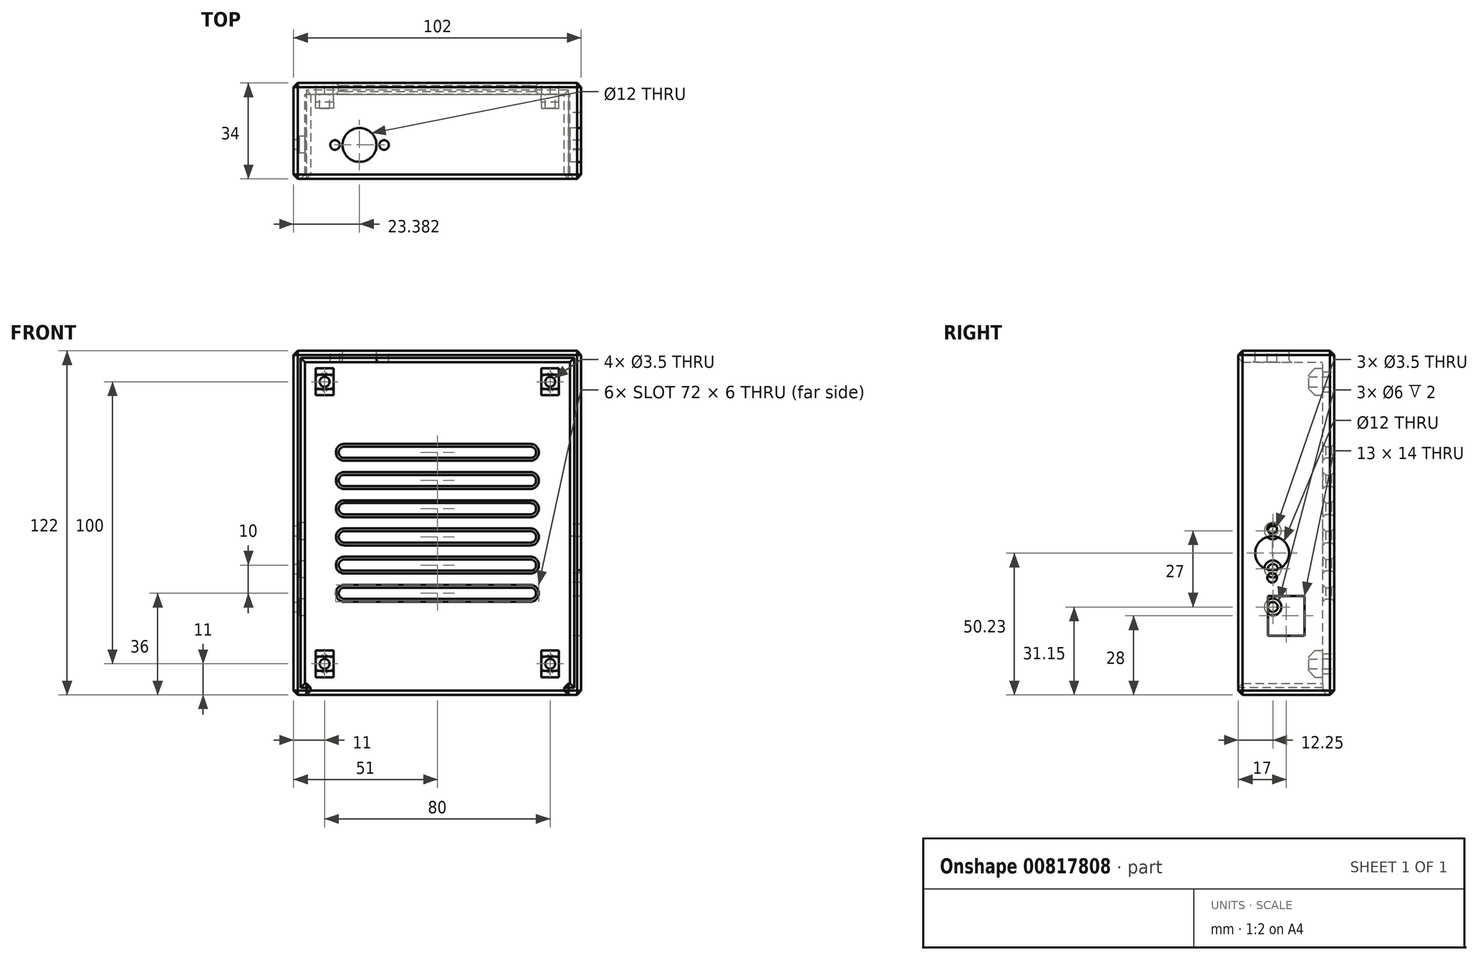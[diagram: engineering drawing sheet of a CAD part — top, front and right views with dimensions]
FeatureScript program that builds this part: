
annotation { "Feature Type Name" : "Feature", "Feature Type Description" : "" }
export const myFeature = defineFeature(function(context is Context, id is Id, definition is map)
    precondition{}
    {
        {
            var Q0;
            Q0=qCreatedBy(makeId("Front.planeOp"),FACE);
            var sketch = newSketch(context, id + "F0", { "sketchPlane" : qUnion([Q0])});
            skLineSegment(sketch, "E0.bottom", {"start": v(51, -61) * mm, "end": v(-51, -61) * mm});
            skLineSegment(sketch, "E0.top", {"start": v(51, 61) * mm, "end": v(-51, 61) * mm});
            skLineSegment(sketch, "E0.left", {"start": v(51, -61) * mm, "end": v(51, 61) * mm});
            skLineSegment(sketch, "E0.right", {"start": v(-51, -61) * mm, "end": v(-51, 61) * mm});
            skPoint(sketch, "E0.middle", {"position": v(0, 0) * mm});
            skCircle(sketch, "E1", {"center": v(-40, 50) * mm, "radius": 1.75 * mm});
            skCircle(sketch, "E2", {"center": v(40, 50) * mm, "radius": 1.75 * mm});
            skCircle(sketch, "E3", {"center": v(-40, -50) * mm, "radius": 1.75 * mm});
            skCircle(sketch, "E4", {"center": v(40, -50) * mm, "radius": 1.75 * mm});
            skLineSegment(sketch, "E5.bottom", {"start": v(47, -57) * mm, "end": v(-47, -57) * mm});
            skLineSegment(sketch, "E5.top", {"start": v(47, 57) * mm, "end": v(-47, 57) * mm});
            skLineSegment(sketch, "E5.left", {"start": v(47, -57) * mm, "end": v(47, 57) * mm});
            skLineSegment(sketch, "E5.right", {"start": v(-47, -57) * mm, "end": v(-47, 57) * mm});
            skLineSegment(sketch, "E6.bottom", {"start": v(-36.88, -54.75) * mm, "end": v(-43.13, -54.75) * mm});
            skLineSegment(sketch, "E6.top", {"start": v(-36.88, -45.25) * mm, "end": v(-43.13, -45.25) * mm});
            skLineSegment(sketch, "E6.left", {"start": v(-36.88, -54.75) * mm, "end": v(-36.88, -45.25) * mm});
            skLineSegment(sketch, "E6.right", {"start": v(-43.13, -54.75) * mm, "end": v(-43.13, -45.25) * mm});
            skLineSegment(sketch, "E7.bottom", {"start": v(36.88, -54.75) * mm, "end": v(43.12, -54.75) * mm});
            skLineSegment(sketch, "E7.top", {"start": v(36.88, -45.25) * mm, "end": v(43.12, -45.25) * mm});
            skLineSegment(sketch, "E7.left", {"start": v(36.88, -54.75) * mm, "end": v(36.88, -45.25) * mm});
            skLineSegment(sketch, "E7.right", {"start": v(43.12, -54.75) * mm, "end": v(43.12, -45.25) * mm});
            skLineSegment(sketch, "E8.bottom", {"start": v(-36.88, 45.25) * mm, "end": v(-43.13, 45.25) * mm});
            skLineSegment(sketch, "E8.top", {"start": v(-36.88, 54.75) * mm, "end": v(-43.13, 54.75) * mm});
            skLineSegment(sketch, "E8.left", {"start": v(-36.88, 45.25) * mm, "end": v(-36.88, 54.75) * mm});
            skLineSegment(sketch, "E8.right", {"start": v(-43.13, 45.25) * mm, "end": v(-43.13, 54.75) * mm});
            skLineSegment(sketch, "E9.bottom", {"start": v(36.88, 45.25) * mm, "end": v(43.12, 45.25) * mm});
            skLineSegment(sketch, "E9.top", {"start": v(36.87, 54.75) * mm, "end": v(43.12, 54.75) * mm});
            skLineSegment(sketch, "E9.left", {"start": v(36.88, 45.25) * mm, "end": v(36.88, 54.75) * mm});
            skLineSegment(sketch, "E9.right", {"start": v(43.12, 45.25) * mm, "end": v(43.12, 54.75) * mm});
            skLineSegment(sketch, "E10.bottom", {"start": v(35, 13) * mm, "end": v(-35, 13) * mm});
            skLineSegment(sketch, "E10.top", {"start": v(35, 17) * mm, "end": v(-35, 17) * mm});
            skLineSegment(sketch, "E10.left", {"start": v(35, 13) * mm, "end": v(35, 17) * mm});
            skLineSegment(sketch, "E10.right", {"start": v(-35, 13) * mm, "end": v(-35, 17) * mm});
            skPoint(sketch, "E10.middle", {"position": v(0, 15) * mm});
            skLineSegment(sketch, "E11.bottom", {"start": v(35, 3) * mm, "end": v(-35, 3) * mm});
            skLineSegment(sketch, "E11.top", {"start": v(35, 7) * mm, "end": v(-35, 7) * mm});
            skLineSegment(sketch, "E11.left", {"start": v(35, 3) * mm, "end": v(35, 7) * mm});
            skLineSegment(sketch, "E11.right", {"start": v(-35, 3) * mm, "end": v(-35, 7) * mm});
            skPoint(sketch, "E11.middle", {"position": v(0, 5) * mm});
            skLineSegment(sketch, "E12.bottom", {"start": v(35, 23) * mm, "end": v(-35, 23) * mm});
            skLineSegment(sketch, "E12.top", {"start": v(35, 27) * mm, "end": v(-35, 27) * mm});
            skLineSegment(sketch, "E12.left", {"start": v(35, 23) * mm, "end": v(35, 27) * mm});
            skLineSegment(sketch, "E12.right", {"start": v(-35, 23) * mm, "end": v(-35, 27) * mm});
            skPoint(sketch, "E12.middle", {"position": v(0, 25) * mm});
            skLineSegment(sketch, "E13.bottom", {"start": v(35, -7) * mm, "end": v(-35, -7) * mm});
            skLineSegment(sketch, "E13.top", {"start": v(35, -3) * mm, "end": v(-35, -3) * mm});
            skLineSegment(sketch, "E13.left", {"start": v(35, -7) * mm, "end": v(35, -3) * mm});
            skLineSegment(sketch, "E13.right", {"start": v(-35, -7) * mm, "end": v(-35, -3) * mm});
            skPoint(sketch, "E13.middle", {"position": v(0, -5) * mm});
            skLineSegment(sketch, "E14.bottom", {"start": v(35, -17) * mm, "end": v(-35, -17) * mm});
            skLineSegment(sketch, "E14.top", {"start": v(35, -13) * mm, "end": v(-35, -13) * mm});
            skLineSegment(sketch, "E14.left", {"start": v(35, -17) * mm, "end": v(35, -13) * mm});
            skLineSegment(sketch, "E14.right", {"start": v(-35, -17) * mm, "end": v(-35, -13) * mm});
            skPoint(sketch, "E14.middle", {"position": v(0, -15) * mm});
            skLineSegment(sketch, "E15.bottom", {"start": v(35, -27) * mm, "end": v(-35, -27) * mm});
            skLineSegment(sketch, "E15.top", {"start": v(35, -23) * mm, "end": v(-35, -23) * mm});
            skLineSegment(sketch, "E15.left", {"start": v(35, -27) * mm, "end": v(35, -23) * mm});
            skLineSegment(sketch, "E15.right", {"start": v(-35, -27) * mm, "end": v(-35, -23) * mm});
            skPoint(sketch, "E15.middle", {"position": v(0, -25) * mm});
            skLineSegment(sketch, "E16", {"start": v(-45, -57) * mm, "end": v(-45, -61) * mm});
            skLineSegment(sketch, "E17", {"start": v(45, -57) * mm, "end": v(45, -61) * mm});
            skCircle(sketch, "E18.cCircle", {"center": v(40, 50) * mm, "radius": 3.08 * mm, "construction": true});
            skLineSegment(sketch, "E18.0", {"start": v(36.92, 48.22) * mm, "end": v(36.92, 51.78) * mm});
            skLineSegment(sketch, "E18.1", {"start": v(36.93, 51.78) * mm, "end": v(40, 53.55) * mm});
            skLineSegment(sketch, "E18.2", {"start": v(40, 53.55) * mm, "end": v(43.07, 51.78) * mm});
            skLineSegment(sketch, "E18.3", {"start": v(43.07, 51.78) * mm, "end": v(43.08, 48.22) * mm});
            skLineSegment(sketch, "E18.4", {"start": v(43.08, 48.22) * mm, "end": v(40, 46.45) * mm});
            skLineSegment(sketch, "E18.5", {"start": v(40, 46.45) * mm, "end": v(36.93, 48.22) * mm});
            skPoint(sketch, "E18.0.midPoint", {"position": v(36.92, 50) * mm});
            skCircle(sketch, "E19.cCircle", {"center": v(-40, 50) * mm, "radius": 3.08 * mm, "construction": true});
            skLineSegment(sketch, "E19.0", {"start": v(-36.92, 51.78) * mm, "end": v(-36.92, 48.22) * mm});
            skLineSegment(sketch, "E19.1", {"start": v(-36.92, 48.22) * mm, "end": v(-40, 46.45) * mm});
            skLineSegment(sketch, "E19.2", {"start": v(-40, 46.45) * mm, "end": v(-43.07, 48.22) * mm});
            skLineSegment(sketch, "E19.3", {"start": v(-43.07, 48.22) * mm, "end": v(-43.07, 51.78) * mm});
            skLineSegment(sketch, "E19.4", {"start": v(-43.08, 51.78) * mm, "end": v(-40, 53.55) * mm});
            skLineSegment(sketch, "E19.5", {"start": v(-40, 53.55) * mm, "end": v(-36.92, 51.78) * mm});
            skPoint(sketch, "E19.0.midPoint", {"position": v(-36.92, 50) * mm});
            skCircle(sketch, "E20.cCircle", {"center": v(40, -50) * mm, "radius": 3.08 * mm, "construction": true});
            skPoint(sketch, "E20.cCircle.perimeterSnap0", {"position": v(43.12, -50) * mm});
            skLineSegment(sketch, "E20.0", {"start": v(43.08, -48.22) * mm, "end": v(43.08, -51.78) * mm});
            skLineSegment(sketch, "E20.1", {"start": v(43.07, -51.78) * mm, "end": v(40, -53.55) * mm});
            skLineSegment(sketch, "E20.2", {"start": v(40, -53.55) * mm, "end": v(36.93, -51.78) * mm});
            skLineSegment(sketch, "E20.3", {"start": v(36.93, -51.78) * mm, "end": v(36.93, -48.22) * mm});
            skLineSegment(sketch, "E20.4", {"start": v(36.93, -48.22) * mm, "end": v(40, -46.45) * mm});
            skLineSegment(sketch, "E20.5", {"start": v(40, -46.45) * mm, "end": v(43.07, -48.22) * mm});
            skPoint(sketch, "E20.0.midPoint", {"position": v(43.08, -50) * mm});
            skPoint(sketch, "E20.0.midPoint.positionSnap0", {"position": v(43.12, -50) * mm});
            skCircle(sketch, "E21.cCircle", {"center": v(-40, -50) * mm, "radius": 3.08 * mm, "construction": true});
            skLineSegment(sketch, "E21.0", {"start": v(-36.93, -48.22) * mm, "end": v(-36.93, -51.78) * mm});
            skLineSegment(sketch, "E21.1", {"start": v(-36.93, -51.78) * mm, "end": v(-40, -53.55) * mm});
            skLineSegment(sketch, "E21.2", {"start": v(-40, -53.55) * mm, "end": v(-43.08, -51.78) * mm});
            skLineSegment(sketch, "E21.3", {"start": v(-43.08, -51.78) * mm, "end": v(-43.08, -48.22) * mm});
            skLineSegment(sketch, "E21.4", {"start": v(-43.08, -48.22) * mm, "end": v(-40, -46.45) * mm});
            skLineSegment(sketch, "E21.5", {"start": v(-40, -46.45) * mm, "end": v(-36.93, -48.22) * mm});
            skPoint(sketch, "E21.0.midPoint", {"position": v(-36.93, -50) * mm});
            skSolve(sketch);
        }
        {
            var Q0;
            Q0=makeQuery(id+"F0.imprint","IMPRINT",FACE,{"disambiguationData":[TD([[makeQuery(id+"F0.imprint","IMPRINT",EDGE,{"derivedFrom":sQuery(id+"F0.wireOp",EDGE,"E5.top")}),1.0]])]});
            var Q1;
            {var subQ0=sQuery(id+"F0.wireOp",EDGE,"E16");Q1=makeQuery(id+"F0.imprint","IMPRINT",FACE,{"disambiguationData":[TD([[makeQuery(id+"F0.imprint","IMPRINT",EDGE,{"derivedFrom":subQ0}),1.0]])]});}
            extrude(context, id + "F1", {"entities" : qUnion([Q0, Q1]), "depth" : 4 * mm, "offsetDistance" : 25 * mm});
        }
        {
            var Q0;
            Q0=makeQuery(id+"F0.imprint","IMPRINT",FACE,{"disambiguationData":[TD([[makeQuery(id+"F0.imprint","IMPRINT",EDGE,{"derivedFrom":sQuery(id+"F0.wireOp",EDGE,"E3")}),-1.0]])]});
            var Q1;
            Q1=makeQuery(id+"F0.imprint","IMPRINT",FACE,{"disambiguationData":[TD([[makeQuery(id+"F0.imprint","IMPRINT",EDGE,{"derivedFrom":sQuery(id+"F0.wireOp",EDGE,"E4")}),-1.0]])]});
            var Q2;
            Q2=makeQuery(id+"F0.imprint","IMPRINT",FACE,{"disambiguationData":[TD([[makeQuery(id+"F0.imprint","IMPRINT",EDGE,{"derivedFrom":sQuery(id+"F0.wireOp",EDGE,"E2")}),-1.0]])]});
            var Q3;
            Q3=makeQuery(id+"F0.imprint","IMPRINT",FACE,{"disambiguationData":[TD([[makeQuery(id+"F0.imprint","IMPRINT",EDGE,{"derivedFrom":sQuery(id+"F0.wireOp",EDGE,"E1")}),-1.0]])]});
            var Q4;
            Q4=makeQuery(id+"F0.imprint","IMPRINT",FACE,{"disambiguationData":[TD([[makeQuery(id+"F0.imprint","IMPRINT",EDGE,{"derivedFrom":sQuery(id+"F0.wireOp",EDGE,"E7.bottom")}),1.0]])]});
            var Q5;
            Q5=makeQuery(id+"F0.imprint","IMPRINT",FACE,{"disambiguationData":[TD([[makeQuery(id+"F0.imprint","IMPRINT",EDGE,{"derivedFrom":sQuery(id+"F0.wireOp",EDGE,"E6.bottom")}),-1.0]])]});
            var Q6;
            Q6=makeQuery(id+"F0.imprint","IMPRINT",FACE,{"disambiguationData":[TD([[makeQuery(id+"F0.imprint","IMPRINT",EDGE,{"derivedFrom":sQuery(id+"F0.wireOp",EDGE,"E8.bottom")}),-1.0]])]});
            var Q7;
            Q7=makeQuery(id+"F0.imprint","IMPRINT",FACE,{"disambiguationData":[TD([[makeQuery(id+"F0.imprint","IMPRINT",EDGE,{"derivedFrom":sQuery(id+"F0.wireOp",EDGE,"E9.bottom")}),1.0]])]});
            extrude(context, id + "F2", {"entities" : qUnion([Q0, Q1, Q2, Q3, Q4, Q5, Q6, Q7]), "operationType" : NewBodyOperationType.ADD, "depth" : 9 * mm, "offsetDistance" : 25 * mm});
        }
        {
            var Q0;
            Q0=makeQuery(id+"F2.opExtrude","CAP_EDGE",EDGE,{"disambiguationData":[OSD([sQuery(id+"F0.wireOp",EDGE,"E6.top")])],"isStart":false});
            var Q1;
            Q1=makeQuery(id+"F2.opExtrude","CAP_EDGE",EDGE,{"disambiguationData":[OSD([sQuery(id+"F0.wireOp",EDGE,"E6.bottom")])],"isStart":false});
            var Q2;
            Q2=makeQuery(id+"F2.opExtrude","CAP_EDGE",EDGE,{"disambiguationData":[OSD([sQuery(id+"F0.wireOp",EDGE,"E7.top")])],"isStart":false});
            var Q3;
            Q3=makeQuery(id+"F2.opExtrude","CAP_EDGE",EDGE,{"disambiguationData":[OSD([sQuery(id+"F0.wireOp",EDGE,"E7.bottom")])],"isStart":false});
            var Q4;
            Q4=makeQuery(id+"F2.opExtrude","CAP_EDGE",EDGE,{"disambiguationData":[OSD([sQuery(id+"F0.wireOp",EDGE,"E8.top")])],"isStart":false});
            var Q5;
            Q5=makeQuery(id+"F2.opExtrude","CAP_EDGE",EDGE,{"disambiguationData":[OSD([sQuery(id+"F0.wireOp",EDGE,"E8.bottom")])],"isStart":false});
            var Q6;
            Q6=makeQuery(id+"F2.opExtrude","CAP_EDGE",EDGE,{"disambiguationData":[OSD([sQuery(id+"F0.wireOp",EDGE,"E9.top")])],"isStart":false});
            var Q7;
            Q7=makeQuery(id+"F2.opExtrude","CAP_EDGE",EDGE,{"disambiguationData":[OSD([sQuery(id+"F0.wireOp",EDGE,"E9.bottom")])],"isStart":false});
            chamfer(context, id + "F3", {"entities" : qUnion([Q0, Q1, Q2, Q3, Q4, Q5, Q6, Q7]), "width" : 2.2 * mm, "tangentPropagation" : true});
        }
        {
            var Q0;
            Q0=makeQuery(id+"F1.opExtrude","SWEPT_EDGE",EDGE,{"disambiguationData":[OSD([sQuery(id+"F0.wireOp",EDGE,"E15.bottom"),sQuery(id+"F0.wireOp",EDGE,"E15.left")])]});
            var Q1;
            Q1=makeQuery(id+"F1.opExtrude","SWEPT_EDGE",EDGE,{"disambiguationData":[OSD([sQuery(id+"F0.wireOp",EDGE,"E15.top"),sQuery(id+"F0.wireOp",EDGE,"E15.left")])]});
            var Q2;
            Q2=makeQuery(id+"F1.opExtrude","SWEPT_EDGE",EDGE,{"disambiguationData":[OSD([sQuery(id+"F0.wireOp",EDGE,"E14.top"),sQuery(id+"F0.wireOp",EDGE,"E14.left")])]});
            var Q3;
            Q3=makeQuery(id+"F1.opExtrude","SWEPT_EDGE",EDGE,{"disambiguationData":[OSD([sQuery(id+"F0.wireOp",EDGE,"E13.top"),sQuery(id+"F0.wireOp",EDGE,"E13.left")])]});
            var Q4;
            Q4=makeQuery(id+"F1.opExtrude","SWEPT_EDGE",EDGE,{"disambiguationData":[OSD([sQuery(id+"F0.wireOp",EDGE,"E11.top"),sQuery(id+"F0.wireOp",EDGE,"E11.left")])]});
            var Q5;
            Q5=makeQuery(id+"F1.opExtrude","SWEPT_EDGE",EDGE,{"disambiguationData":[OSD([sQuery(id+"F0.wireOp",EDGE,"E10.top"),sQuery(id+"F0.wireOp",EDGE,"E10.left")])]});
            var Q6;
            Q6=makeQuery(id+"F1.opExtrude","SWEPT_EDGE",EDGE,{"disambiguationData":[OSD([sQuery(id+"F0.wireOp",EDGE,"E12.top"),sQuery(id+"F0.wireOp",EDGE,"E12.left")])]});
            var Q7;
            Q7=makeQuery(id+"F1.opExtrude","SWEPT_EDGE",EDGE,{"disambiguationData":[OSD([sQuery(id+"F0.wireOp",EDGE,"E12.top"),sQuery(id+"F0.wireOp",EDGE,"E12.right")])]});
            var Q8;
            Q8=makeQuery(id+"F1.opExtrude","SWEPT_EDGE",EDGE,{"disambiguationData":[OSD([sQuery(id+"F0.wireOp",EDGE,"E10.top"),sQuery(id+"F0.wireOp",EDGE,"E10.right")])]});
            var Q9;
            Q9=makeQuery(id+"F1.opExtrude","SWEPT_EDGE",EDGE,{"disambiguationData":[OSD([sQuery(id+"F0.wireOp",EDGE,"E11.top"),sQuery(id+"F0.wireOp",EDGE,"E11.right")])]});
            var Q10;
            Q10=makeQuery(id+"F1.opExtrude","SWEPT_EDGE",EDGE,{"disambiguationData":[OSD([sQuery(id+"F0.wireOp",EDGE,"E13.top"),sQuery(id+"F0.wireOp",EDGE,"E13.right")])]});
            var Q11;
            Q11=makeQuery(id+"F1.opExtrude","SWEPT_EDGE",EDGE,{"disambiguationData":[OSD([sQuery(id+"F0.wireOp",EDGE,"E14.top"),sQuery(id+"F0.wireOp",EDGE,"E14.right")])]});
            var Q12;
            Q12=makeQuery(id+"F1.opExtrude","SWEPT_EDGE",EDGE,{"disambiguationData":[OSD([sQuery(id+"F0.wireOp",EDGE,"E15.top"),sQuery(id+"F0.wireOp",EDGE,"E15.right")])]});
            var Q13;
            Q13=makeQuery(id+"F1.opExtrude","SWEPT_EDGE",EDGE,{"disambiguationData":[OSD([sQuery(id+"F0.wireOp",EDGE,"E14.bottom"),sQuery(id+"F0.wireOp",EDGE,"E14.left")])]});
            var Q14;
            Q14=makeQuery(id+"F1.opExtrude","SWEPT_EDGE",EDGE,{"disambiguationData":[OSD([sQuery(id+"F0.wireOp",EDGE,"E13.bottom"),sQuery(id+"F0.wireOp",EDGE,"E13.left")])]});
            var Q15;
            Q15=makeQuery(id+"F1.opExtrude","SWEPT_EDGE",EDGE,{"disambiguationData":[OSD([sQuery(id+"F0.wireOp",EDGE,"E11.bottom"),sQuery(id+"F0.wireOp",EDGE,"E11.left")])]});
            var Q16;
            Q16=makeQuery(id+"F1.opExtrude","SWEPT_EDGE",EDGE,{"disambiguationData":[OSD([sQuery(id+"F0.wireOp",EDGE,"E10.bottom"),sQuery(id+"F0.wireOp",EDGE,"E10.left")])]});
            var Q17;
            Q17=makeQuery(id+"F1.opExtrude","SWEPT_EDGE",EDGE,{"disambiguationData":[OSD([sQuery(id+"F0.wireOp",EDGE,"E12.bottom"),sQuery(id+"F0.wireOp",EDGE,"E12.left")])]});
            var Q18;
            Q18=makeQuery(id+"F1.opExtrude","SWEPT_EDGE",EDGE,{"disambiguationData":[OSD([sQuery(id+"F0.wireOp",EDGE,"E12.bottom"),sQuery(id+"F0.wireOp",EDGE,"E12.right")])]});
            var Q19;
            Q19=makeQuery(id+"F1.opExtrude","SWEPT_EDGE",EDGE,{"disambiguationData":[OSD([sQuery(id+"F0.wireOp",EDGE,"E10.bottom"),sQuery(id+"F0.wireOp",EDGE,"E10.right")])]});
            var Q20;
            Q20=makeQuery(id+"F1.opExtrude","SWEPT_EDGE",EDGE,{"disambiguationData":[OSD([sQuery(id+"F0.wireOp",EDGE,"E11.bottom"),sQuery(id+"F0.wireOp",EDGE,"E11.right")])]});
            var Q21;
            Q21=makeQuery(id+"F1.opExtrude","SWEPT_EDGE",EDGE,{"disambiguationData":[OSD([sQuery(id+"F0.wireOp",EDGE,"E13.bottom"),sQuery(id+"F0.wireOp",EDGE,"E13.right")])]});
            var Q22;
            Q22=makeQuery(id+"F1.opExtrude","SWEPT_EDGE",EDGE,{"disambiguationData":[OSD([sQuery(id+"F0.wireOp",EDGE,"E14.bottom"),sQuery(id+"F0.wireOp",EDGE,"E14.right")])]});
            var Q23;
            Q23=makeQuery(id+"F1.opExtrude","SWEPT_EDGE",EDGE,{"disambiguationData":[OSD([sQuery(id+"F0.wireOp",EDGE,"E15.bottom"),sQuery(id+"F0.wireOp",EDGE,"E15.right")])]});
            fillet(context, id + "F4", {"entities" : qUnion([Q0, Q1, Q2, Q3, Q4, Q5, Q6, Q7, Q8, Q9, Q10, Q11, Q12, Q13, Q14, Q15, Q16, Q17, Q18, Q19, Q20, Q21, Q22, Q23]), "radius" : 2 * mm, "tangentPropagation" : true, "allowEdgeOverflow" : false});
        }
        {
            var Q0;
            Q0=makeQuery(id+"F0.imprint","IMPRINT",FACE,{"disambiguationData":[TD([[makeQuery(id+"F0.imprint","IMPRINT",EDGE,{"derivedFrom":sQuery(id+"F0.wireOp",EDGE,"E0.top")}),1.0]])]});
            extrude(context, id + "F5", {"entities" : qUnion([Q0]), "operationType" : NewBodyOperationType.ADD, "depth" : 34 * mm, "offsetDistance" : 25 * mm});
        }
        {
            var Q0;
            Q0=makeQuery(id+"F0.imprint","IMPRINT",FACE,{"disambiguationData":[TD([[makeQuery(id+"F0.imprint","IMPRINT",EDGE,{"derivedFrom":sQuery(id+"F0.wireOp",EDGE,"E2")}),-1.0]])]});
            var Q1;
            Q1=makeQuery(id+"F0.imprint","IMPRINT",FACE,{"disambiguationData":[TD([[makeQuery(id+"F0.imprint","IMPRINT",EDGE,{"derivedFrom":sQuery(id+"F0.wireOp",EDGE,"E1")}),-1.0]])]});
            var Q2;
            Q2=makeQuery(id+"F0.imprint","IMPRINT",FACE,{"disambiguationData":[TD([[makeQuery(id+"F0.imprint","IMPRINT",EDGE,{"derivedFrom":sQuery(id+"F0.wireOp",EDGE,"E4")}),-1.0]])]});
            var Q3;
            Q3=makeQuery(id+"F0.imprint","IMPRINT",FACE,{"disambiguationData":[TD([[makeQuery(id+"F0.imprint","IMPRINT",EDGE,{"derivedFrom":sQuery(id+"F0.wireOp",EDGE,"E3")}),-1.0]])]});
            extrude(context, id + "F6", {"entities" : qUnion([Q0, Q1, Q2, Q3]), "operationType" : NewBodyOperationType.REMOVE, "depth" : 4 * mm, "offsetDistance" : 25 * mm});
        }
        {
            var Q0;
            Q0=makeQuery(id+"F5.opExtrude","SWEPT_FACE",FACE,{"disambiguationData":[OSD([sQuery(id+"F0.wireOp",EDGE,"E5.left")])]});
            var sketch = newSketch(context, id + "F7", { "sketchPlane" : qUnion([Q0])});
            skLineSegment(sketch, "E22.bottom", {"start": v(23.5, -40) * mm, "end": v(10.5, -40) * mm});
            skLineSegment(sketch, "E22.top", {"start": v(23.5, -26) * mm, "end": v(10.5, -26) * mm});
            skLineSegment(sketch, "E22.left", {"start": v(23.5, -40) * mm, "end": v(23.5, -26) * mm});
            skLineSegment(sketch, "E22.right", {"start": v(10.5, -40) * mm, "end": v(10.5, -26) * mm});
            skPoint(sketch, "E22.middle", {"position": v(17, -33) * mm});
            skCircle(sketch, "E23", {"center": v(22, -10.77) * mm, "radius": 6 * mm});
            skCircle(sketch, "E24", {"center": v(22, -19.47) * mm, "radius": 1.7 * mm});
            skCircle(sketch, "E25", {"center": v(22, -2.07) * mm, "radius": 1.7 * mm});
            skSolve(sketch);
        }
        {
            var Q0;
            Q0=makeQuery(id+"F7.imprint","IMPRINT",FACE,{"disambiguationData":[TD([[makeQuery(id+"F7.imprint","IMPRINT",EDGE,{"derivedFrom":sQuery(id+"F7.wireOp",EDGE,"E22.bottom")}),-1.0]])]});
            var Q1;
            Q1=makeQuery(id+"F7.imprint","IMPRINT",FACE,{"disambiguationData":[TD([[makeQuery(id+"F7.imprint","IMPRINT",EDGE,{"derivedFrom":sQuery(id+"F7.wireOp",EDGE,"E23")}),1.0]])]});
            var Q2;
            Q2=makeQuery(id+"F7.imprint","IMPRINT",FACE,{"disambiguationData":[TD([[makeQuery(id+"F7.imprint","IMPRINT",EDGE,{"derivedFrom":sQuery(id+"F7.wireOp",EDGE,"E24")}),1.0]])]});
            var Q3;
            Q3=makeQuery(id+"F7.imprint","IMPRINT",FACE,{"disambiguationData":[TD([[makeQuery(id+"F7.imprint","IMPRINT",EDGE,{"derivedFrom":sQuery(id+"F7.wireOp",EDGE,"E25")}),1.0]])]});
            extrude(context, id + "F8", {"entities" : qUnion([Q0, Q1, Q2, Q3]), "operationType" : NewBodyOperationType.REMOVE, "oppositeDirection" : true, "depth" : 5 * mm, "offsetDistance" : 25 * mm});
        }
        {
            var Q0;
            Q0=makeQuery(id+"F5.opExtrude","SWEPT_FACE",FACE,{"disambiguationData":[OSD([sQuery(id+"F0.wireOp",EDGE,"E0.top")])]});
            var sketch = newSketch(context, id + "F9", { "sketchPlane" : qUnion([Q0])});
            skCircle(sketch, "E26", {"center": v(-27.62, -22) * mm, "radius": 6 * mm});
            skCircle(sketch, "E27", {"center": v(-18.92, -22) * mm, "radius": 1.7 * mm});
            skCircle(sketch, "E28", {"center": v(-36.32, -22) * mm, "radius": 1.7 * mm});
            skSolve(sketch);
        }
        {
            var Q0;
            Q0=makeQuery(id+"F9.imprint","IMPRINT",FACE,{"disambiguationData":[TD([[makeQuery(id+"F9.imprint","IMPRINT",EDGE,{"derivedFrom":sQuery(id+"F9.wireOp",EDGE,"E26")}),1.0]])]});
            var Q1;
            Q1=makeQuery(id+"F9.imprint","IMPRINT",FACE,{"disambiguationData":[TD([[makeQuery(id+"F9.imprint","IMPRINT",EDGE,{"derivedFrom":sQuery(id+"F9.wireOp",EDGE,"E28")}),1.0]])]});
            var Q2;
            Q2=makeQuery(id+"F9.imprint","IMPRINT",FACE,{"disambiguationData":[TD([[makeQuery(id+"F9.imprint","IMPRINT",EDGE,{"derivedFrom":sQuery(id+"F9.wireOp",EDGE,"E27")}),1.0]])]});
            extrude(context, id + "F10", {"entities" : qUnion([Q0, Q1, Q2]), "operationType" : NewBodyOperationType.REMOVE, "oppositeDirection" : true, "depth" : 5 * mm, "offsetDistance" : 25 * mm});
        }
        {
            var Q0;
            Q0=makeQuery(id+"F5.opExtrude","CAP_EDGE",EDGE,{"disambiguationData":[OSD([sQuery(id+"F0.wireOp",EDGE,"E0.left")])],"isStart":true});
            var Q1;
            Q1=makeQuery(id+"F5.opExtrude","SWEPT_EDGE",EDGE,{"disambiguationData":[OSD([sQuery(id+"F0.wireOp",EDGE,"E0.top"),sQuery(id+"F0.wireOp",EDGE,"E0.left")])]});
            var Q2;
            Q2=makeQuery(id+"F5.opExtrude","CAP_EDGE",EDGE,{"disambiguationData":[OSD([sQuery(id+"F0.wireOp",EDGE,"E0.left")])],"isStart":false});
            var Q3;
            Q3=makeQuery(id+"F5.opExtrude","CAP_EDGE",EDGE,{"disambiguationData":[OSD([sQuery(id+"F0.wireOp",EDGE,"E0.top")])],"isStart":false});
            var Q4;
            Q4=makeQuery(id+"F5.opExtrude","CAP_EDGE",EDGE,{"disambiguationData":[OSD([sQuery(id+"F0.wireOp",EDGE,"E0.top")])],"isStart":true});
            var Q5;
            Q5=makeQuery(id+"F5.opExtrude","CAP_EDGE",EDGE,{"disambiguationData":[OSD([sQuery(id+"F0.wireOp",EDGE,"E0.right")])],"isStart":true});
            var Q6;
            Q6=makeQuery(id+"F5.opExtrude","SWEPT_EDGE",EDGE,{"disambiguationData":[OSD([sQuery(id+"F0.wireOp",EDGE,"E0.top"),sQuery(id+"F0.wireOp",EDGE,"E0.right")])]});
            var Q7;
            Q7=makeQuery(id+"F5.opExtrude","CAP_EDGE",EDGE,{"disambiguationData":[OSD([sQuery(id+"F0.wireOp",EDGE,"E0.right")])],"isStart":false});
            var Q8;
            Q8=makeQuery(id+"F5.opExtrude","SWEPT_EDGE",EDGE,{"disambiguationData":[OSD([sQuery(id+"F0.wireOp",EDGE,"E0.bottom"),sQuery(id+"F0.wireOp",EDGE,"E0.right")])]});
            var Q9;
            {var subQ0=sQuery(id+"F0.wireOp",EDGE,"E0.bottom");Q9=makeQuery(id+"F5.boolean.opBoolean","MERGE",EDGE,{"derivedFrom":[makeQuery(id+"F1.opExtrude","CAP_EDGE",EDGE,{"disambiguationData":[OSD([subQ0])],"isStart":true}),makeQuery(id+"F5.opExtrude","CAP_EDGE",EDGE,{"disambiguationData":[OSD([subQ0]),TDD([makeQuery(id+"F0.imprint","IMPRINT",EDGE,{"disambiguationData":[TD([[makeQuery(id+"F0.imprint","INTERSECT",VERTEX,{"derivedFrom":[subQ0,sQuery(id+"F0.wireOp",EDGE,"E0.left")]}),-1.0]])],"derivedFrom":subQ0})])],"isStart":true}),makeQuery(id+"F5.opExtrude","CAP_EDGE",EDGE,{"disambiguationData":[OSD([subQ0]),TDD([makeQuery(id+"F0.imprint","IMPRINT",EDGE,{"disambiguationData":[TD([[makeQuery(id+"F0.imprint","INTERSECT",VERTEX,{"derivedFrom":[subQ0,sQuery(id+"F0.wireOp",EDGE,"E0.right")]}),1.0]])],"derivedFrom":subQ0})])],"isStart":true})]});}
            var Q10;
            Q10=makeQuery(id+"F5.opExtrude","SWEPT_EDGE",EDGE,{"disambiguationData":[OSD([sQuery(id+"F0.wireOp",EDGE,"E0.bottom"),sQuery(id+"F0.wireOp",EDGE,"E0.left")])]});
            var Q11;
            Q11=makeQuery(id+"F5.opExtrude","SWEPT_EDGE",EDGE,{"disambiguationData":[OSD([sQuery(id+"F0.wireOp",EDGE,"E0.bottom"),sQuery(id+"F0.wireOp",EDGE,"E17")])]});
            var Q12;
            {var subQ0=sQuery(id+"F0.wireOp",EDGE,"E0.bottom");Q12=makeQuery(id+"F5.opExtrude","CAP_EDGE",EDGE,{"disambiguationData":[OSD([subQ0]),TDD([makeQuery(id+"F0.imprint","IMPRINT",EDGE,{"disambiguationData":[TD([[makeQuery(id+"F0.imprint","INTERSECT",VERTEX,{"derivedFrom":[subQ0,sQuery(id+"F0.wireOp",EDGE,"E0.left")]}),-1.0]])],"derivedFrom":subQ0})])],"isStart":false});}
            var Q13;
            {var subQ0=sQuery(id+"F0.wireOp",EDGE,"E0.bottom");Q13=makeQuery(id+"F5.opExtrude","CAP_EDGE",EDGE,{"disambiguationData":[OSD([subQ0]),TDD([makeQuery(id+"F0.imprint","IMPRINT",EDGE,{"disambiguationData":[TD([[makeQuery(id+"F0.imprint","INTERSECT",VERTEX,{"derivedFrom":[subQ0,sQuery(id+"F0.wireOp",EDGE,"E0.right")]}),1.0]])],"derivedFrom":subQ0})])],"isStart":false});}
            var Q14;
            Q14=makeQuery(id+"F5.opExtrude","CAP_EDGE",EDGE,{"disambiguationData":[OSD([sQuery(id+"F0.wireOp",EDGE,"E5.left")])],"isStart":false});
            var Q15;
            Q15=makeQuery(id+"F5.opExtrude","CAP_EDGE",EDGE,{"disambiguationData":[OSD([sQuery(id+"F0.wireOp",EDGE,"E5.top")])],"isStart":false});
            var Q16;
            Q16=makeQuery(id+"F5.opExtrude","CAP_EDGE",EDGE,{"disambiguationData":[OSD([sQuery(id+"F0.wireOp",EDGE,"E5.right")])],"isStart":false});
            var Q17;
            {var subQ0=sQuery(id+"F0.wireOp",EDGE,"E5.bottom");Q17=makeQuery(id+"F5.opExtrude","CAP_EDGE",EDGE,{"disambiguationData":[OSD([subQ0]),TDD([makeQuery(id+"F0.imprint","IMPRINT",EDGE,{"disambiguationData":[TD([[makeQuery(id+"F0.imprint","INTERSECT",VERTEX,{"derivedFrom":[subQ0,sQuery(id+"F0.wireOp",EDGE,"E5.left")]}),-1.0]])],"derivedFrom":subQ0})])],"isStart":false});}
            var Q18;
            Q18=makeQuery(id+"F5.opExtrude","CAP_EDGE",EDGE,{"disambiguationData":[OSD([sQuery(id+"F0.wireOp",EDGE,"E17")])],"isStart":false});
            var Q19;
            {var subQ0=sQuery(id+"F0.wireOp",EDGE,"E5.bottom");Q19=makeQuery(id+"F5.opExtrude","CAP_EDGE",EDGE,{"disambiguationData":[OSD([subQ0]),TDD([makeQuery(id+"F0.imprint","IMPRINT",EDGE,{"disambiguationData":[TD([[makeQuery(id+"F0.imprint","INTERSECT",VERTEX,{"derivedFrom":[subQ0,sQuery(id+"F0.wireOp",EDGE,"E5.right")]}),1.0]])],"derivedFrom":subQ0})])],"isStart":false});}
            var Q20;
            Q20=makeQuery(id+"F5.opExtrude","SWEPT_EDGE",EDGE,{"disambiguationData":[OSD([sQuery(id+"F0.wireOp",EDGE,"E5.bottom"),sQuery(id+"F0.wireOp",EDGE,"E16")])]});
            var Q21;
            Q21=makeQuery(id+"F5.opExtrude","SWEPT_EDGE",EDGE,{"disambiguationData":[OSD([sQuery(id+"F0.wireOp",EDGE,"E0.bottom"),sQuery(id+"F0.wireOp",EDGE,"E16")])]});
            var Q22;
            Q22=makeQuery(id+"F5.opExtrude","CAP_EDGE",EDGE,{"disambiguationData":[OSD([sQuery(id+"F0.wireOp",EDGE,"E16")])],"isStart":false});
            var Q23;
            Q23=makeQuery(id+"F1.opExtrude","CAP_EDGE",EDGE,{"disambiguationData":[OSD([sQuery(id+"F0.wireOp",EDGE,"E0.bottom")])],"isStart":false});
            var Q24;
            Q24=makeQuery(id+"F5.opExtrude","SWEPT_EDGE",EDGE,{"disambiguationData":[OSD([sQuery(id+"F0.wireOp",EDGE,"E5.bottom"),sQuery(id+"F0.wireOp",EDGE,"E17")])]});
            chamfer(context, id + "F11", {"entities" : qUnion([Q0, Q1, Q2, Q3, Q4, Q5, Q6, Q7, Q8, Q9, Q10, Q11, Q12, Q13, Q14, Q15, Q16, Q17, Q18, Q19, Q20, Q21, Q22, Q23, Q24]), "width" : 1.5 * mm, "tangentPropagation" : true});
        }
        {
            var Q0;
            Q0=makeQuery(id+"F1.opExtrude","CAP_EDGE",EDGE,{"disambiguationData":[OSD([sQuery(id+"F0.wireOp",EDGE,"E15.bottom")])],"isStart":false});
            var Q1;
            {var subQ0=sQuery(id+"F0.wireOp",EDGE,"E15.right");var subQ1=sQuery(id+"F0.wireOp",EDGE,"E15.top");Q1=makeQuery(id+"F4.opFillet","BLEND_EDGE",EDGE,{"blendedFrom":[makeQuery(id+"F1.opExtrude","SWEPT_EDGE",EDGE,{"disambiguationData":[OSD([subQ1,subQ0])]}),makeQuery(id+"F1.opExtrude","CAP_FACE",FACE,{"disambiguationData":[OSD([sQuery(id+"F0.wireOp",EDGE,"E0.bottom"),sQuery(id+"F0.wireOp",EDGE,"E5.bottom"),sQuery(id+"F0.wireOp",EDGE,"E5.top"),sQuery(id+"F0.wireOp",EDGE,"E5.left"),sQuery(id+"F0.wireOp",EDGE,"E5.right"),sQuery(id+"F0.wireOp",EDGE,"E6.bottom"),sQuery(id+"F0.wireOp",EDGE,"E6.top"),sQuery(id+"F0.wireOp",EDGE,"E6.left"),sQuery(id+"F0.wireOp",EDGE,"E6.right"),sQuery(id+"F0.wireOp",EDGE,"E7.bottom"),sQuery(id+"F0.wireOp",EDGE,"E7.top"),sQuery(id+"F0.wireOp",EDGE,"E7.left"),sQuery(id+"F0.wireOp",EDGE,"E7.right"),sQuery(id+"F0.wireOp",EDGE,"E8.bottom"),sQuery(id+"F0.wireOp",EDGE,"E8.top"),sQuery(id+"F0.wireOp",EDGE,"E8.left"),sQuery(id+"F0.wireOp",EDGE,"E8.right"),sQuery(id+"F0.wireOp",EDGE,"E9.bottom"),sQuery(id+"F0.wireOp",EDGE,"E9.top"),sQuery(id+"F0.wireOp",EDGE,"E9.left"),sQuery(id+"F0.wireOp",EDGE,"E9.right"),sQuery(id+"F0.wireOp",EDGE,"E10.bottom"),sQuery(id+"F0.wireOp",EDGE,"E10.top"),sQuery(id+"F0.wireOp",EDGE,"E10.left"),sQuery(id+"F0.wireOp",EDGE,"E10.right"),sQuery(id+"F0.wireOp",EDGE,"E11.bottom"),sQuery(id+"F0.wireOp",EDGE,"E11.top"),sQuery(id+"F0.wireOp",EDGE,"E11.left"),sQuery(id+"F0.wireOp",EDGE,"E11.right"),sQuery(id+"F0.wireOp",EDGE,"E12.bottom"),sQuery(id+"F0.wireOp",EDGE,"E12.top"),sQuery(id+"F0.wireOp",EDGE,"E12.left"),sQuery(id+"F0.wireOp",EDGE,"E12.right"),sQuery(id+"F0.wireOp",EDGE,"E13.bottom"),sQuery(id+"F0.wireOp",EDGE,"E13.top"),sQuery(id+"F0.wireOp",EDGE,"E13.left"),sQuery(id+"F0.wireOp",EDGE,"E13.right"),sQuery(id+"F0.wireOp",EDGE,"E14.bottom"),sQuery(id+"F0.wireOp",EDGE,"E14.top"),sQuery(id+"F0.wireOp",EDGE,"E14.left"),sQuery(id+"F0.wireOp",EDGE,"E14.right"),sQuery(id+"F0.wireOp",EDGE,"E15.bottom"),subQ1,sQuery(id+"F0.wireOp",EDGE,"E15.left"),subQ0,sQuery(id+"F0.wireOp",EDGE,"E16"),sQuery(id+"F0.wireOp",EDGE,"E17")])],"isStart":false})],"blendedInto":[makeQuery(id+"F1.opExtrude","CAP_FACE",FACE,{"disambiguationData":[OSD([sQuery(id+"F0.wireOp",EDGE,"E0.bottom"),sQuery(id+"F0.wireOp",EDGE,"E5.bottom"),sQuery(id+"F0.wireOp",EDGE,"E5.top"),sQuery(id+"F0.wireOp",EDGE,"E5.left"),sQuery(id+"F0.wireOp",EDGE,"E5.right"),sQuery(id+"F0.wireOp",EDGE,"E6.bottom"),sQuery(id+"F0.wireOp",EDGE,"E6.top"),sQuery(id+"F0.wireOp",EDGE,"E6.left"),sQuery(id+"F0.wireOp",EDGE,"E6.right"),sQuery(id+"F0.wireOp",EDGE,"E7.bottom"),sQuery(id+"F0.wireOp",EDGE,"E7.top"),sQuery(id+"F0.wireOp",EDGE,"E7.left"),sQuery(id+"F0.wireOp",EDGE,"E7.right"),sQuery(id+"F0.wireOp",EDGE,"E8.bottom"),sQuery(id+"F0.wireOp",EDGE,"E8.top"),sQuery(id+"F0.wireOp",EDGE,"E8.left"),sQuery(id+"F0.wireOp",EDGE,"E8.right"),sQuery(id+"F0.wireOp",EDGE,"E9.bottom"),sQuery(id+"F0.wireOp",EDGE,"E9.top"),sQuery(id+"F0.wireOp",EDGE,"E9.left"),sQuery(id+"F0.wireOp",EDGE,"E9.right"),sQuery(id+"F0.wireOp",EDGE,"E10.bottom"),sQuery(id+"F0.wireOp",EDGE,"E10.top"),sQuery(id+"F0.wireOp",EDGE,"E10.left"),sQuery(id+"F0.wireOp",EDGE,"E10.right"),sQuery(id+"F0.wireOp",EDGE,"E11.bottom"),sQuery(id+"F0.wireOp",EDGE,"E11.top"),sQuery(id+"F0.wireOp",EDGE,"E11.left"),sQuery(id+"F0.wireOp",EDGE,"E11.right"),sQuery(id+"F0.wireOp",EDGE,"E12.bottom"),sQuery(id+"F0.wireOp",EDGE,"E12.top"),sQuery(id+"F0.wireOp",EDGE,"E12.left"),sQuery(id+"F0.wireOp",EDGE,"E12.right"),sQuery(id+"F0.wireOp",EDGE,"E13.bottom"),sQuery(id+"F0.wireOp",EDGE,"E13.top"),sQuery(id+"F0.wireOp",EDGE,"E13.left"),sQuery(id+"F0.wireOp",EDGE,"E13.right"),sQuery(id+"F0.wireOp",EDGE,"E14.bottom"),sQuery(id+"F0.wireOp",EDGE,"E14.top"),sQuery(id+"F0.wireOp",EDGE,"E14.left"),sQuery(id+"F0.wireOp",EDGE,"E14.right"),sQuery(id+"F0.wireOp",EDGE,"E15.bottom"),subQ1,sQuery(id+"F0.wireOp",EDGE,"E15.left"),subQ0,sQuery(id+"F0.wireOp",EDGE,"E16"),sQuery(id+"F0.wireOp",EDGE,"E17")])],"isStart":false})]});}
            var Q2;
            Q2=makeQuery(id+"F1.opExtrude","CAP_EDGE",EDGE,{"disambiguationData":[OSD([sQuery(id+"F0.wireOp",EDGE,"E15.top")])],"isStart":false});
            var Q3;
            {var subQ0=sQuery(id+"F0.wireOp",EDGE,"E15.left");var subQ1=sQuery(id+"F0.wireOp",EDGE,"E15.bottom");Q3=makeQuery(id+"F4.opFillet","BLEND_EDGE",EDGE,{"blendedFrom":[makeQuery(id+"F1.opExtrude","SWEPT_EDGE",EDGE,{"disambiguationData":[OSD([subQ1,subQ0])]}),makeQuery(id+"F1.opExtrude","CAP_FACE",FACE,{"disambiguationData":[OSD([sQuery(id+"F0.wireOp",EDGE,"E0.bottom"),sQuery(id+"F0.wireOp",EDGE,"E5.bottom"),sQuery(id+"F0.wireOp",EDGE,"E5.top"),sQuery(id+"F0.wireOp",EDGE,"E5.left"),sQuery(id+"F0.wireOp",EDGE,"E5.right"),sQuery(id+"F0.wireOp",EDGE,"E6.bottom"),sQuery(id+"F0.wireOp",EDGE,"E6.top"),sQuery(id+"F0.wireOp",EDGE,"E6.left"),sQuery(id+"F0.wireOp",EDGE,"E6.right"),sQuery(id+"F0.wireOp",EDGE,"E7.bottom"),sQuery(id+"F0.wireOp",EDGE,"E7.top"),sQuery(id+"F0.wireOp",EDGE,"E7.left"),sQuery(id+"F0.wireOp",EDGE,"E7.right"),sQuery(id+"F0.wireOp",EDGE,"E8.bottom"),sQuery(id+"F0.wireOp",EDGE,"E8.top"),sQuery(id+"F0.wireOp",EDGE,"E8.left"),sQuery(id+"F0.wireOp",EDGE,"E8.right"),sQuery(id+"F0.wireOp",EDGE,"E9.bottom"),sQuery(id+"F0.wireOp",EDGE,"E9.top"),sQuery(id+"F0.wireOp",EDGE,"E9.left"),sQuery(id+"F0.wireOp",EDGE,"E9.right"),sQuery(id+"F0.wireOp",EDGE,"E10.bottom"),sQuery(id+"F0.wireOp",EDGE,"E10.top"),sQuery(id+"F0.wireOp",EDGE,"E10.left"),sQuery(id+"F0.wireOp",EDGE,"E10.right"),sQuery(id+"F0.wireOp",EDGE,"E11.bottom"),sQuery(id+"F0.wireOp",EDGE,"E11.top"),sQuery(id+"F0.wireOp",EDGE,"E11.left"),sQuery(id+"F0.wireOp",EDGE,"E11.right"),sQuery(id+"F0.wireOp",EDGE,"E12.bottom"),sQuery(id+"F0.wireOp",EDGE,"E12.top"),sQuery(id+"F0.wireOp",EDGE,"E12.left"),sQuery(id+"F0.wireOp",EDGE,"E12.right"),sQuery(id+"F0.wireOp",EDGE,"E13.bottom"),sQuery(id+"F0.wireOp",EDGE,"E13.top"),sQuery(id+"F0.wireOp",EDGE,"E13.left"),sQuery(id+"F0.wireOp",EDGE,"E13.right"),sQuery(id+"F0.wireOp",EDGE,"E14.bottom"),sQuery(id+"F0.wireOp",EDGE,"E14.top"),sQuery(id+"F0.wireOp",EDGE,"E14.left"),sQuery(id+"F0.wireOp",EDGE,"E14.right"),subQ1,sQuery(id+"F0.wireOp",EDGE,"E15.top"),subQ0,sQuery(id+"F0.wireOp",EDGE,"E15.right"),sQuery(id+"F0.wireOp",EDGE,"E16"),sQuery(id+"F0.wireOp",EDGE,"E17")])],"isStart":false})],"blendedInto":[makeQuery(id+"F1.opExtrude","CAP_FACE",FACE,{"disambiguationData":[OSD([sQuery(id+"F0.wireOp",EDGE,"E0.bottom"),sQuery(id+"F0.wireOp",EDGE,"E5.bottom"),sQuery(id+"F0.wireOp",EDGE,"E5.top"),sQuery(id+"F0.wireOp",EDGE,"E5.left"),sQuery(id+"F0.wireOp",EDGE,"E5.right"),sQuery(id+"F0.wireOp",EDGE,"E6.bottom"),sQuery(id+"F0.wireOp",EDGE,"E6.top"),sQuery(id+"F0.wireOp",EDGE,"E6.left"),sQuery(id+"F0.wireOp",EDGE,"E6.right"),sQuery(id+"F0.wireOp",EDGE,"E7.bottom"),sQuery(id+"F0.wireOp",EDGE,"E7.top"),sQuery(id+"F0.wireOp",EDGE,"E7.left"),sQuery(id+"F0.wireOp",EDGE,"E7.right"),sQuery(id+"F0.wireOp",EDGE,"E8.bottom"),sQuery(id+"F0.wireOp",EDGE,"E8.top"),sQuery(id+"F0.wireOp",EDGE,"E8.left"),sQuery(id+"F0.wireOp",EDGE,"E8.right"),sQuery(id+"F0.wireOp",EDGE,"E9.bottom"),sQuery(id+"F0.wireOp",EDGE,"E9.top"),sQuery(id+"F0.wireOp",EDGE,"E9.left"),sQuery(id+"F0.wireOp",EDGE,"E9.right"),sQuery(id+"F0.wireOp",EDGE,"E10.bottom"),sQuery(id+"F0.wireOp",EDGE,"E10.top"),sQuery(id+"F0.wireOp",EDGE,"E10.left"),sQuery(id+"F0.wireOp",EDGE,"E10.right"),sQuery(id+"F0.wireOp",EDGE,"E11.bottom"),sQuery(id+"F0.wireOp",EDGE,"E11.top"),sQuery(id+"F0.wireOp",EDGE,"E11.left"),sQuery(id+"F0.wireOp",EDGE,"E11.right"),sQuery(id+"F0.wireOp",EDGE,"E12.bottom"),sQuery(id+"F0.wireOp",EDGE,"E12.top"),sQuery(id+"F0.wireOp",EDGE,"E12.left"),sQuery(id+"F0.wireOp",EDGE,"E12.right"),sQuery(id+"F0.wireOp",EDGE,"E13.bottom"),sQuery(id+"F0.wireOp",EDGE,"E13.top"),sQuery(id+"F0.wireOp",EDGE,"E13.left"),sQuery(id+"F0.wireOp",EDGE,"E13.right"),sQuery(id+"F0.wireOp",EDGE,"E14.bottom"),sQuery(id+"F0.wireOp",EDGE,"E14.top"),sQuery(id+"F0.wireOp",EDGE,"E14.left"),sQuery(id+"F0.wireOp",EDGE,"E14.right"),subQ1,sQuery(id+"F0.wireOp",EDGE,"E15.top"),subQ0,sQuery(id+"F0.wireOp",EDGE,"E15.right"),sQuery(id+"F0.wireOp",EDGE,"E16"),sQuery(id+"F0.wireOp",EDGE,"E17")])],"isStart":false})]});}
            var Q4;
            {var subQ0=sQuery(id+"F0.wireOp",EDGE,"E14.left");var subQ1=sQuery(id+"F0.wireOp",EDGE,"E14.bottom");Q4=makeQuery(id+"F4.opFillet","BLEND_EDGE",EDGE,{"blendedFrom":[makeQuery(id+"F1.opExtrude","SWEPT_EDGE",EDGE,{"disambiguationData":[OSD([subQ1,subQ0])]}),makeQuery(id+"F1.opExtrude","CAP_FACE",FACE,{"disambiguationData":[OSD([sQuery(id+"F0.wireOp",EDGE,"E0.bottom"),sQuery(id+"F0.wireOp",EDGE,"E5.bottom"),sQuery(id+"F0.wireOp",EDGE,"E5.top"),sQuery(id+"F0.wireOp",EDGE,"E5.left"),sQuery(id+"F0.wireOp",EDGE,"E5.right"),sQuery(id+"F0.wireOp",EDGE,"E6.bottom"),sQuery(id+"F0.wireOp",EDGE,"E6.top"),sQuery(id+"F0.wireOp",EDGE,"E6.left"),sQuery(id+"F0.wireOp",EDGE,"E6.right"),sQuery(id+"F0.wireOp",EDGE,"E7.bottom"),sQuery(id+"F0.wireOp",EDGE,"E7.top"),sQuery(id+"F0.wireOp",EDGE,"E7.left"),sQuery(id+"F0.wireOp",EDGE,"E7.right"),sQuery(id+"F0.wireOp",EDGE,"E8.bottom"),sQuery(id+"F0.wireOp",EDGE,"E8.top"),sQuery(id+"F0.wireOp",EDGE,"E8.left"),sQuery(id+"F0.wireOp",EDGE,"E8.right"),sQuery(id+"F0.wireOp",EDGE,"E9.bottom"),sQuery(id+"F0.wireOp",EDGE,"E9.top"),sQuery(id+"F0.wireOp",EDGE,"E9.left"),sQuery(id+"F0.wireOp",EDGE,"E9.right"),sQuery(id+"F0.wireOp",EDGE,"E10.bottom"),sQuery(id+"F0.wireOp",EDGE,"E10.top"),sQuery(id+"F0.wireOp",EDGE,"E10.left"),sQuery(id+"F0.wireOp",EDGE,"E10.right"),sQuery(id+"F0.wireOp",EDGE,"E11.bottom"),sQuery(id+"F0.wireOp",EDGE,"E11.top"),sQuery(id+"F0.wireOp",EDGE,"E11.left"),sQuery(id+"F0.wireOp",EDGE,"E11.right"),sQuery(id+"F0.wireOp",EDGE,"E12.bottom"),sQuery(id+"F0.wireOp",EDGE,"E12.top"),sQuery(id+"F0.wireOp",EDGE,"E12.left"),sQuery(id+"F0.wireOp",EDGE,"E12.right"),sQuery(id+"F0.wireOp",EDGE,"E13.bottom"),sQuery(id+"F0.wireOp",EDGE,"E13.top"),sQuery(id+"F0.wireOp",EDGE,"E13.left"),sQuery(id+"F0.wireOp",EDGE,"E13.right"),subQ1,sQuery(id+"F0.wireOp",EDGE,"E14.top"),subQ0,sQuery(id+"F0.wireOp",EDGE,"E14.right"),sQuery(id+"F0.wireOp",EDGE,"E15.bottom"),sQuery(id+"F0.wireOp",EDGE,"E15.top"),sQuery(id+"F0.wireOp",EDGE,"E15.left"),sQuery(id+"F0.wireOp",EDGE,"E15.right"),sQuery(id+"F0.wireOp",EDGE,"E16"),sQuery(id+"F0.wireOp",EDGE,"E17")])],"isStart":false})],"blendedInto":[makeQuery(id+"F1.opExtrude","CAP_FACE",FACE,{"disambiguationData":[OSD([sQuery(id+"F0.wireOp",EDGE,"E0.bottom"),sQuery(id+"F0.wireOp",EDGE,"E5.bottom"),sQuery(id+"F0.wireOp",EDGE,"E5.top"),sQuery(id+"F0.wireOp",EDGE,"E5.left"),sQuery(id+"F0.wireOp",EDGE,"E5.right"),sQuery(id+"F0.wireOp",EDGE,"E6.bottom"),sQuery(id+"F0.wireOp",EDGE,"E6.top"),sQuery(id+"F0.wireOp",EDGE,"E6.left"),sQuery(id+"F0.wireOp",EDGE,"E6.right"),sQuery(id+"F0.wireOp",EDGE,"E7.bottom"),sQuery(id+"F0.wireOp",EDGE,"E7.top"),sQuery(id+"F0.wireOp",EDGE,"E7.left"),sQuery(id+"F0.wireOp",EDGE,"E7.right"),sQuery(id+"F0.wireOp",EDGE,"E8.bottom"),sQuery(id+"F0.wireOp",EDGE,"E8.top"),sQuery(id+"F0.wireOp",EDGE,"E8.left"),sQuery(id+"F0.wireOp",EDGE,"E8.right"),sQuery(id+"F0.wireOp",EDGE,"E9.bottom"),sQuery(id+"F0.wireOp",EDGE,"E9.top"),sQuery(id+"F0.wireOp",EDGE,"E9.left"),sQuery(id+"F0.wireOp",EDGE,"E9.right"),sQuery(id+"F0.wireOp",EDGE,"E10.bottom"),sQuery(id+"F0.wireOp",EDGE,"E10.top"),sQuery(id+"F0.wireOp",EDGE,"E10.left"),sQuery(id+"F0.wireOp",EDGE,"E10.right"),sQuery(id+"F0.wireOp",EDGE,"E11.bottom"),sQuery(id+"F0.wireOp",EDGE,"E11.top"),sQuery(id+"F0.wireOp",EDGE,"E11.left"),sQuery(id+"F0.wireOp",EDGE,"E11.right"),sQuery(id+"F0.wireOp",EDGE,"E12.bottom"),sQuery(id+"F0.wireOp",EDGE,"E12.top"),sQuery(id+"F0.wireOp",EDGE,"E12.left"),sQuery(id+"F0.wireOp",EDGE,"E12.right"),sQuery(id+"F0.wireOp",EDGE,"E13.bottom"),sQuery(id+"F0.wireOp",EDGE,"E13.top"),sQuery(id+"F0.wireOp",EDGE,"E13.left"),sQuery(id+"F0.wireOp",EDGE,"E13.right"),subQ1,sQuery(id+"F0.wireOp",EDGE,"E14.top"),subQ0,sQuery(id+"F0.wireOp",EDGE,"E14.right"),sQuery(id+"F0.wireOp",EDGE,"E15.bottom"),sQuery(id+"F0.wireOp",EDGE,"E15.top"),sQuery(id+"F0.wireOp",EDGE,"E15.left"),sQuery(id+"F0.wireOp",EDGE,"E15.right"),sQuery(id+"F0.wireOp",EDGE,"E16"),sQuery(id+"F0.wireOp",EDGE,"E17")])],"isStart":false})]});}
            var Q5;
            Q5=makeQuery(id+"F1.opExtrude","CAP_EDGE",EDGE,{"disambiguationData":[OSD([sQuery(id+"F0.wireOp",EDGE,"E14.bottom")])],"isStart":false});
            var Q6;
            Q6=makeQuery(id+"F1.opExtrude","CAP_EDGE",EDGE,{"disambiguationData":[OSD([sQuery(id+"F0.wireOp",EDGE,"E14.top")])],"isStart":false});
            var Q7;
            {var subQ0=sQuery(id+"F0.wireOp",EDGE,"E14.right");var subQ1=sQuery(id+"F0.wireOp",EDGE,"E14.top");Q7=makeQuery(id+"F4.opFillet","BLEND_EDGE",EDGE,{"blendedFrom":[makeQuery(id+"F1.opExtrude","SWEPT_EDGE",EDGE,{"disambiguationData":[OSD([subQ1,subQ0])]}),makeQuery(id+"F1.opExtrude","CAP_FACE",FACE,{"disambiguationData":[OSD([sQuery(id+"F0.wireOp",EDGE,"E0.bottom"),sQuery(id+"F0.wireOp",EDGE,"E5.bottom"),sQuery(id+"F0.wireOp",EDGE,"E5.top"),sQuery(id+"F0.wireOp",EDGE,"E5.left"),sQuery(id+"F0.wireOp",EDGE,"E5.right"),sQuery(id+"F0.wireOp",EDGE,"E6.bottom"),sQuery(id+"F0.wireOp",EDGE,"E6.top"),sQuery(id+"F0.wireOp",EDGE,"E6.left"),sQuery(id+"F0.wireOp",EDGE,"E6.right"),sQuery(id+"F0.wireOp",EDGE,"E7.bottom"),sQuery(id+"F0.wireOp",EDGE,"E7.top"),sQuery(id+"F0.wireOp",EDGE,"E7.left"),sQuery(id+"F0.wireOp",EDGE,"E7.right"),sQuery(id+"F0.wireOp",EDGE,"E8.bottom"),sQuery(id+"F0.wireOp",EDGE,"E8.top"),sQuery(id+"F0.wireOp",EDGE,"E8.left"),sQuery(id+"F0.wireOp",EDGE,"E8.right"),sQuery(id+"F0.wireOp",EDGE,"E9.bottom"),sQuery(id+"F0.wireOp",EDGE,"E9.top"),sQuery(id+"F0.wireOp",EDGE,"E9.left"),sQuery(id+"F0.wireOp",EDGE,"E9.right"),sQuery(id+"F0.wireOp",EDGE,"E10.bottom"),sQuery(id+"F0.wireOp",EDGE,"E10.top"),sQuery(id+"F0.wireOp",EDGE,"E10.left"),sQuery(id+"F0.wireOp",EDGE,"E10.right"),sQuery(id+"F0.wireOp",EDGE,"E11.bottom"),sQuery(id+"F0.wireOp",EDGE,"E11.top"),sQuery(id+"F0.wireOp",EDGE,"E11.left"),sQuery(id+"F0.wireOp",EDGE,"E11.right"),sQuery(id+"F0.wireOp",EDGE,"E12.bottom"),sQuery(id+"F0.wireOp",EDGE,"E12.top"),sQuery(id+"F0.wireOp",EDGE,"E12.left"),sQuery(id+"F0.wireOp",EDGE,"E12.right"),sQuery(id+"F0.wireOp",EDGE,"E13.bottom"),sQuery(id+"F0.wireOp",EDGE,"E13.top"),sQuery(id+"F0.wireOp",EDGE,"E13.left"),sQuery(id+"F0.wireOp",EDGE,"E13.right"),sQuery(id+"F0.wireOp",EDGE,"E14.bottom"),subQ1,sQuery(id+"F0.wireOp",EDGE,"E14.left"),subQ0,sQuery(id+"F0.wireOp",EDGE,"E15.bottom"),sQuery(id+"F0.wireOp",EDGE,"E15.top"),sQuery(id+"F0.wireOp",EDGE,"E15.left"),sQuery(id+"F0.wireOp",EDGE,"E15.right"),sQuery(id+"F0.wireOp",EDGE,"E16"),sQuery(id+"F0.wireOp",EDGE,"E17")])],"isStart":false})],"blendedInto":[makeQuery(id+"F1.opExtrude","CAP_FACE",FACE,{"disambiguationData":[OSD([sQuery(id+"F0.wireOp",EDGE,"E0.bottom"),sQuery(id+"F0.wireOp",EDGE,"E5.bottom"),sQuery(id+"F0.wireOp",EDGE,"E5.top"),sQuery(id+"F0.wireOp",EDGE,"E5.left"),sQuery(id+"F0.wireOp",EDGE,"E5.right"),sQuery(id+"F0.wireOp",EDGE,"E6.bottom"),sQuery(id+"F0.wireOp",EDGE,"E6.top"),sQuery(id+"F0.wireOp",EDGE,"E6.left"),sQuery(id+"F0.wireOp",EDGE,"E6.right"),sQuery(id+"F0.wireOp",EDGE,"E7.bottom"),sQuery(id+"F0.wireOp",EDGE,"E7.top"),sQuery(id+"F0.wireOp",EDGE,"E7.left"),sQuery(id+"F0.wireOp",EDGE,"E7.right"),sQuery(id+"F0.wireOp",EDGE,"E8.bottom"),sQuery(id+"F0.wireOp",EDGE,"E8.top"),sQuery(id+"F0.wireOp",EDGE,"E8.left"),sQuery(id+"F0.wireOp",EDGE,"E8.right"),sQuery(id+"F0.wireOp",EDGE,"E9.bottom"),sQuery(id+"F0.wireOp",EDGE,"E9.top"),sQuery(id+"F0.wireOp",EDGE,"E9.left"),sQuery(id+"F0.wireOp",EDGE,"E9.right"),sQuery(id+"F0.wireOp",EDGE,"E10.bottom"),sQuery(id+"F0.wireOp",EDGE,"E10.top"),sQuery(id+"F0.wireOp",EDGE,"E10.left"),sQuery(id+"F0.wireOp",EDGE,"E10.right"),sQuery(id+"F0.wireOp",EDGE,"E11.bottom"),sQuery(id+"F0.wireOp",EDGE,"E11.top"),sQuery(id+"F0.wireOp",EDGE,"E11.left"),sQuery(id+"F0.wireOp",EDGE,"E11.right"),sQuery(id+"F0.wireOp",EDGE,"E12.bottom"),sQuery(id+"F0.wireOp",EDGE,"E12.top"),sQuery(id+"F0.wireOp",EDGE,"E12.left"),sQuery(id+"F0.wireOp",EDGE,"E12.right"),sQuery(id+"F0.wireOp",EDGE,"E13.bottom"),sQuery(id+"F0.wireOp",EDGE,"E13.top"),sQuery(id+"F0.wireOp",EDGE,"E13.left"),sQuery(id+"F0.wireOp",EDGE,"E13.right"),sQuery(id+"F0.wireOp",EDGE,"E14.bottom"),subQ1,sQuery(id+"F0.wireOp",EDGE,"E14.left"),subQ0,sQuery(id+"F0.wireOp",EDGE,"E15.bottom"),sQuery(id+"F0.wireOp",EDGE,"E15.top"),sQuery(id+"F0.wireOp",EDGE,"E15.left"),sQuery(id+"F0.wireOp",EDGE,"E15.right"),sQuery(id+"F0.wireOp",EDGE,"E16"),sQuery(id+"F0.wireOp",EDGE,"E17")])],"isStart":false})]});}
            var Q8;
            Q8=makeQuery(id+"F1.opExtrude","CAP_EDGE",EDGE,{"disambiguationData":[OSD([sQuery(id+"F0.wireOp",EDGE,"E13.bottom")])],"isStart":false});
            var Q9;
            {var subQ0=sQuery(id+"F0.wireOp",EDGE,"E13.right");var subQ1=sQuery(id+"F0.wireOp",EDGE,"E13.top");Q9=makeQuery(id+"F4.opFillet","BLEND_EDGE",EDGE,{"blendedFrom":[makeQuery(id+"F1.opExtrude","SWEPT_EDGE",EDGE,{"disambiguationData":[OSD([subQ1,subQ0])]}),makeQuery(id+"F1.opExtrude","CAP_FACE",FACE,{"disambiguationData":[OSD([sQuery(id+"F0.wireOp",EDGE,"E0.bottom"),sQuery(id+"F0.wireOp",EDGE,"E5.bottom"),sQuery(id+"F0.wireOp",EDGE,"E5.top"),sQuery(id+"F0.wireOp",EDGE,"E5.left"),sQuery(id+"F0.wireOp",EDGE,"E5.right"),sQuery(id+"F0.wireOp",EDGE,"E6.bottom"),sQuery(id+"F0.wireOp",EDGE,"E6.top"),sQuery(id+"F0.wireOp",EDGE,"E6.left"),sQuery(id+"F0.wireOp",EDGE,"E6.right"),sQuery(id+"F0.wireOp",EDGE,"E7.bottom"),sQuery(id+"F0.wireOp",EDGE,"E7.top"),sQuery(id+"F0.wireOp",EDGE,"E7.left"),sQuery(id+"F0.wireOp",EDGE,"E7.right"),sQuery(id+"F0.wireOp",EDGE,"E8.bottom"),sQuery(id+"F0.wireOp",EDGE,"E8.top"),sQuery(id+"F0.wireOp",EDGE,"E8.left"),sQuery(id+"F0.wireOp",EDGE,"E8.right"),sQuery(id+"F0.wireOp",EDGE,"E9.bottom"),sQuery(id+"F0.wireOp",EDGE,"E9.top"),sQuery(id+"F0.wireOp",EDGE,"E9.left"),sQuery(id+"F0.wireOp",EDGE,"E9.right"),sQuery(id+"F0.wireOp",EDGE,"E10.bottom"),sQuery(id+"F0.wireOp",EDGE,"E10.top"),sQuery(id+"F0.wireOp",EDGE,"E10.left"),sQuery(id+"F0.wireOp",EDGE,"E10.right"),sQuery(id+"F0.wireOp",EDGE,"E11.bottom"),sQuery(id+"F0.wireOp",EDGE,"E11.top"),sQuery(id+"F0.wireOp",EDGE,"E11.left"),sQuery(id+"F0.wireOp",EDGE,"E11.right"),sQuery(id+"F0.wireOp",EDGE,"E12.bottom"),sQuery(id+"F0.wireOp",EDGE,"E12.top"),sQuery(id+"F0.wireOp",EDGE,"E12.left"),sQuery(id+"F0.wireOp",EDGE,"E12.right"),sQuery(id+"F0.wireOp",EDGE,"E13.bottom"),subQ1,sQuery(id+"F0.wireOp",EDGE,"E13.left"),subQ0,sQuery(id+"F0.wireOp",EDGE,"E14.bottom"),sQuery(id+"F0.wireOp",EDGE,"E14.top"),sQuery(id+"F0.wireOp",EDGE,"E14.left"),sQuery(id+"F0.wireOp",EDGE,"E14.right"),sQuery(id+"F0.wireOp",EDGE,"E15.bottom"),sQuery(id+"F0.wireOp",EDGE,"E15.top"),sQuery(id+"F0.wireOp",EDGE,"E15.left"),sQuery(id+"F0.wireOp",EDGE,"E15.right"),sQuery(id+"F0.wireOp",EDGE,"E16"),sQuery(id+"F0.wireOp",EDGE,"E17")])],"isStart":false})],"blendedInto":[makeQuery(id+"F1.opExtrude","CAP_FACE",FACE,{"disambiguationData":[OSD([sQuery(id+"F0.wireOp",EDGE,"E0.bottom"),sQuery(id+"F0.wireOp",EDGE,"E5.bottom"),sQuery(id+"F0.wireOp",EDGE,"E5.top"),sQuery(id+"F0.wireOp",EDGE,"E5.left"),sQuery(id+"F0.wireOp",EDGE,"E5.right"),sQuery(id+"F0.wireOp",EDGE,"E6.bottom"),sQuery(id+"F0.wireOp",EDGE,"E6.top"),sQuery(id+"F0.wireOp",EDGE,"E6.left"),sQuery(id+"F0.wireOp",EDGE,"E6.right"),sQuery(id+"F0.wireOp",EDGE,"E7.bottom"),sQuery(id+"F0.wireOp",EDGE,"E7.top"),sQuery(id+"F0.wireOp",EDGE,"E7.left"),sQuery(id+"F0.wireOp",EDGE,"E7.right"),sQuery(id+"F0.wireOp",EDGE,"E8.bottom"),sQuery(id+"F0.wireOp",EDGE,"E8.top"),sQuery(id+"F0.wireOp",EDGE,"E8.left"),sQuery(id+"F0.wireOp",EDGE,"E8.right"),sQuery(id+"F0.wireOp",EDGE,"E9.bottom"),sQuery(id+"F0.wireOp",EDGE,"E9.top"),sQuery(id+"F0.wireOp",EDGE,"E9.left"),sQuery(id+"F0.wireOp",EDGE,"E9.right"),sQuery(id+"F0.wireOp",EDGE,"E10.bottom"),sQuery(id+"F0.wireOp",EDGE,"E10.top"),sQuery(id+"F0.wireOp",EDGE,"E10.left"),sQuery(id+"F0.wireOp",EDGE,"E10.right"),sQuery(id+"F0.wireOp",EDGE,"E11.bottom"),sQuery(id+"F0.wireOp",EDGE,"E11.top"),sQuery(id+"F0.wireOp",EDGE,"E11.left"),sQuery(id+"F0.wireOp",EDGE,"E11.right"),sQuery(id+"F0.wireOp",EDGE,"E12.bottom"),sQuery(id+"F0.wireOp",EDGE,"E12.top"),sQuery(id+"F0.wireOp",EDGE,"E12.left"),sQuery(id+"F0.wireOp",EDGE,"E12.right"),sQuery(id+"F0.wireOp",EDGE,"E13.bottom"),subQ1,sQuery(id+"F0.wireOp",EDGE,"E13.left"),subQ0,sQuery(id+"F0.wireOp",EDGE,"E14.bottom"),sQuery(id+"F0.wireOp",EDGE,"E14.top"),sQuery(id+"F0.wireOp",EDGE,"E14.left"),sQuery(id+"F0.wireOp",EDGE,"E14.right"),sQuery(id+"F0.wireOp",EDGE,"E15.bottom"),sQuery(id+"F0.wireOp",EDGE,"E15.top"),sQuery(id+"F0.wireOp",EDGE,"E15.left"),sQuery(id+"F0.wireOp",EDGE,"E15.right"),sQuery(id+"F0.wireOp",EDGE,"E16"),sQuery(id+"F0.wireOp",EDGE,"E17")])],"isStart":false})]});}
            var Q10;
            {var subQ0=sQuery(id+"F0.wireOp",EDGE,"E13.left");var subQ1=sQuery(id+"F0.wireOp",EDGE,"E13.bottom");Q10=makeQuery(id+"F4.opFillet","BLEND_EDGE",EDGE,{"blendedFrom":[makeQuery(id+"F1.opExtrude","SWEPT_EDGE",EDGE,{"disambiguationData":[OSD([subQ1,subQ0])]}),makeQuery(id+"F1.opExtrude","CAP_FACE",FACE,{"disambiguationData":[OSD([sQuery(id+"F0.wireOp",EDGE,"E0.bottom"),sQuery(id+"F0.wireOp",EDGE,"E5.bottom"),sQuery(id+"F0.wireOp",EDGE,"E5.top"),sQuery(id+"F0.wireOp",EDGE,"E5.left"),sQuery(id+"F0.wireOp",EDGE,"E5.right"),sQuery(id+"F0.wireOp",EDGE,"E6.bottom"),sQuery(id+"F0.wireOp",EDGE,"E6.top"),sQuery(id+"F0.wireOp",EDGE,"E6.left"),sQuery(id+"F0.wireOp",EDGE,"E6.right"),sQuery(id+"F0.wireOp",EDGE,"E7.bottom"),sQuery(id+"F0.wireOp",EDGE,"E7.top"),sQuery(id+"F0.wireOp",EDGE,"E7.left"),sQuery(id+"F0.wireOp",EDGE,"E7.right"),sQuery(id+"F0.wireOp",EDGE,"E8.bottom"),sQuery(id+"F0.wireOp",EDGE,"E8.top"),sQuery(id+"F0.wireOp",EDGE,"E8.left"),sQuery(id+"F0.wireOp",EDGE,"E8.right"),sQuery(id+"F0.wireOp",EDGE,"E9.bottom"),sQuery(id+"F0.wireOp",EDGE,"E9.top"),sQuery(id+"F0.wireOp",EDGE,"E9.left"),sQuery(id+"F0.wireOp",EDGE,"E9.right"),sQuery(id+"F0.wireOp",EDGE,"E10.bottom"),sQuery(id+"F0.wireOp",EDGE,"E10.top"),sQuery(id+"F0.wireOp",EDGE,"E10.left"),sQuery(id+"F0.wireOp",EDGE,"E10.right"),sQuery(id+"F0.wireOp",EDGE,"E11.bottom"),sQuery(id+"F0.wireOp",EDGE,"E11.top"),sQuery(id+"F0.wireOp",EDGE,"E11.left"),sQuery(id+"F0.wireOp",EDGE,"E11.right"),sQuery(id+"F0.wireOp",EDGE,"E12.bottom"),sQuery(id+"F0.wireOp",EDGE,"E12.top"),sQuery(id+"F0.wireOp",EDGE,"E12.left"),sQuery(id+"F0.wireOp",EDGE,"E12.right"),subQ1,sQuery(id+"F0.wireOp",EDGE,"E13.top"),subQ0,sQuery(id+"F0.wireOp",EDGE,"E13.right"),sQuery(id+"F0.wireOp",EDGE,"E14.bottom"),sQuery(id+"F0.wireOp",EDGE,"E14.top"),sQuery(id+"F0.wireOp",EDGE,"E14.left"),sQuery(id+"F0.wireOp",EDGE,"E14.right"),sQuery(id+"F0.wireOp",EDGE,"E15.bottom"),sQuery(id+"F0.wireOp",EDGE,"E15.top"),sQuery(id+"F0.wireOp",EDGE,"E15.left"),sQuery(id+"F0.wireOp",EDGE,"E15.right"),sQuery(id+"F0.wireOp",EDGE,"E16"),sQuery(id+"F0.wireOp",EDGE,"E17")])],"isStart":false})],"blendedInto":[makeQuery(id+"F1.opExtrude","CAP_FACE",FACE,{"disambiguationData":[OSD([sQuery(id+"F0.wireOp",EDGE,"E0.bottom"),sQuery(id+"F0.wireOp",EDGE,"E5.bottom"),sQuery(id+"F0.wireOp",EDGE,"E5.top"),sQuery(id+"F0.wireOp",EDGE,"E5.left"),sQuery(id+"F0.wireOp",EDGE,"E5.right"),sQuery(id+"F0.wireOp",EDGE,"E6.bottom"),sQuery(id+"F0.wireOp",EDGE,"E6.top"),sQuery(id+"F0.wireOp",EDGE,"E6.left"),sQuery(id+"F0.wireOp",EDGE,"E6.right"),sQuery(id+"F0.wireOp",EDGE,"E7.bottom"),sQuery(id+"F0.wireOp",EDGE,"E7.top"),sQuery(id+"F0.wireOp",EDGE,"E7.left"),sQuery(id+"F0.wireOp",EDGE,"E7.right"),sQuery(id+"F0.wireOp",EDGE,"E8.bottom"),sQuery(id+"F0.wireOp",EDGE,"E8.top"),sQuery(id+"F0.wireOp",EDGE,"E8.left"),sQuery(id+"F0.wireOp",EDGE,"E8.right"),sQuery(id+"F0.wireOp",EDGE,"E9.bottom"),sQuery(id+"F0.wireOp",EDGE,"E9.top"),sQuery(id+"F0.wireOp",EDGE,"E9.left"),sQuery(id+"F0.wireOp",EDGE,"E9.right"),sQuery(id+"F0.wireOp",EDGE,"E10.bottom"),sQuery(id+"F0.wireOp",EDGE,"E10.top"),sQuery(id+"F0.wireOp",EDGE,"E10.left"),sQuery(id+"F0.wireOp",EDGE,"E10.right"),sQuery(id+"F0.wireOp",EDGE,"E11.bottom"),sQuery(id+"F0.wireOp",EDGE,"E11.top"),sQuery(id+"F0.wireOp",EDGE,"E11.left"),sQuery(id+"F0.wireOp",EDGE,"E11.right"),sQuery(id+"F0.wireOp",EDGE,"E12.bottom"),sQuery(id+"F0.wireOp",EDGE,"E12.top"),sQuery(id+"F0.wireOp",EDGE,"E12.left"),sQuery(id+"F0.wireOp",EDGE,"E12.right"),subQ1,sQuery(id+"F0.wireOp",EDGE,"E13.top"),subQ0,sQuery(id+"F0.wireOp",EDGE,"E13.right"),sQuery(id+"F0.wireOp",EDGE,"E14.bottom"),sQuery(id+"F0.wireOp",EDGE,"E14.top"),sQuery(id+"F0.wireOp",EDGE,"E14.left"),sQuery(id+"F0.wireOp",EDGE,"E14.right"),sQuery(id+"F0.wireOp",EDGE,"E15.bottom"),sQuery(id+"F0.wireOp",EDGE,"E15.top"),sQuery(id+"F0.wireOp",EDGE,"E15.left"),sQuery(id+"F0.wireOp",EDGE,"E15.right"),sQuery(id+"F0.wireOp",EDGE,"E16"),sQuery(id+"F0.wireOp",EDGE,"E17")])],"isStart":false})]});}
            var Q11;
            Q11=makeQuery(id+"F1.opExtrude","CAP_EDGE",EDGE,{"disambiguationData":[OSD([sQuery(id+"F0.wireOp",EDGE,"E13.top")])],"isStart":false});
            var Q12;
            Q12=makeQuery(id+"F1.opExtrude","CAP_EDGE",EDGE,{"disambiguationData":[OSD([sQuery(id+"F0.wireOp",EDGE,"E11.bottom")])],"isStart":false});
            var Q13;
            {var subQ0=sQuery(id+"F0.wireOp",EDGE,"E11.left");var subQ1=sQuery(id+"F0.wireOp",EDGE,"E11.bottom");Q13=makeQuery(id+"F4.opFillet","BLEND_EDGE",EDGE,{"blendedFrom":[makeQuery(id+"F1.opExtrude","SWEPT_EDGE",EDGE,{"disambiguationData":[OSD([subQ1,subQ0])]}),makeQuery(id+"F1.opExtrude","CAP_FACE",FACE,{"disambiguationData":[OSD([sQuery(id+"F0.wireOp",EDGE,"E0.bottom"),sQuery(id+"F0.wireOp",EDGE,"E5.bottom"),sQuery(id+"F0.wireOp",EDGE,"E5.top"),sQuery(id+"F0.wireOp",EDGE,"E5.left"),sQuery(id+"F0.wireOp",EDGE,"E5.right"),sQuery(id+"F0.wireOp",EDGE,"E6.bottom"),sQuery(id+"F0.wireOp",EDGE,"E6.top"),sQuery(id+"F0.wireOp",EDGE,"E6.left"),sQuery(id+"F0.wireOp",EDGE,"E6.right"),sQuery(id+"F0.wireOp",EDGE,"E7.bottom"),sQuery(id+"F0.wireOp",EDGE,"E7.top"),sQuery(id+"F0.wireOp",EDGE,"E7.left"),sQuery(id+"F0.wireOp",EDGE,"E7.right"),sQuery(id+"F0.wireOp",EDGE,"E8.bottom"),sQuery(id+"F0.wireOp",EDGE,"E8.top"),sQuery(id+"F0.wireOp",EDGE,"E8.left"),sQuery(id+"F0.wireOp",EDGE,"E8.right"),sQuery(id+"F0.wireOp",EDGE,"E9.bottom"),sQuery(id+"F0.wireOp",EDGE,"E9.top"),sQuery(id+"F0.wireOp",EDGE,"E9.left"),sQuery(id+"F0.wireOp",EDGE,"E9.right"),sQuery(id+"F0.wireOp",EDGE,"E10.bottom"),sQuery(id+"F0.wireOp",EDGE,"E10.top"),sQuery(id+"F0.wireOp",EDGE,"E10.left"),sQuery(id+"F0.wireOp",EDGE,"E10.right"),subQ1,sQuery(id+"F0.wireOp",EDGE,"E11.top"),subQ0,sQuery(id+"F0.wireOp",EDGE,"E11.right"),sQuery(id+"F0.wireOp",EDGE,"E12.bottom"),sQuery(id+"F0.wireOp",EDGE,"E12.top"),sQuery(id+"F0.wireOp",EDGE,"E12.left"),sQuery(id+"F0.wireOp",EDGE,"E12.right"),sQuery(id+"F0.wireOp",EDGE,"E13.bottom"),sQuery(id+"F0.wireOp",EDGE,"E13.top"),sQuery(id+"F0.wireOp",EDGE,"E13.left"),sQuery(id+"F0.wireOp",EDGE,"E13.right"),sQuery(id+"F0.wireOp",EDGE,"E14.bottom"),sQuery(id+"F0.wireOp",EDGE,"E14.top"),sQuery(id+"F0.wireOp",EDGE,"E14.left"),sQuery(id+"F0.wireOp",EDGE,"E14.right"),sQuery(id+"F0.wireOp",EDGE,"E15.bottom"),sQuery(id+"F0.wireOp",EDGE,"E15.top"),sQuery(id+"F0.wireOp",EDGE,"E15.left"),sQuery(id+"F0.wireOp",EDGE,"E15.right"),sQuery(id+"F0.wireOp",EDGE,"E16"),sQuery(id+"F0.wireOp",EDGE,"E17")])],"isStart":false})],"blendedInto":[makeQuery(id+"F1.opExtrude","CAP_FACE",FACE,{"disambiguationData":[OSD([sQuery(id+"F0.wireOp",EDGE,"E0.bottom"),sQuery(id+"F0.wireOp",EDGE,"E5.bottom"),sQuery(id+"F0.wireOp",EDGE,"E5.top"),sQuery(id+"F0.wireOp",EDGE,"E5.left"),sQuery(id+"F0.wireOp",EDGE,"E5.right"),sQuery(id+"F0.wireOp",EDGE,"E6.bottom"),sQuery(id+"F0.wireOp",EDGE,"E6.top"),sQuery(id+"F0.wireOp",EDGE,"E6.left"),sQuery(id+"F0.wireOp",EDGE,"E6.right"),sQuery(id+"F0.wireOp",EDGE,"E7.bottom"),sQuery(id+"F0.wireOp",EDGE,"E7.top"),sQuery(id+"F0.wireOp",EDGE,"E7.left"),sQuery(id+"F0.wireOp",EDGE,"E7.right"),sQuery(id+"F0.wireOp",EDGE,"E8.bottom"),sQuery(id+"F0.wireOp",EDGE,"E8.top"),sQuery(id+"F0.wireOp",EDGE,"E8.left"),sQuery(id+"F0.wireOp",EDGE,"E8.right"),sQuery(id+"F0.wireOp",EDGE,"E9.bottom"),sQuery(id+"F0.wireOp",EDGE,"E9.top"),sQuery(id+"F0.wireOp",EDGE,"E9.left"),sQuery(id+"F0.wireOp",EDGE,"E9.right"),sQuery(id+"F0.wireOp",EDGE,"E10.bottom"),sQuery(id+"F0.wireOp",EDGE,"E10.top"),sQuery(id+"F0.wireOp",EDGE,"E10.left"),sQuery(id+"F0.wireOp",EDGE,"E10.right"),subQ1,sQuery(id+"F0.wireOp",EDGE,"E11.top"),subQ0,sQuery(id+"F0.wireOp",EDGE,"E11.right"),sQuery(id+"F0.wireOp",EDGE,"E12.bottom"),sQuery(id+"F0.wireOp",EDGE,"E12.top"),sQuery(id+"F0.wireOp",EDGE,"E12.left"),sQuery(id+"F0.wireOp",EDGE,"E12.right"),sQuery(id+"F0.wireOp",EDGE,"E13.bottom"),sQuery(id+"F0.wireOp",EDGE,"E13.top"),sQuery(id+"F0.wireOp",EDGE,"E13.left"),sQuery(id+"F0.wireOp",EDGE,"E13.right"),sQuery(id+"F0.wireOp",EDGE,"E14.bottom"),sQuery(id+"F0.wireOp",EDGE,"E14.top"),sQuery(id+"F0.wireOp",EDGE,"E14.left"),sQuery(id+"F0.wireOp",EDGE,"E14.right"),sQuery(id+"F0.wireOp",EDGE,"E15.bottom"),sQuery(id+"F0.wireOp",EDGE,"E15.top"),sQuery(id+"F0.wireOp",EDGE,"E15.left"),sQuery(id+"F0.wireOp",EDGE,"E15.right"),sQuery(id+"F0.wireOp",EDGE,"E16"),sQuery(id+"F0.wireOp",EDGE,"E17")])],"isStart":false})]});}
            var Q14;
            Q14=makeQuery(id+"F1.opExtrude","CAP_EDGE",EDGE,{"disambiguationData":[OSD([sQuery(id+"F0.wireOp",EDGE,"E11.top")])],"isStart":false});
            var Q15;
            {var subQ0=sQuery(id+"F0.wireOp",EDGE,"E11.right");var subQ1=sQuery(id+"F0.wireOp",EDGE,"E11.top");Q15=makeQuery(id+"F4.opFillet","BLEND_EDGE",EDGE,{"blendedFrom":[makeQuery(id+"F1.opExtrude","SWEPT_EDGE",EDGE,{"disambiguationData":[OSD([subQ1,subQ0])]}),makeQuery(id+"F1.opExtrude","CAP_FACE",FACE,{"disambiguationData":[OSD([sQuery(id+"F0.wireOp",EDGE,"E0.bottom"),sQuery(id+"F0.wireOp",EDGE,"E5.bottom"),sQuery(id+"F0.wireOp",EDGE,"E5.top"),sQuery(id+"F0.wireOp",EDGE,"E5.left"),sQuery(id+"F0.wireOp",EDGE,"E5.right"),sQuery(id+"F0.wireOp",EDGE,"E6.bottom"),sQuery(id+"F0.wireOp",EDGE,"E6.top"),sQuery(id+"F0.wireOp",EDGE,"E6.left"),sQuery(id+"F0.wireOp",EDGE,"E6.right"),sQuery(id+"F0.wireOp",EDGE,"E7.bottom"),sQuery(id+"F0.wireOp",EDGE,"E7.top"),sQuery(id+"F0.wireOp",EDGE,"E7.left"),sQuery(id+"F0.wireOp",EDGE,"E7.right"),sQuery(id+"F0.wireOp",EDGE,"E8.bottom"),sQuery(id+"F0.wireOp",EDGE,"E8.top"),sQuery(id+"F0.wireOp",EDGE,"E8.left"),sQuery(id+"F0.wireOp",EDGE,"E8.right"),sQuery(id+"F0.wireOp",EDGE,"E9.bottom"),sQuery(id+"F0.wireOp",EDGE,"E9.top"),sQuery(id+"F0.wireOp",EDGE,"E9.left"),sQuery(id+"F0.wireOp",EDGE,"E9.right"),sQuery(id+"F0.wireOp",EDGE,"E10.bottom"),sQuery(id+"F0.wireOp",EDGE,"E10.top"),sQuery(id+"F0.wireOp",EDGE,"E10.left"),sQuery(id+"F0.wireOp",EDGE,"E10.right"),sQuery(id+"F0.wireOp",EDGE,"E11.bottom"),subQ1,sQuery(id+"F0.wireOp",EDGE,"E11.left"),subQ0,sQuery(id+"F0.wireOp",EDGE,"E12.bottom"),sQuery(id+"F0.wireOp",EDGE,"E12.top"),sQuery(id+"F0.wireOp",EDGE,"E12.left"),sQuery(id+"F0.wireOp",EDGE,"E12.right"),sQuery(id+"F0.wireOp",EDGE,"E13.bottom"),sQuery(id+"F0.wireOp",EDGE,"E13.top"),sQuery(id+"F0.wireOp",EDGE,"E13.left"),sQuery(id+"F0.wireOp",EDGE,"E13.right"),sQuery(id+"F0.wireOp",EDGE,"E14.bottom"),sQuery(id+"F0.wireOp",EDGE,"E14.top"),sQuery(id+"F0.wireOp",EDGE,"E14.left"),sQuery(id+"F0.wireOp",EDGE,"E14.right"),sQuery(id+"F0.wireOp",EDGE,"E15.bottom"),sQuery(id+"F0.wireOp",EDGE,"E15.top"),sQuery(id+"F0.wireOp",EDGE,"E15.left"),sQuery(id+"F0.wireOp",EDGE,"E15.right"),sQuery(id+"F0.wireOp",EDGE,"E16"),sQuery(id+"F0.wireOp",EDGE,"E17")])],"isStart":false})],"blendedInto":[makeQuery(id+"F1.opExtrude","CAP_FACE",FACE,{"disambiguationData":[OSD([sQuery(id+"F0.wireOp",EDGE,"E0.bottom"),sQuery(id+"F0.wireOp",EDGE,"E5.bottom"),sQuery(id+"F0.wireOp",EDGE,"E5.top"),sQuery(id+"F0.wireOp",EDGE,"E5.left"),sQuery(id+"F0.wireOp",EDGE,"E5.right"),sQuery(id+"F0.wireOp",EDGE,"E6.bottom"),sQuery(id+"F0.wireOp",EDGE,"E6.top"),sQuery(id+"F0.wireOp",EDGE,"E6.left"),sQuery(id+"F0.wireOp",EDGE,"E6.right"),sQuery(id+"F0.wireOp",EDGE,"E7.bottom"),sQuery(id+"F0.wireOp",EDGE,"E7.top"),sQuery(id+"F0.wireOp",EDGE,"E7.left"),sQuery(id+"F0.wireOp",EDGE,"E7.right"),sQuery(id+"F0.wireOp",EDGE,"E8.bottom"),sQuery(id+"F0.wireOp",EDGE,"E8.top"),sQuery(id+"F0.wireOp",EDGE,"E8.left"),sQuery(id+"F0.wireOp",EDGE,"E8.right"),sQuery(id+"F0.wireOp",EDGE,"E9.bottom"),sQuery(id+"F0.wireOp",EDGE,"E9.top"),sQuery(id+"F0.wireOp",EDGE,"E9.left"),sQuery(id+"F0.wireOp",EDGE,"E9.right"),sQuery(id+"F0.wireOp",EDGE,"E10.bottom"),sQuery(id+"F0.wireOp",EDGE,"E10.top"),sQuery(id+"F0.wireOp",EDGE,"E10.left"),sQuery(id+"F0.wireOp",EDGE,"E10.right"),sQuery(id+"F0.wireOp",EDGE,"E11.bottom"),subQ1,sQuery(id+"F0.wireOp",EDGE,"E11.left"),subQ0,sQuery(id+"F0.wireOp",EDGE,"E12.bottom"),sQuery(id+"F0.wireOp",EDGE,"E12.top"),sQuery(id+"F0.wireOp",EDGE,"E12.left"),sQuery(id+"F0.wireOp",EDGE,"E12.right"),sQuery(id+"F0.wireOp",EDGE,"E13.bottom"),sQuery(id+"F0.wireOp",EDGE,"E13.top"),sQuery(id+"F0.wireOp",EDGE,"E13.left"),sQuery(id+"F0.wireOp",EDGE,"E13.right"),sQuery(id+"F0.wireOp",EDGE,"E14.bottom"),sQuery(id+"F0.wireOp",EDGE,"E14.top"),sQuery(id+"F0.wireOp",EDGE,"E14.left"),sQuery(id+"F0.wireOp",EDGE,"E14.right"),sQuery(id+"F0.wireOp",EDGE,"E15.bottom"),sQuery(id+"F0.wireOp",EDGE,"E15.top"),sQuery(id+"F0.wireOp",EDGE,"E15.left"),sQuery(id+"F0.wireOp",EDGE,"E15.right"),sQuery(id+"F0.wireOp",EDGE,"E16"),sQuery(id+"F0.wireOp",EDGE,"E17")])],"isStart":false})]});}
            var Q16;
            Q16=makeQuery(id+"F1.opExtrude","CAP_EDGE",EDGE,{"disambiguationData":[OSD([sQuery(id+"F0.wireOp",EDGE,"E10.bottom")])],"isStart":false});
            var Q17;
            {var subQ0=sQuery(id+"F0.wireOp",EDGE,"E10.right");var subQ1=sQuery(id+"F0.wireOp",EDGE,"E10.top");Q17=makeQuery(id+"F4.opFillet","BLEND_EDGE",EDGE,{"blendedFrom":[makeQuery(id+"F1.opExtrude","SWEPT_EDGE",EDGE,{"disambiguationData":[OSD([subQ1,subQ0])]}),makeQuery(id+"F1.opExtrude","CAP_FACE",FACE,{"disambiguationData":[OSD([sQuery(id+"F0.wireOp",EDGE,"E0.bottom"),sQuery(id+"F0.wireOp",EDGE,"E5.bottom"),sQuery(id+"F0.wireOp",EDGE,"E5.top"),sQuery(id+"F0.wireOp",EDGE,"E5.left"),sQuery(id+"F0.wireOp",EDGE,"E5.right"),sQuery(id+"F0.wireOp",EDGE,"E6.bottom"),sQuery(id+"F0.wireOp",EDGE,"E6.top"),sQuery(id+"F0.wireOp",EDGE,"E6.left"),sQuery(id+"F0.wireOp",EDGE,"E6.right"),sQuery(id+"F0.wireOp",EDGE,"E7.bottom"),sQuery(id+"F0.wireOp",EDGE,"E7.top"),sQuery(id+"F0.wireOp",EDGE,"E7.left"),sQuery(id+"F0.wireOp",EDGE,"E7.right"),sQuery(id+"F0.wireOp",EDGE,"E8.bottom"),sQuery(id+"F0.wireOp",EDGE,"E8.top"),sQuery(id+"F0.wireOp",EDGE,"E8.left"),sQuery(id+"F0.wireOp",EDGE,"E8.right"),sQuery(id+"F0.wireOp",EDGE,"E9.bottom"),sQuery(id+"F0.wireOp",EDGE,"E9.top"),sQuery(id+"F0.wireOp",EDGE,"E9.left"),sQuery(id+"F0.wireOp",EDGE,"E9.right"),sQuery(id+"F0.wireOp",EDGE,"E10.bottom"),subQ1,sQuery(id+"F0.wireOp",EDGE,"E10.left"),subQ0,sQuery(id+"F0.wireOp",EDGE,"E11.bottom"),sQuery(id+"F0.wireOp",EDGE,"E11.top"),sQuery(id+"F0.wireOp",EDGE,"E11.left"),sQuery(id+"F0.wireOp",EDGE,"E11.right"),sQuery(id+"F0.wireOp",EDGE,"E12.bottom"),sQuery(id+"F0.wireOp",EDGE,"E12.top"),sQuery(id+"F0.wireOp",EDGE,"E12.left"),sQuery(id+"F0.wireOp",EDGE,"E12.right"),sQuery(id+"F0.wireOp",EDGE,"E13.bottom"),sQuery(id+"F0.wireOp",EDGE,"E13.top"),sQuery(id+"F0.wireOp",EDGE,"E13.left"),sQuery(id+"F0.wireOp",EDGE,"E13.right"),sQuery(id+"F0.wireOp",EDGE,"E14.bottom"),sQuery(id+"F0.wireOp",EDGE,"E14.top"),sQuery(id+"F0.wireOp",EDGE,"E14.left"),sQuery(id+"F0.wireOp",EDGE,"E14.right"),sQuery(id+"F0.wireOp",EDGE,"E15.bottom"),sQuery(id+"F0.wireOp",EDGE,"E15.top"),sQuery(id+"F0.wireOp",EDGE,"E15.left"),sQuery(id+"F0.wireOp",EDGE,"E15.right"),sQuery(id+"F0.wireOp",EDGE,"E16"),sQuery(id+"F0.wireOp",EDGE,"E17")])],"isStart":false})],"blendedInto":[makeQuery(id+"F1.opExtrude","CAP_FACE",FACE,{"disambiguationData":[OSD([sQuery(id+"F0.wireOp",EDGE,"E0.bottom"),sQuery(id+"F0.wireOp",EDGE,"E5.bottom"),sQuery(id+"F0.wireOp",EDGE,"E5.top"),sQuery(id+"F0.wireOp",EDGE,"E5.left"),sQuery(id+"F0.wireOp",EDGE,"E5.right"),sQuery(id+"F0.wireOp",EDGE,"E6.bottom"),sQuery(id+"F0.wireOp",EDGE,"E6.top"),sQuery(id+"F0.wireOp",EDGE,"E6.left"),sQuery(id+"F0.wireOp",EDGE,"E6.right"),sQuery(id+"F0.wireOp",EDGE,"E7.bottom"),sQuery(id+"F0.wireOp",EDGE,"E7.top"),sQuery(id+"F0.wireOp",EDGE,"E7.left"),sQuery(id+"F0.wireOp",EDGE,"E7.right"),sQuery(id+"F0.wireOp",EDGE,"E8.bottom"),sQuery(id+"F0.wireOp",EDGE,"E8.top"),sQuery(id+"F0.wireOp",EDGE,"E8.left"),sQuery(id+"F0.wireOp",EDGE,"E8.right"),sQuery(id+"F0.wireOp",EDGE,"E9.bottom"),sQuery(id+"F0.wireOp",EDGE,"E9.top"),sQuery(id+"F0.wireOp",EDGE,"E9.left"),sQuery(id+"F0.wireOp",EDGE,"E9.right"),sQuery(id+"F0.wireOp",EDGE,"E10.bottom"),subQ1,sQuery(id+"F0.wireOp",EDGE,"E10.left"),subQ0,sQuery(id+"F0.wireOp",EDGE,"E11.bottom"),sQuery(id+"F0.wireOp",EDGE,"E11.top"),sQuery(id+"F0.wireOp",EDGE,"E11.left"),sQuery(id+"F0.wireOp",EDGE,"E11.right"),sQuery(id+"F0.wireOp",EDGE,"E12.bottom"),sQuery(id+"F0.wireOp",EDGE,"E12.top"),sQuery(id+"F0.wireOp",EDGE,"E12.left"),sQuery(id+"F0.wireOp",EDGE,"E12.right"),sQuery(id+"F0.wireOp",EDGE,"E13.bottom"),sQuery(id+"F0.wireOp",EDGE,"E13.top"),sQuery(id+"F0.wireOp",EDGE,"E13.left"),sQuery(id+"F0.wireOp",EDGE,"E13.right"),sQuery(id+"F0.wireOp",EDGE,"E14.bottom"),sQuery(id+"F0.wireOp",EDGE,"E14.top"),sQuery(id+"F0.wireOp",EDGE,"E14.left"),sQuery(id+"F0.wireOp",EDGE,"E14.right"),sQuery(id+"F0.wireOp",EDGE,"E15.bottom"),sQuery(id+"F0.wireOp",EDGE,"E15.top"),sQuery(id+"F0.wireOp",EDGE,"E15.left"),sQuery(id+"F0.wireOp",EDGE,"E15.right"),sQuery(id+"F0.wireOp",EDGE,"E16"),sQuery(id+"F0.wireOp",EDGE,"E17")])],"isStart":false})]});}
            var Q18;
            {var subQ0=sQuery(id+"F0.wireOp",EDGE,"E10.left");var subQ1=sQuery(id+"F0.wireOp",EDGE,"E10.bottom");Q18=makeQuery(id+"F4.opFillet","BLEND_EDGE",EDGE,{"blendedFrom":[makeQuery(id+"F1.opExtrude","SWEPT_EDGE",EDGE,{"disambiguationData":[OSD([subQ1,subQ0])]}),makeQuery(id+"F1.opExtrude","CAP_FACE",FACE,{"disambiguationData":[OSD([sQuery(id+"F0.wireOp",EDGE,"E0.bottom"),sQuery(id+"F0.wireOp",EDGE,"E5.bottom"),sQuery(id+"F0.wireOp",EDGE,"E5.top"),sQuery(id+"F0.wireOp",EDGE,"E5.left"),sQuery(id+"F0.wireOp",EDGE,"E5.right"),sQuery(id+"F0.wireOp",EDGE,"E6.bottom"),sQuery(id+"F0.wireOp",EDGE,"E6.top"),sQuery(id+"F0.wireOp",EDGE,"E6.left"),sQuery(id+"F0.wireOp",EDGE,"E6.right"),sQuery(id+"F0.wireOp",EDGE,"E7.bottom"),sQuery(id+"F0.wireOp",EDGE,"E7.top"),sQuery(id+"F0.wireOp",EDGE,"E7.left"),sQuery(id+"F0.wireOp",EDGE,"E7.right"),sQuery(id+"F0.wireOp",EDGE,"E8.bottom"),sQuery(id+"F0.wireOp",EDGE,"E8.top"),sQuery(id+"F0.wireOp",EDGE,"E8.left"),sQuery(id+"F0.wireOp",EDGE,"E8.right"),sQuery(id+"F0.wireOp",EDGE,"E9.bottom"),sQuery(id+"F0.wireOp",EDGE,"E9.top"),sQuery(id+"F0.wireOp",EDGE,"E9.left"),sQuery(id+"F0.wireOp",EDGE,"E9.right"),subQ1,sQuery(id+"F0.wireOp",EDGE,"E10.top"),subQ0,sQuery(id+"F0.wireOp",EDGE,"E10.right"),sQuery(id+"F0.wireOp",EDGE,"E11.bottom"),sQuery(id+"F0.wireOp",EDGE,"E11.top"),sQuery(id+"F0.wireOp",EDGE,"E11.left"),sQuery(id+"F0.wireOp",EDGE,"E11.right"),sQuery(id+"F0.wireOp",EDGE,"E12.bottom"),sQuery(id+"F0.wireOp",EDGE,"E12.top"),sQuery(id+"F0.wireOp",EDGE,"E12.left"),sQuery(id+"F0.wireOp",EDGE,"E12.right"),sQuery(id+"F0.wireOp",EDGE,"E13.bottom"),sQuery(id+"F0.wireOp",EDGE,"E13.top"),sQuery(id+"F0.wireOp",EDGE,"E13.left"),sQuery(id+"F0.wireOp",EDGE,"E13.right"),sQuery(id+"F0.wireOp",EDGE,"E14.bottom"),sQuery(id+"F0.wireOp",EDGE,"E14.top"),sQuery(id+"F0.wireOp",EDGE,"E14.left"),sQuery(id+"F0.wireOp",EDGE,"E14.right"),sQuery(id+"F0.wireOp",EDGE,"E15.bottom"),sQuery(id+"F0.wireOp",EDGE,"E15.top"),sQuery(id+"F0.wireOp",EDGE,"E15.left"),sQuery(id+"F0.wireOp",EDGE,"E15.right"),sQuery(id+"F0.wireOp",EDGE,"E16"),sQuery(id+"F0.wireOp",EDGE,"E17")])],"isStart":false})],"blendedInto":[makeQuery(id+"F1.opExtrude","CAP_FACE",FACE,{"disambiguationData":[OSD([sQuery(id+"F0.wireOp",EDGE,"E0.bottom"),sQuery(id+"F0.wireOp",EDGE,"E5.bottom"),sQuery(id+"F0.wireOp",EDGE,"E5.top"),sQuery(id+"F0.wireOp",EDGE,"E5.left"),sQuery(id+"F0.wireOp",EDGE,"E5.right"),sQuery(id+"F0.wireOp",EDGE,"E6.bottom"),sQuery(id+"F0.wireOp",EDGE,"E6.top"),sQuery(id+"F0.wireOp",EDGE,"E6.left"),sQuery(id+"F0.wireOp",EDGE,"E6.right"),sQuery(id+"F0.wireOp",EDGE,"E7.bottom"),sQuery(id+"F0.wireOp",EDGE,"E7.top"),sQuery(id+"F0.wireOp",EDGE,"E7.left"),sQuery(id+"F0.wireOp",EDGE,"E7.right"),sQuery(id+"F0.wireOp",EDGE,"E8.bottom"),sQuery(id+"F0.wireOp",EDGE,"E8.top"),sQuery(id+"F0.wireOp",EDGE,"E8.left"),sQuery(id+"F0.wireOp",EDGE,"E8.right"),sQuery(id+"F0.wireOp",EDGE,"E9.bottom"),sQuery(id+"F0.wireOp",EDGE,"E9.top"),sQuery(id+"F0.wireOp",EDGE,"E9.left"),sQuery(id+"F0.wireOp",EDGE,"E9.right"),subQ1,sQuery(id+"F0.wireOp",EDGE,"E10.top"),subQ0,sQuery(id+"F0.wireOp",EDGE,"E10.right"),sQuery(id+"F0.wireOp",EDGE,"E11.bottom"),sQuery(id+"F0.wireOp",EDGE,"E11.top"),sQuery(id+"F0.wireOp",EDGE,"E11.left"),sQuery(id+"F0.wireOp",EDGE,"E11.right"),sQuery(id+"F0.wireOp",EDGE,"E12.bottom"),sQuery(id+"F0.wireOp",EDGE,"E12.top"),sQuery(id+"F0.wireOp",EDGE,"E12.left"),sQuery(id+"F0.wireOp",EDGE,"E12.right"),sQuery(id+"F0.wireOp",EDGE,"E13.bottom"),sQuery(id+"F0.wireOp",EDGE,"E13.top"),sQuery(id+"F0.wireOp",EDGE,"E13.left"),sQuery(id+"F0.wireOp",EDGE,"E13.right"),sQuery(id+"F0.wireOp",EDGE,"E14.bottom"),sQuery(id+"F0.wireOp",EDGE,"E14.top"),sQuery(id+"F0.wireOp",EDGE,"E14.left"),sQuery(id+"F0.wireOp",EDGE,"E14.right"),sQuery(id+"F0.wireOp",EDGE,"E15.bottom"),sQuery(id+"F0.wireOp",EDGE,"E15.top"),sQuery(id+"F0.wireOp",EDGE,"E15.left"),sQuery(id+"F0.wireOp",EDGE,"E15.right"),sQuery(id+"F0.wireOp",EDGE,"E16"),sQuery(id+"F0.wireOp",EDGE,"E17")])],"isStart":false})]});}
            var Q19;
            Q19=makeQuery(id+"F1.opExtrude","CAP_EDGE",EDGE,{"disambiguationData":[OSD([sQuery(id+"F0.wireOp",EDGE,"E10.top")])],"isStart":false});
            var Q20;
            Q20=makeQuery(id+"F1.opExtrude","CAP_EDGE",EDGE,{"disambiguationData":[OSD([sQuery(id+"F0.wireOp",EDGE,"E12.bottom")])],"isStart":false});
            var Q21;
            {var subQ0=sQuery(id+"F0.wireOp",EDGE,"E12.left");var subQ1=sQuery(id+"F0.wireOp",EDGE,"E12.bottom");Q21=makeQuery(id+"F4.opFillet","BLEND_EDGE",EDGE,{"blendedFrom":[makeQuery(id+"F1.opExtrude","SWEPT_EDGE",EDGE,{"disambiguationData":[OSD([subQ1,subQ0])]}),makeQuery(id+"F1.opExtrude","CAP_FACE",FACE,{"disambiguationData":[OSD([sQuery(id+"F0.wireOp",EDGE,"E0.bottom"),sQuery(id+"F0.wireOp",EDGE,"E5.bottom"),sQuery(id+"F0.wireOp",EDGE,"E5.top"),sQuery(id+"F0.wireOp",EDGE,"E5.left"),sQuery(id+"F0.wireOp",EDGE,"E5.right"),sQuery(id+"F0.wireOp",EDGE,"E6.bottom"),sQuery(id+"F0.wireOp",EDGE,"E6.top"),sQuery(id+"F0.wireOp",EDGE,"E6.left"),sQuery(id+"F0.wireOp",EDGE,"E6.right"),sQuery(id+"F0.wireOp",EDGE,"E7.bottom"),sQuery(id+"F0.wireOp",EDGE,"E7.top"),sQuery(id+"F0.wireOp",EDGE,"E7.left"),sQuery(id+"F0.wireOp",EDGE,"E7.right"),sQuery(id+"F0.wireOp",EDGE,"E8.bottom"),sQuery(id+"F0.wireOp",EDGE,"E8.top"),sQuery(id+"F0.wireOp",EDGE,"E8.left"),sQuery(id+"F0.wireOp",EDGE,"E8.right"),sQuery(id+"F0.wireOp",EDGE,"E9.bottom"),sQuery(id+"F0.wireOp",EDGE,"E9.top"),sQuery(id+"F0.wireOp",EDGE,"E9.left"),sQuery(id+"F0.wireOp",EDGE,"E9.right"),sQuery(id+"F0.wireOp",EDGE,"E10.bottom"),sQuery(id+"F0.wireOp",EDGE,"E10.top"),sQuery(id+"F0.wireOp",EDGE,"E10.left"),sQuery(id+"F0.wireOp",EDGE,"E10.right"),sQuery(id+"F0.wireOp",EDGE,"E11.bottom"),sQuery(id+"F0.wireOp",EDGE,"E11.top"),sQuery(id+"F0.wireOp",EDGE,"E11.left"),sQuery(id+"F0.wireOp",EDGE,"E11.right"),subQ1,sQuery(id+"F0.wireOp",EDGE,"E12.top"),subQ0,sQuery(id+"F0.wireOp",EDGE,"E12.right"),sQuery(id+"F0.wireOp",EDGE,"E13.bottom"),sQuery(id+"F0.wireOp",EDGE,"E13.top"),sQuery(id+"F0.wireOp",EDGE,"E13.left"),sQuery(id+"F0.wireOp",EDGE,"E13.right"),sQuery(id+"F0.wireOp",EDGE,"E14.bottom"),sQuery(id+"F0.wireOp",EDGE,"E14.top"),sQuery(id+"F0.wireOp",EDGE,"E14.left"),sQuery(id+"F0.wireOp",EDGE,"E14.right"),sQuery(id+"F0.wireOp",EDGE,"E15.bottom"),sQuery(id+"F0.wireOp",EDGE,"E15.top"),sQuery(id+"F0.wireOp",EDGE,"E15.left"),sQuery(id+"F0.wireOp",EDGE,"E15.right"),sQuery(id+"F0.wireOp",EDGE,"E16"),sQuery(id+"F0.wireOp",EDGE,"E17")])],"isStart":false})],"blendedInto":[makeQuery(id+"F1.opExtrude","CAP_FACE",FACE,{"disambiguationData":[OSD([sQuery(id+"F0.wireOp",EDGE,"E0.bottom"),sQuery(id+"F0.wireOp",EDGE,"E5.bottom"),sQuery(id+"F0.wireOp",EDGE,"E5.top"),sQuery(id+"F0.wireOp",EDGE,"E5.left"),sQuery(id+"F0.wireOp",EDGE,"E5.right"),sQuery(id+"F0.wireOp",EDGE,"E6.bottom"),sQuery(id+"F0.wireOp",EDGE,"E6.top"),sQuery(id+"F0.wireOp",EDGE,"E6.left"),sQuery(id+"F0.wireOp",EDGE,"E6.right"),sQuery(id+"F0.wireOp",EDGE,"E7.bottom"),sQuery(id+"F0.wireOp",EDGE,"E7.top"),sQuery(id+"F0.wireOp",EDGE,"E7.left"),sQuery(id+"F0.wireOp",EDGE,"E7.right"),sQuery(id+"F0.wireOp",EDGE,"E8.bottom"),sQuery(id+"F0.wireOp",EDGE,"E8.top"),sQuery(id+"F0.wireOp",EDGE,"E8.left"),sQuery(id+"F0.wireOp",EDGE,"E8.right"),sQuery(id+"F0.wireOp",EDGE,"E9.bottom"),sQuery(id+"F0.wireOp",EDGE,"E9.top"),sQuery(id+"F0.wireOp",EDGE,"E9.left"),sQuery(id+"F0.wireOp",EDGE,"E9.right"),sQuery(id+"F0.wireOp",EDGE,"E10.bottom"),sQuery(id+"F0.wireOp",EDGE,"E10.top"),sQuery(id+"F0.wireOp",EDGE,"E10.left"),sQuery(id+"F0.wireOp",EDGE,"E10.right"),sQuery(id+"F0.wireOp",EDGE,"E11.bottom"),sQuery(id+"F0.wireOp",EDGE,"E11.top"),sQuery(id+"F0.wireOp",EDGE,"E11.left"),sQuery(id+"F0.wireOp",EDGE,"E11.right"),subQ1,sQuery(id+"F0.wireOp",EDGE,"E12.top"),subQ0,sQuery(id+"F0.wireOp",EDGE,"E12.right"),sQuery(id+"F0.wireOp",EDGE,"E13.bottom"),sQuery(id+"F0.wireOp",EDGE,"E13.top"),sQuery(id+"F0.wireOp",EDGE,"E13.left"),sQuery(id+"F0.wireOp",EDGE,"E13.right"),sQuery(id+"F0.wireOp",EDGE,"E14.bottom"),sQuery(id+"F0.wireOp",EDGE,"E14.top"),sQuery(id+"F0.wireOp",EDGE,"E14.left"),sQuery(id+"F0.wireOp",EDGE,"E14.right"),sQuery(id+"F0.wireOp",EDGE,"E15.bottom"),sQuery(id+"F0.wireOp",EDGE,"E15.top"),sQuery(id+"F0.wireOp",EDGE,"E15.left"),sQuery(id+"F0.wireOp",EDGE,"E15.right"),sQuery(id+"F0.wireOp",EDGE,"E16"),sQuery(id+"F0.wireOp",EDGE,"E17")])],"isStart":false})]});}
            var Q22;
            Q22=makeQuery(id+"F1.opExtrude","CAP_EDGE",EDGE,{"disambiguationData":[OSD([sQuery(id+"F0.wireOp",EDGE,"E12.top")])],"isStart":false});
            var Q23;
            {var subQ0=sQuery(id+"F0.wireOp",EDGE,"E12.right");var subQ1=sQuery(id+"F0.wireOp",EDGE,"E12.top");Q23=makeQuery(id+"F4.opFillet","BLEND_EDGE",EDGE,{"blendedFrom":[makeQuery(id+"F1.opExtrude","SWEPT_EDGE",EDGE,{"disambiguationData":[OSD([subQ1,subQ0])]}),makeQuery(id+"F1.opExtrude","CAP_FACE",FACE,{"disambiguationData":[OSD([sQuery(id+"F0.wireOp",EDGE,"E0.bottom"),sQuery(id+"F0.wireOp",EDGE,"E5.bottom"),sQuery(id+"F0.wireOp",EDGE,"E5.top"),sQuery(id+"F0.wireOp",EDGE,"E5.left"),sQuery(id+"F0.wireOp",EDGE,"E5.right"),sQuery(id+"F0.wireOp",EDGE,"E6.bottom"),sQuery(id+"F0.wireOp",EDGE,"E6.top"),sQuery(id+"F0.wireOp",EDGE,"E6.left"),sQuery(id+"F0.wireOp",EDGE,"E6.right"),sQuery(id+"F0.wireOp",EDGE,"E7.bottom"),sQuery(id+"F0.wireOp",EDGE,"E7.top"),sQuery(id+"F0.wireOp",EDGE,"E7.left"),sQuery(id+"F0.wireOp",EDGE,"E7.right"),sQuery(id+"F0.wireOp",EDGE,"E8.bottom"),sQuery(id+"F0.wireOp",EDGE,"E8.top"),sQuery(id+"F0.wireOp",EDGE,"E8.left"),sQuery(id+"F0.wireOp",EDGE,"E8.right"),sQuery(id+"F0.wireOp",EDGE,"E9.bottom"),sQuery(id+"F0.wireOp",EDGE,"E9.top"),sQuery(id+"F0.wireOp",EDGE,"E9.left"),sQuery(id+"F0.wireOp",EDGE,"E9.right"),sQuery(id+"F0.wireOp",EDGE,"E10.bottom"),sQuery(id+"F0.wireOp",EDGE,"E10.top"),sQuery(id+"F0.wireOp",EDGE,"E10.left"),sQuery(id+"F0.wireOp",EDGE,"E10.right"),sQuery(id+"F0.wireOp",EDGE,"E11.bottom"),sQuery(id+"F0.wireOp",EDGE,"E11.top"),sQuery(id+"F0.wireOp",EDGE,"E11.left"),sQuery(id+"F0.wireOp",EDGE,"E11.right"),sQuery(id+"F0.wireOp",EDGE,"E12.bottom"),subQ1,sQuery(id+"F0.wireOp",EDGE,"E12.left"),subQ0,sQuery(id+"F0.wireOp",EDGE,"E13.bottom"),sQuery(id+"F0.wireOp",EDGE,"E13.top"),sQuery(id+"F0.wireOp",EDGE,"E13.left"),sQuery(id+"F0.wireOp",EDGE,"E13.right"),sQuery(id+"F0.wireOp",EDGE,"E14.bottom"),sQuery(id+"F0.wireOp",EDGE,"E14.top"),sQuery(id+"F0.wireOp",EDGE,"E14.left"),sQuery(id+"F0.wireOp",EDGE,"E14.right"),sQuery(id+"F0.wireOp",EDGE,"E15.bottom"),sQuery(id+"F0.wireOp",EDGE,"E15.top"),sQuery(id+"F0.wireOp",EDGE,"E15.left"),sQuery(id+"F0.wireOp",EDGE,"E15.right"),sQuery(id+"F0.wireOp",EDGE,"E16"),sQuery(id+"F0.wireOp",EDGE,"E17")])],"isStart":false})],"blendedInto":[makeQuery(id+"F1.opExtrude","CAP_FACE",FACE,{"disambiguationData":[OSD([sQuery(id+"F0.wireOp",EDGE,"E0.bottom"),sQuery(id+"F0.wireOp",EDGE,"E5.bottom"),sQuery(id+"F0.wireOp",EDGE,"E5.top"),sQuery(id+"F0.wireOp",EDGE,"E5.left"),sQuery(id+"F0.wireOp",EDGE,"E5.right"),sQuery(id+"F0.wireOp",EDGE,"E6.bottom"),sQuery(id+"F0.wireOp",EDGE,"E6.top"),sQuery(id+"F0.wireOp",EDGE,"E6.left"),sQuery(id+"F0.wireOp",EDGE,"E6.right"),sQuery(id+"F0.wireOp",EDGE,"E7.bottom"),sQuery(id+"F0.wireOp",EDGE,"E7.top"),sQuery(id+"F0.wireOp",EDGE,"E7.left"),sQuery(id+"F0.wireOp",EDGE,"E7.right"),sQuery(id+"F0.wireOp",EDGE,"E8.bottom"),sQuery(id+"F0.wireOp",EDGE,"E8.top"),sQuery(id+"F0.wireOp",EDGE,"E8.left"),sQuery(id+"F0.wireOp",EDGE,"E8.right"),sQuery(id+"F0.wireOp",EDGE,"E9.bottom"),sQuery(id+"F0.wireOp",EDGE,"E9.top"),sQuery(id+"F0.wireOp",EDGE,"E9.left"),sQuery(id+"F0.wireOp",EDGE,"E9.right"),sQuery(id+"F0.wireOp",EDGE,"E10.bottom"),sQuery(id+"F0.wireOp",EDGE,"E10.top"),sQuery(id+"F0.wireOp",EDGE,"E10.left"),sQuery(id+"F0.wireOp",EDGE,"E10.right"),sQuery(id+"F0.wireOp",EDGE,"E11.bottom"),sQuery(id+"F0.wireOp",EDGE,"E11.top"),sQuery(id+"F0.wireOp",EDGE,"E11.left"),sQuery(id+"F0.wireOp",EDGE,"E11.right"),sQuery(id+"F0.wireOp",EDGE,"E12.bottom"),subQ1,sQuery(id+"F0.wireOp",EDGE,"E12.left"),subQ0,sQuery(id+"F0.wireOp",EDGE,"E13.bottom"),sQuery(id+"F0.wireOp",EDGE,"E13.top"),sQuery(id+"F0.wireOp",EDGE,"E13.left"),sQuery(id+"F0.wireOp",EDGE,"E13.right"),sQuery(id+"F0.wireOp",EDGE,"E14.bottom"),sQuery(id+"F0.wireOp",EDGE,"E14.top"),sQuery(id+"F0.wireOp",EDGE,"E14.left"),sQuery(id+"F0.wireOp",EDGE,"E14.right"),sQuery(id+"F0.wireOp",EDGE,"E15.bottom"),sQuery(id+"F0.wireOp",EDGE,"E15.top"),sQuery(id+"F0.wireOp",EDGE,"E15.left"),sQuery(id+"F0.wireOp",EDGE,"E15.right"),sQuery(id+"F0.wireOp",EDGE,"E16"),sQuery(id+"F0.wireOp",EDGE,"E17")])],"isStart":false})]});}
            var Q24;
            Q24=makeQuery(id+"F1.opExtrude","CAP_EDGE",EDGE,{"disambiguationData":[OSD([sQuery(id+"F0.wireOp",EDGE,"E15.bottom")])],"isStart":true});
            var Q25;
            {var subQ0=sQuery(id+"F0.wireOp",EDGE,"E7.right");var subQ1=sQuery(id+"F0.wireOp",EDGE,"E7.left");var subQ2=sQuery(id+"F0.wireOp",EDGE,"E7.top");var subQ3=sQuery(id+"F0.wireOp",EDGE,"E7.bottom");var subQ4=sQuery(id+"F0.wireOp",EDGE,"E6.right");var subQ5=sQuery(id+"F0.wireOp",EDGE,"E6.left");var subQ6=sQuery(id+"F0.wireOp",EDGE,"E6.top");var subQ7=sQuery(id+"F0.wireOp",EDGE,"E6.bottom");var subQ8=sQuery(id+"F0.wireOp",EDGE,"E9.right");var subQ9=sQuery(id+"F0.wireOp",EDGE,"E9.left");var subQ10=sQuery(id+"F0.wireOp",EDGE,"E9.top");var subQ11=sQuery(id+"F0.wireOp",EDGE,"E9.bottom");var subQ12=sQuery(id+"F0.wireOp",EDGE,"E8.right");var subQ13=sQuery(id+"F0.wireOp",EDGE,"E8.left");var subQ14=sQuery(id+"F0.wireOp",EDGE,"E8.top");var subQ15=sQuery(id+"F0.wireOp",EDGE,"E8.bottom");var subQ16=sQuery(id+"F0.wireOp",EDGE,"E15.left");var subQ17=sQuery(id+"F0.wireOp",EDGE,"E15.bottom");Q25=makeQuery(id+"F4.opFillet","BLEND_EDGE",EDGE,{"blendedFrom":[makeQuery(id+"F1.opExtrude","SWEPT_EDGE",EDGE,{"disambiguationData":[OSD([subQ17,subQ16])]}),makeQuery(id+"F2.boolean.opBoolean","MERGE",FACE,{"derivedFrom":[makeQuery(id+"F1.opExtrude","CAP_FACE",FACE,{"disambiguationData":[OSD([sQuery(id+"F0.wireOp",EDGE,"E0.bottom"),sQuery(id+"F0.wireOp",EDGE,"E5.bottom"),sQuery(id+"F0.wireOp",EDGE,"E5.top"),sQuery(id+"F0.wireOp",EDGE,"E5.left"),sQuery(id+"F0.wireOp",EDGE,"E5.right"),subQ7,subQ6,subQ5,subQ4,subQ3,subQ2,subQ1,subQ0,subQ15,subQ14,subQ13,subQ12,subQ11,subQ10,subQ9,subQ8,sQuery(id+"F0.wireOp",EDGE,"E10.bottom"),sQuery(id+"F0.wireOp",EDGE,"E10.top"),sQuery(id+"F0.wireOp",EDGE,"E10.left"),sQuery(id+"F0.wireOp",EDGE,"E10.right"),sQuery(id+"F0.wireOp",EDGE,"E11.bottom"),sQuery(id+"F0.wireOp",EDGE,"E11.top"),sQuery(id+"F0.wireOp",EDGE,"E11.left"),sQuery(id+"F0.wireOp",EDGE,"E11.right"),sQuery(id+"F0.wireOp",EDGE,"E12.bottom"),sQuery(id+"F0.wireOp",EDGE,"E12.top"),sQuery(id+"F0.wireOp",EDGE,"E12.left"),sQuery(id+"F0.wireOp",EDGE,"E12.right"),sQuery(id+"F0.wireOp",EDGE,"E13.bottom"),sQuery(id+"F0.wireOp",EDGE,"E13.top"),sQuery(id+"F0.wireOp",EDGE,"E13.left"),sQuery(id+"F0.wireOp",EDGE,"E13.right"),sQuery(id+"F0.wireOp",EDGE,"E14.bottom"),sQuery(id+"F0.wireOp",EDGE,"E14.top"),sQuery(id+"F0.wireOp",EDGE,"E14.left"),sQuery(id+"F0.wireOp",EDGE,"E14.right"),subQ17,sQuery(id+"F0.wireOp",EDGE,"E15.top"),subQ16,sQuery(id+"F0.wireOp",EDGE,"E15.right"),sQuery(id+"F0.wireOp",EDGE,"E16"),sQuery(id+"F0.wireOp",EDGE,"E17")])],"isStart":true}),makeQuery(id+"F2.opExtrude","CAP_FACE",FACE,{"disambiguationData":[OSD([sQuery(id+"F0.wireOp",EDGE,"E1"),subQ15,subQ14,subQ13,subQ12])],"isStart":true}),makeQuery(id+"F2.opExtrude","CAP_FACE",FACE,{"disambiguationData":[OSD([sQuery(id+"F0.wireOp",EDGE,"E2"),subQ11,subQ10,subQ9,subQ8])],"isStart":true}),makeQuery(id+"F2.opExtrude","CAP_FACE",FACE,{"disambiguationData":[OSD([sQuery(id+"F0.wireOp",EDGE,"E3"),subQ7,subQ6,subQ5,subQ4])],"isStart":true}),makeQuery(id+"F2.opExtrude","CAP_FACE",FACE,{"disambiguationData":[OSD([sQuery(id+"F0.wireOp",EDGE,"E4"),subQ3,subQ2,subQ1,subQ0])],"isStart":true})]})],"blendedInto":[makeQuery(id+"F2.boolean.opBoolean","MERGE",FACE,{"derivedFrom":[makeQuery(id+"F1.opExtrude","CAP_FACE",FACE,{"disambiguationData":[OSD([sQuery(id+"F0.wireOp",EDGE,"E0.bottom"),sQuery(id+"F0.wireOp",EDGE,"E5.bottom"),sQuery(id+"F0.wireOp",EDGE,"E5.top"),sQuery(id+"F0.wireOp",EDGE,"E5.left"),sQuery(id+"F0.wireOp",EDGE,"E5.right"),subQ7,subQ6,subQ5,subQ4,subQ3,subQ2,subQ1,subQ0,subQ15,subQ14,subQ13,subQ12,subQ11,subQ10,subQ9,subQ8,sQuery(id+"F0.wireOp",EDGE,"E10.bottom"),sQuery(id+"F0.wireOp",EDGE,"E10.top"),sQuery(id+"F0.wireOp",EDGE,"E10.left"),sQuery(id+"F0.wireOp",EDGE,"E10.right"),sQuery(id+"F0.wireOp",EDGE,"E11.bottom"),sQuery(id+"F0.wireOp",EDGE,"E11.top"),sQuery(id+"F0.wireOp",EDGE,"E11.left"),sQuery(id+"F0.wireOp",EDGE,"E11.right"),sQuery(id+"F0.wireOp",EDGE,"E12.bottom"),sQuery(id+"F0.wireOp",EDGE,"E12.top"),sQuery(id+"F0.wireOp",EDGE,"E12.left"),sQuery(id+"F0.wireOp",EDGE,"E12.right"),sQuery(id+"F0.wireOp",EDGE,"E13.bottom"),sQuery(id+"F0.wireOp",EDGE,"E13.top"),sQuery(id+"F0.wireOp",EDGE,"E13.left"),sQuery(id+"F0.wireOp",EDGE,"E13.right"),sQuery(id+"F0.wireOp",EDGE,"E14.bottom"),sQuery(id+"F0.wireOp",EDGE,"E14.top"),sQuery(id+"F0.wireOp",EDGE,"E14.left"),sQuery(id+"F0.wireOp",EDGE,"E14.right"),subQ17,sQuery(id+"F0.wireOp",EDGE,"E15.top"),subQ16,sQuery(id+"F0.wireOp",EDGE,"E15.right"),sQuery(id+"F0.wireOp",EDGE,"E16"),sQuery(id+"F0.wireOp",EDGE,"E17")])],"isStart":true}),makeQuery(id+"F2.opExtrude","CAP_FACE",FACE,{"disambiguationData":[OSD([sQuery(id+"F0.wireOp",EDGE,"E1"),subQ15,subQ14,subQ13,subQ12])],"isStart":true}),makeQuery(id+"F2.opExtrude","CAP_FACE",FACE,{"disambiguationData":[OSD([sQuery(id+"F0.wireOp",EDGE,"E2"),subQ11,subQ10,subQ9,subQ8])],"isStart":true}),makeQuery(id+"F2.opExtrude","CAP_FACE",FACE,{"disambiguationData":[OSD([sQuery(id+"F0.wireOp",EDGE,"E3"),subQ7,subQ6,subQ5,subQ4])],"isStart":true}),makeQuery(id+"F2.opExtrude","CAP_FACE",FACE,{"disambiguationData":[OSD([sQuery(id+"F0.wireOp",EDGE,"E4"),subQ3,subQ2,subQ1,subQ0])],"isStart":true})]})]});}
            var Q26;
            Q26=makeQuery(id+"F1.opExtrude","CAP_EDGE",EDGE,{"disambiguationData":[OSD([sQuery(id+"F0.wireOp",EDGE,"E15.top")])],"isStart":true});
            var Q27;
            {var subQ0=sQuery(id+"F0.wireOp",EDGE,"E7.right");var subQ1=sQuery(id+"F0.wireOp",EDGE,"E7.left");var subQ2=sQuery(id+"F0.wireOp",EDGE,"E7.top");var subQ3=sQuery(id+"F0.wireOp",EDGE,"E7.bottom");var subQ4=sQuery(id+"F0.wireOp",EDGE,"E6.right");var subQ5=sQuery(id+"F0.wireOp",EDGE,"E6.left");var subQ6=sQuery(id+"F0.wireOp",EDGE,"E6.top");var subQ7=sQuery(id+"F0.wireOp",EDGE,"E6.bottom");var subQ8=sQuery(id+"F0.wireOp",EDGE,"E9.right");var subQ9=sQuery(id+"F0.wireOp",EDGE,"E9.left");var subQ10=sQuery(id+"F0.wireOp",EDGE,"E9.top");var subQ11=sQuery(id+"F0.wireOp",EDGE,"E9.bottom");var subQ12=sQuery(id+"F0.wireOp",EDGE,"E8.right");var subQ13=sQuery(id+"F0.wireOp",EDGE,"E8.left");var subQ14=sQuery(id+"F0.wireOp",EDGE,"E8.top");var subQ15=sQuery(id+"F0.wireOp",EDGE,"E8.bottom");var subQ16=sQuery(id+"F0.wireOp",EDGE,"E15.right");var subQ17=sQuery(id+"F0.wireOp",EDGE,"E15.top");Q27=makeQuery(id+"F4.opFillet","BLEND_EDGE",EDGE,{"blendedFrom":[makeQuery(id+"F1.opExtrude","SWEPT_EDGE",EDGE,{"disambiguationData":[OSD([subQ17,subQ16])]}),makeQuery(id+"F2.boolean.opBoolean","MERGE",FACE,{"derivedFrom":[makeQuery(id+"F1.opExtrude","CAP_FACE",FACE,{"disambiguationData":[OSD([sQuery(id+"F0.wireOp",EDGE,"E0.bottom"),sQuery(id+"F0.wireOp",EDGE,"E5.bottom"),sQuery(id+"F0.wireOp",EDGE,"E5.top"),sQuery(id+"F0.wireOp",EDGE,"E5.left"),sQuery(id+"F0.wireOp",EDGE,"E5.right"),subQ7,subQ6,subQ5,subQ4,subQ3,subQ2,subQ1,subQ0,subQ15,subQ14,subQ13,subQ12,subQ11,subQ10,subQ9,subQ8,sQuery(id+"F0.wireOp",EDGE,"E10.bottom"),sQuery(id+"F0.wireOp",EDGE,"E10.top"),sQuery(id+"F0.wireOp",EDGE,"E10.left"),sQuery(id+"F0.wireOp",EDGE,"E10.right"),sQuery(id+"F0.wireOp",EDGE,"E11.bottom"),sQuery(id+"F0.wireOp",EDGE,"E11.top"),sQuery(id+"F0.wireOp",EDGE,"E11.left"),sQuery(id+"F0.wireOp",EDGE,"E11.right"),sQuery(id+"F0.wireOp",EDGE,"E12.bottom"),sQuery(id+"F0.wireOp",EDGE,"E12.top"),sQuery(id+"F0.wireOp",EDGE,"E12.left"),sQuery(id+"F0.wireOp",EDGE,"E12.right"),sQuery(id+"F0.wireOp",EDGE,"E13.bottom"),sQuery(id+"F0.wireOp",EDGE,"E13.top"),sQuery(id+"F0.wireOp",EDGE,"E13.left"),sQuery(id+"F0.wireOp",EDGE,"E13.right"),sQuery(id+"F0.wireOp",EDGE,"E14.bottom"),sQuery(id+"F0.wireOp",EDGE,"E14.top"),sQuery(id+"F0.wireOp",EDGE,"E14.left"),sQuery(id+"F0.wireOp",EDGE,"E14.right"),sQuery(id+"F0.wireOp",EDGE,"E15.bottom"),subQ17,sQuery(id+"F0.wireOp",EDGE,"E15.left"),subQ16,sQuery(id+"F0.wireOp",EDGE,"E16"),sQuery(id+"F0.wireOp",EDGE,"E17")])],"isStart":true}),makeQuery(id+"F2.opExtrude","CAP_FACE",FACE,{"disambiguationData":[OSD([sQuery(id+"F0.wireOp",EDGE,"E1"),subQ15,subQ14,subQ13,subQ12])],"isStart":true}),makeQuery(id+"F2.opExtrude","CAP_FACE",FACE,{"disambiguationData":[OSD([sQuery(id+"F0.wireOp",EDGE,"E2"),subQ11,subQ10,subQ9,subQ8])],"isStart":true}),makeQuery(id+"F2.opExtrude","CAP_FACE",FACE,{"disambiguationData":[OSD([sQuery(id+"F0.wireOp",EDGE,"E3"),subQ7,subQ6,subQ5,subQ4])],"isStart":true}),makeQuery(id+"F2.opExtrude","CAP_FACE",FACE,{"disambiguationData":[OSD([sQuery(id+"F0.wireOp",EDGE,"E4"),subQ3,subQ2,subQ1,subQ0])],"isStart":true})]})],"blendedInto":[makeQuery(id+"F2.boolean.opBoolean","MERGE",FACE,{"derivedFrom":[makeQuery(id+"F1.opExtrude","CAP_FACE",FACE,{"disambiguationData":[OSD([sQuery(id+"F0.wireOp",EDGE,"E0.bottom"),sQuery(id+"F0.wireOp",EDGE,"E5.bottom"),sQuery(id+"F0.wireOp",EDGE,"E5.top"),sQuery(id+"F0.wireOp",EDGE,"E5.left"),sQuery(id+"F0.wireOp",EDGE,"E5.right"),subQ7,subQ6,subQ5,subQ4,subQ3,subQ2,subQ1,subQ0,subQ15,subQ14,subQ13,subQ12,subQ11,subQ10,subQ9,subQ8,sQuery(id+"F0.wireOp",EDGE,"E10.bottom"),sQuery(id+"F0.wireOp",EDGE,"E10.top"),sQuery(id+"F0.wireOp",EDGE,"E10.left"),sQuery(id+"F0.wireOp",EDGE,"E10.right"),sQuery(id+"F0.wireOp",EDGE,"E11.bottom"),sQuery(id+"F0.wireOp",EDGE,"E11.top"),sQuery(id+"F0.wireOp",EDGE,"E11.left"),sQuery(id+"F0.wireOp",EDGE,"E11.right"),sQuery(id+"F0.wireOp",EDGE,"E12.bottom"),sQuery(id+"F0.wireOp",EDGE,"E12.top"),sQuery(id+"F0.wireOp",EDGE,"E12.left"),sQuery(id+"F0.wireOp",EDGE,"E12.right"),sQuery(id+"F0.wireOp",EDGE,"E13.bottom"),sQuery(id+"F0.wireOp",EDGE,"E13.top"),sQuery(id+"F0.wireOp",EDGE,"E13.left"),sQuery(id+"F0.wireOp",EDGE,"E13.right"),sQuery(id+"F0.wireOp",EDGE,"E14.bottom"),sQuery(id+"F0.wireOp",EDGE,"E14.top"),sQuery(id+"F0.wireOp",EDGE,"E14.left"),sQuery(id+"F0.wireOp",EDGE,"E14.right"),sQuery(id+"F0.wireOp",EDGE,"E15.bottom"),subQ17,sQuery(id+"F0.wireOp",EDGE,"E15.left"),subQ16,sQuery(id+"F0.wireOp",EDGE,"E16"),sQuery(id+"F0.wireOp",EDGE,"E17")])],"isStart":true}),makeQuery(id+"F2.opExtrude","CAP_FACE",FACE,{"disambiguationData":[OSD([sQuery(id+"F0.wireOp",EDGE,"E1"),subQ15,subQ14,subQ13,subQ12])],"isStart":true}),makeQuery(id+"F2.opExtrude","CAP_FACE",FACE,{"disambiguationData":[OSD([sQuery(id+"F0.wireOp",EDGE,"E2"),subQ11,subQ10,subQ9,subQ8])],"isStart":true}),makeQuery(id+"F2.opExtrude","CAP_FACE",FACE,{"disambiguationData":[OSD([sQuery(id+"F0.wireOp",EDGE,"E3"),subQ7,subQ6,subQ5,subQ4])],"isStart":true}),makeQuery(id+"F2.opExtrude","CAP_FACE",FACE,{"disambiguationData":[OSD([sQuery(id+"F0.wireOp",EDGE,"E4"),subQ3,subQ2,subQ1,subQ0])],"isStart":true})]})]});}
            var Q28;
            {var subQ0=sQuery(id+"F0.wireOp",EDGE,"E7.right");var subQ1=sQuery(id+"F0.wireOp",EDGE,"E7.left");var subQ2=sQuery(id+"F0.wireOp",EDGE,"E7.top");var subQ3=sQuery(id+"F0.wireOp",EDGE,"E7.bottom");var subQ4=sQuery(id+"F0.wireOp",EDGE,"E6.right");var subQ5=sQuery(id+"F0.wireOp",EDGE,"E6.left");var subQ6=sQuery(id+"F0.wireOp",EDGE,"E6.top");var subQ7=sQuery(id+"F0.wireOp",EDGE,"E6.bottom");var subQ8=sQuery(id+"F0.wireOp",EDGE,"E9.right");var subQ9=sQuery(id+"F0.wireOp",EDGE,"E9.left");var subQ10=sQuery(id+"F0.wireOp",EDGE,"E9.top");var subQ11=sQuery(id+"F0.wireOp",EDGE,"E9.bottom");var subQ12=sQuery(id+"F0.wireOp",EDGE,"E8.right");var subQ13=sQuery(id+"F0.wireOp",EDGE,"E8.left");var subQ14=sQuery(id+"F0.wireOp",EDGE,"E8.top");var subQ15=sQuery(id+"F0.wireOp",EDGE,"E8.bottom");var subQ16=sQuery(id+"F0.wireOp",EDGE,"E14.right");var subQ17=sQuery(id+"F0.wireOp",EDGE,"E14.top");Q28=makeQuery(id+"F4.opFillet","BLEND_EDGE",EDGE,{"blendedFrom":[makeQuery(id+"F1.opExtrude","SWEPT_EDGE",EDGE,{"disambiguationData":[OSD([subQ17,subQ16])]}),makeQuery(id+"F2.boolean.opBoolean","MERGE",FACE,{"derivedFrom":[makeQuery(id+"F1.opExtrude","CAP_FACE",FACE,{"disambiguationData":[OSD([sQuery(id+"F0.wireOp",EDGE,"E0.bottom"),sQuery(id+"F0.wireOp",EDGE,"E5.bottom"),sQuery(id+"F0.wireOp",EDGE,"E5.top"),sQuery(id+"F0.wireOp",EDGE,"E5.left"),sQuery(id+"F0.wireOp",EDGE,"E5.right"),subQ7,subQ6,subQ5,subQ4,subQ3,subQ2,subQ1,subQ0,subQ15,subQ14,subQ13,subQ12,subQ11,subQ10,subQ9,subQ8,sQuery(id+"F0.wireOp",EDGE,"E10.bottom"),sQuery(id+"F0.wireOp",EDGE,"E10.top"),sQuery(id+"F0.wireOp",EDGE,"E10.left"),sQuery(id+"F0.wireOp",EDGE,"E10.right"),sQuery(id+"F0.wireOp",EDGE,"E11.bottom"),sQuery(id+"F0.wireOp",EDGE,"E11.top"),sQuery(id+"F0.wireOp",EDGE,"E11.left"),sQuery(id+"F0.wireOp",EDGE,"E11.right"),sQuery(id+"F0.wireOp",EDGE,"E12.bottom"),sQuery(id+"F0.wireOp",EDGE,"E12.top"),sQuery(id+"F0.wireOp",EDGE,"E12.left"),sQuery(id+"F0.wireOp",EDGE,"E12.right"),sQuery(id+"F0.wireOp",EDGE,"E13.bottom"),sQuery(id+"F0.wireOp",EDGE,"E13.top"),sQuery(id+"F0.wireOp",EDGE,"E13.left"),sQuery(id+"F0.wireOp",EDGE,"E13.right"),sQuery(id+"F0.wireOp",EDGE,"E14.bottom"),subQ17,sQuery(id+"F0.wireOp",EDGE,"E14.left"),subQ16,sQuery(id+"F0.wireOp",EDGE,"E15.bottom"),sQuery(id+"F0.wireOp",EDGE,"E15.top"),sQuery(id+"F0.wireOp",EDGE,"E15.left"),sQuery(id+"F0.wireOp",EDGE,"E15.right"),sQuery(id+"F0.wireOp",EDGE,"E16"),sQuery(id+"F0.wireOp",EDGE,"E17")])],"isStart":true}),makeQuery(id+"F2.opExtrude","CAP_FACE",FACE,{"disambiguationData":[OSD([sQuery(id+"F0.wireOp",EDGE,"E1"),subQ15,subQ14,subQ13,subQ12])],"isStart":true}),makeQuery(id+"F2.opExtrude","CAP_FACE",FACE,{"disambiguationData":[OSD([sQuery(id+"F0.wireOp",EDGE,"E2"),subQ11,subQ10,subQ9,subQ8])],"isStart":true}),makeQuery(id+"F2.opExtrude","CAP_FACE",FACE,{"disambiguationData":[OSD([sQuery(id+"F0.wireOp",EDGE,"E3"),subQ7,subQ6,subQ5,subQ4])],"isStart":true}),makeQuery(id+"F2.opExtrude","CAP_FACE",FACE,{"disambiguationData":[OSD([sQuery(id+"F0.wireOp",EDGE,"E4"),subQ3,subQ2,subQ1,subQ0])],"isStart":true})]})],"blendedInto":[makeQuery(id+"F2.boolean.opBoolean","MERGE",FACE,{"derivedFrom":[makeQuery(id+"F1.opExtrude","CAP_FACE",FACE,{"disambiguationData":[OSD([sQuery(id+"F0.wireOp",EDGE,"E0.bottom"),sQuery(id+"F0.wireOp",EDGE,"E5.bottom"),sQuery(id+"F0.wireOp",EDGE,"E5.top"),sQuery(id+"F0.wireOp",EDGE,"E5.left"),sQuery(id+"F0.wireOp",EDGE,"E5.right"),subQ7,subQ6,subQ5,subQ4,subQ3,subQ2,subQ1,subQ0,subQ15,subQ14,subQ13,subQ12,subQ11,subQ10,subQ9,subQ8,sQuery(id+"F0.wireOp",EDGE,"E10.bottom"),sQuery(id+"F0.wireOp",EDGE,"E10.top"),sQuery(id+"F0.wireOp",EDGE,"E10.left"),sQuery(id+"F0.wireOp",EDGE,"E10.right"),sQuery(id+"F0.wireOp",EDGE,"E11.bottom"),sQuery(id+"F0.wireOp",EDGE,"E11.top"),sQuery(id+"F0.wireOp",EDGE,"E11.left"),sQuery(id+"F0.wireOp",EDGE,"E11.right"),sQuery(id+"F0.wireOp",EDGE,"E12.bottom"),sQuery(id+"F0.wireOp",EDGE,"E12.top"),sQuery(id+"F0.wireOp",EDGE,"E12.left"),sQuery(id+"F0.wireOp",EDGE,"E12.right"),sQuery(id+"F0.wireOp",EDGE,"E13.bottom"),sQuery(id+"F0.wireOp",EDGE,"E13.top"),sQuery(id+"F0.wireOp",EDGE,"E13.left"),sQuery(id+"F0.wireOp",EDGE,"E13.right"),sQuery(id+"F0.wireOp",EDGE,"E14.bottom"),subQ17,sQuery(id+"F0.wireOp",EDGE,"E14.left"),subQ16,sQuery(id+"F0.wireOp",EDGE,"E15.bottom"),sQuery(id+"F0.wireOp",EDGE,"E15.top"),sQuery(id+"F0.wireOp",EDGE,"E15.left"),sQuery(id+"F0.wireOp",EDGE,"E15.right"),sQuery(id+"F0.wireOp",EDGE,"E16"),sQuery(id+"F0.wireOp",EDGE,"E17")])],"isStart":true}),makeQuery(id+"F2.opExtrude","CAP_FACE",FACE,{"disambiguationData":[OSD([sQuery(id+"F0.wireOp",EDGE,"E1"),subQ15,subQ14,subQ13,subQ12])],"isStart":true}),makeQuery(id+"F2.opExtrude","CAP_FACE",FACE,{"disambiguationData":[OSD([sQuery(id+"F0.wireOp",EDGE,"E2"),subQ11,subQ10,subQ9,subQ8])],"isStart":true}),makeQuery(id+"F2.opExtrude","CAP_FACE",FACE,{"disambiguationData":[OSD([sQuery(id+"F0.wireOp",EDGE,"E3"),subQ7,subQ6,subQ5,subQ4])],"isStart":true}),makeQuery(id+"F2.opExtrude","CAP_FACE",FACE,{"disambiguationData":[OSD([sQuery(id+"F0.wireOp",EDGE,"E4"),subQ3,subQ2,subQ1,subQ0])],"isStart":true})]})]});}
            var Q29;
            Q29=makeQuery(id+"F1.opExtrude","CAP_EDGE",EDGE,{"disambiguationData":[OSD([sQuery(id+"F0.wireOp",EDGE,"E14.bottom")])],"isStart":true});
            var Q30;
            {var subQ0=sQuery(id+"F0.wireOp",EDGE,"E7.right");var subQ1=sQuery(id+"F0.wireOp",EDGE,"E7.left");var subQ2=sQuery(id+"F0.wireOp",EDGE,"E7.top");var subQ3=sQuery(id+"F0.wireOp",EDGE,"E7.bottom");var subQ4=sQuery(id+"F0.wireOp",EDGE,"E6.right");var subQ5=sQuery(id+"F0.wireOp",EDGE,"E6.left");var subQ6=sQuery(id+"F0.wireOp",EDGE,"E6.top");var subQ7=sQuery(id+"F0.wireOp",EDGE,"E6.bottom");var subQ8=sQuery(id+"F0.wireOp",EDGE,"E9.right");var subQ9=sQuery(id+"F0.wireOp",EDGE,"E9.left");var subQ10=sQuery(id+"F0.wireOp",EDGE,"E9.top");var subQ11=sQuery(id+"F0.wireOp",EDGE,"E9.bottom");var subQ12=sQuery(id+"F0.wireOp",EDGE,"E8.right");var subQ13=sQuery(id+"F0.wireOp",EDGE,"E8.left");var subQ14=sQuery(id+"F0.wireOp",EDGE,"E8.top");var subQ15=sQuery(id+"F0.wireOp",EDGE,"E8.bottom");var subQ16=sQuery(id+"F0.wireOp",EDGE,"E14.left");var subQ17=sQuery(id+"F0.wireOp",EDGE,"E14.bottom");Q30=makeQuery(id+"F4.opFillet","BLEND_EDGE",EDGE,{"blendedFrom":[makeQuery(id+"F1.opExtrude","SWEPT_EDGE",EDGE,{"disambiguationData":[OSD([subQ17,subQ16])]}),makeQuery(id+"F2.boolean.opBoolean","MERGE",FACE,{"derivedFrom":[makeQuery(id+"F1.opExtrude","CAP_FACE",FACE,{"disambiguationData":[OSD([sQuery(id+"F0.wireOp",EDGE,"E0.bottom"),sQuery(id+"F0.wireOp",EDGE,"E5.bottom"),sQuery(id+"F0.wireOp",EDGE,"E5.top"),sQuery(id+"F0.wireOp",EDGE,"E5.left"),sQuery(id+"F0.wireOp",EDGE,"E5.right"),subQ7,subQ6,subQ5,subQ4,subQ3,subQ2,subQ1,subQ0,subQ15,subQ14,subQ13,subQ12,subQ11,subQ10,subQ9,subQ8,sQuery(id+"F0.wireOp",EDGE,"E10.bottom"),sQuery(id+"F0.wireOp",EDGE,"E10.top"),sQuery(id+"F0.wireOp",EDGE,"E10.left"),sQuery(id+"F0.wireOp",EDGE,"E10.right"),sQuery(id+"F0.wireOp",EDGE,"E11.bottom"),sQuery(id+"F0.wireOp",EDGE,"E11.top"),sQuery(id+"F0.wireOp",EDGE,"E11.left"),sQuery(id+"F0.wireOp",EDGE,"E11.right"),sQuery(id+"F0.wireOp",EDGE,"E12.bottom"),sQuery(id+"F0.wireOp",EDGE,"E12.top"),sQuery(id+"F0.wireOp",EDGE,"E12.left"),sQuery(id+"F0.wireOp",EDGE,"E12.right"),sQuery(id+"F0.wireOp",EDGE,"E13.bottom"),sQuery(id+"F0.wireOp",EDGE,"E13.top"),sQuery(id+"F0.wireOp",EDGE,"E13.left"),sQuery(id+"F0.wireOp",EDGE,"E13.right"),subQ17,sQuery(id+"F0.wireOp",EDGE,"E14.top"),subQ16,sQuery(id+"F0.wireOp",EDGE,"E14.right"),sQuery(id+"F0.wireOp",EDGE,"E15.bottom"),sQuery(id+"F0.wireOp",EDGE,"E15.top"),sQuery(id+"F0.wireOp",EDGE,"E15.left"),sQuery(id+"F0.wireOp",EDGE,"E15.right"),sQuery(id+"F0.wireOp",EDGE,"E16"),sQuery(id+"F0.wireOp",EDGE,"E17")])],"isStart":true}),makeQuery(id+"F2.opExtrude","CAP_FACE",FACE,{"disambiguationData":[OSD([sQuery(id+"F0.wireOp",EDGE,"E1"),subQ15,subQ14,subQ13,subQ12])],"isStart":true}),makeQuery(id+"F2.opExtrude","CAP_FACE",FACE,{"disambiguationData":[OSD([sQuery(id+"F0.wireOp",EDGE,"E2"),subQ11,subQ10,subQ9,subQ8])],"isStart":true}),makeQuery(id+"F2.opExtrude","CAP_FACE",FACE,{"disambiguationData":[OSD([sQuery(id+"F0.wireOp",EDGE,"E3"),subQ7,subQ6,subQ5,subQ4])],"isStart":true}),makeQuery(id+"F2.opExtrude","CAP_FACE",FACE,{"disambiguationData":[OSD([sQuery(id+"F0.wireOp",EDGE,"E4"),subQ3,subQ2,subQ1,subQ0])],"isStart":true})]})],"blendedInto":[makeQuery(id+"F2.boolean.opBoolean","MERGE",FACE,{"derivedFrom":[makeQuery(id+"F1.opExtrude","CAP_FACE",FACE,{"disambiguationData":[OSD([sQuery(id+"F0.wireOp",EDGE,"E0.bottom"),sQuery(id+"F0.wireOp",EDGE,"E5.bottom"),sQuery(id+"F0.wireOp",EDGE,"E5.top"),sQuery(id+"F0.wireOp",EDGE,"E5.left"),sQuery(id+"F0.wireOp",EDGE,"E5.right"),subQ7,subQ6,subQ5,subQ4,subQ3,subQ2,subQ1,subQ0,subQ15,subQ14,subQ13,subQ12,subQ11,subQ10,subQ9,subQ8,sQuery(id+"F0.wireOp",EDGE,"E10.bottom"),sQuery(id+"F0.wireOp",EDGE,"E10.top"),sQuery(id+"F0.wireOp",EDGE,"E10.left"),sQuery(id+"F0.wireOp",EDGE,"E10.right"),sQuery(id+"F0.wireOp",EDGE,"E11.bottom"),sQuery(id+"F0.wireOp",EDGE,"E11.top"),sQuery(id+"F0.wireOp",EDGE,"E11.left"),sQuery(id+"F0.wireOp",EDGE,"E11.right"),sQuery(id+"F0.wireOp",EDGE,"E12.bottom"),sQuery(id+"F0.wireOp",EDGE,"E12.top"),sQuery(id+"F0.wireOp",EDGE,"E12.left"),sQuery(id+"F0.wireOp",EDGE,"E12.right"),sQuery(id+"F0.wireOp",EDGE,"E13.bottom"),sQuery(id+"F0.wireOp",EDGE,"E13.top"),sQuery(id+"F0.wireOp",EDGE,"E13.left"),sQuery(id+"F0.wireOp",EDGE,"E13.right"),subQ17,sQuery(id+"F0.wireOp",EDGE,"E14.top"),subQ16,sQuery(id+"F0.wireOp",EDGE,"E14.right"),sQuery(id+"F0.wireOp",EDGE,"E15.bottom"),sQuery(id+"F0.wireOp",EDGE,"E15.top"),sQuery(id+"F0.wireOp",EDGE,"E15.left"),sQuery(id+"F0.wireOp",EDGE,"E15.right"),sQuery(id+"F0.wireOp",EDGE,"E16"),sQuery(id+"F0.wireOp",EDGE,"E17")])],"isStart":true}),makeQuery(id+"F2.opExtrude","CAP_FACE",FACE,{"disambiguationData":[OSD([sQuery(id+"F0.wireOp",EDGE,"E1"),subQ15,subQ14,subQ13,subQ12])],"isStart":true}),makeQuery(id+"F2.opExtrude","CAP_FACE",FACE,{"disambiguationData":[OSD([sQuery(id+"F0.wireOp",EDGE,"E2"),subQ11,subQ10,subQ9,subQ8])],"isStart":true}),makeQuery(id+"F2.opExtrude","CAP_FACE",FACE,{"disambiguationData":[OSD([sQuery(id+"F0.wireOp",EDGE,"E3"),subQ7,subQ6,subQ5,subQ4])],"isStart":true}),makeQuery(id+"F2.opExtrude","CAP_FACE",FACE,{"disambiguationData":[OSD([sQuery(id+"F0.wireOp",EDGE,"E4"),subQ3,subQ2,subQ1,subQ0])],"isStart":true})]})]});}
            var Q31;
            Q31=makeQuery(id+"F1.opExtrude","CAP_EDGE",EDGE,{"disambiguationData":[OSD([sQuery(id+"F0.wireOp",EDGE,"E14.top")])],"isStart":true});
            var Q32;
            Q32=makeQuery(id+"F1.opExtrude","CAP_EDGE",EDGE,{"disambiguationData":[OSD([sQuery(id+"F0.wireOp",EDGE,"E13.bottom")])],"isStart":true});
            var Q33;
            {var subQ0=sQuery(id+"F0.wireOp",EDGE,"E7.right");var subQ1=sQuery(id+"F0.wireOp",EDGE,"E7.left");var subQ2=sQuery(id+"F0.wireOp",EDGE,"E7.top");var subQ3=sQuery(id+"F0.wireOp",EDGE,"E7.bottom");var subQ4=sQuery(id+"F0.wireOp",EDGE,"E6.right");var subQ5=sQuery(id+"F0.wireOp",EDGE,"E6.left");var subQ6=sQuery(id+"F0.wireOp",EDGE,"E6.top");var subQ7=sQuery(id+"F0.wireOp",EDGE,"E6.bottom");var subQ8=sQuery(id+"F0.wireOp",EDGE,"E9.right");var subQ9=sQuery(id+"F0.wireOp",EDGE,"E9.left");var subQ10=sQuery(id+"F0.wireOp",EDGE,"E9.top");var subQ11=sQuery(id+"F0.wireOp",EDGE,"E9.bottom");var subQ12=sQuery(id+"F0.wireOp",EDGE,"E8.right");var subQ13=sQuery(id+"F0.wireOp",EDGE,"E8.left");var subQ14=sQuery(id+"F0.wireOp",EDGE,"E8.top");var subQ15=sQuery(id+"F0.wireOp",EDGE,"E8.bottom");var subQ16=sQuery(id+"F0.wireOp",EDGE,"E13.left");var subQ17=sQuery(id+"F0.wireOp",EDGE,"E13.bottom");Q33=makeQuery(id+"F4.opFillet","BLEND_EDGE",EDGE,{"blendedFrom":[makeQuery(id+"F1.opExtrude","SWEPT_EDGE",EDGE,{"disambiguationData":[OSD([subQ17,subQ16])]}),makeQuery(id+"F2.boolean.opBoolean","MERGE",FACE,{"derivedFrom":[makeQuery(id+"F1.opExtrude","CAP_FACE",FACE,{"disambiguationData":[OSD([sQuery(id+"F0.wireOp",EDGE,"E0.bottom"),sQuery(id+"F0.wireOp",EDGE,"E5.bottom"),sQuery(id+"F0.wireOp",EDGE,"E5.top"),sQuery(id+"F0.wireOp",EDGE,"E5.left"),sQuery(id+"F0.wireOp",EDGE,"E5.right"),subQ7,subQ6,subQ5,subQ4,subQ3,subQ2,subQ1,subQ0,subQ15,subQ14,subQ13,subQ12,subQ11,subQ10,subQ9,subQ8,sQuery(id+"F0.wireOp",EDGE,"E10.bottom"),sQuery(id+"F0.wireOp",EDGE,"E10.top"),sQuery(id+"F0.wireOp",EDGE,"E10.left"),sQuery(id+"F0.wireOp",EDGE,"E10.right"),sQuery(id+"F0.wireOp",EDGE,"E11.bottom"),sQuery(id+"F0.wireOp",EDGE,"E11.top"),sQuery(id+"F0.wireOp",EDGE,"E11.left"),sQuery(id+"F0.wireOp",EDGE,"E11.right"),sQuery(id+"F0.wireOp",EDGE,"E12.bottom"),sQuery(id+"F0.wireOp",EDGE,"E12.top"),sQuery(id+"F0.wireOp",EDGE,"E12.left"),sQuery(id+"F0.wireOp",EDGE,"E12.right"),subQ17,sQuery(id+"F0.wireOp",EDGE,"E13.top"),subQ16,sQuery(id+"F0.wireOp",EDGE,"E13.right"),sQuery(id+"F0.wireOp",EDGE,"E14.bottom"),sQuery(id+"F0.wireOp",EDGE,"E14.top"),sQuery(id+"F0.wireOp",EDGE,"E14.left"),sQuery(id+"F0.wireOp",EDGE,"E14.right"),sQuery(id+"F0.wireOp",EDGE,"E15.bottom"),sQuery(id+"F0.wireOp",EDGE,"E15.top"),sQuery(id+"F0.wireOp",EDGE,"E15.left"),sQuery(id+"F0.wireOp",EDGE,"E15.right"),sQuery(id+"F0.wireOp",EDGE,"E16"),sQuery(id+"F0.wireOp",EDGE,"E17")])],"isStart":true}),makeQuery(id+"F2.opExtrude","CAP_FACE",FACE,{"disambiguationData":[OSD([sQuery(id+"F0.wireOp",EDGE,"E1"),subQ15,subQ14,subQ13,subQ12])],"isStart":true}),makeQuery(id+"F2.opExtrude","CAP_FACE",FACE,{"disambiguationData":[OSD([sQuery(id+"F0.wireOp",EDGE,"E2"),subQ11,subQ10,subQ9,subQ8])],"isStart":true}),makeQuery(id+"F2.opExtrude","CAP_FACE",FACE,{"disambiguationData":[OSD([sQuery(id+"F0.wireOp",EDGE,"E3"),subQ7,subQ6,subQ5,subQ4])],"isStart":true}),makeQuery(id+"F2.opExtrude","CAP_FACE",FACE,{"disambiguationData":[OSD([sQuery(id+"F0.wireOp",EDGE,"E4"),subQ3,subQ2,subQ1,subQ0])],"isStart":true})]})],"blendedInto":[makeQuery(id+"F2.boolean.opBoolean","MERGE",FACE,{"derivedFrom":[makeQuery(id+"F1.opExtrude","CAP_FACE",FACE,{"disambiguationData":[OSD([sQuery(id+"F0.wireOp",EDGE,"E0.bottom"),sQuery(id+"F0.wireOp",EDGE,"E5.bottom"),sQuery(id+"F0.wireOp",EDGE,"E5.top"),sQuery(id+"F0.wireOp",EDGE,"E5.left"),sQuery(id+"F0.wireOp",EDGE,"E5.right"),subQ7,subQ6,subQ5,subQ4,subQ3,subQ2,subQ1,subQ0,subQ15,subQ14,subQ13,subQ12,subQ11,subQ10,subQ9,subQ8,sQuery(id+"F0.wireOp",EDGE,"E10.bottom"),sQuery(id+"F0.wireOp",EDGE,"E10.top"),sQuery(id+"F0.wireOp",EDGE,"E10.left"),sQuery(id+"F0.wireOp",EDGE,"E10.right"),sQuery(id+"F0.wireOp",EDGE,"E11.bottom"),sQuery(id+"F0.wireOp",EDGE,"E11.top"),sQuery(id+"F0.wireOp",EDGE,"E11.left"),sQuery(id+"F0.wireOp",EDGE,"E11.right"),sQuery(id+"F0.wireOp",EDGE,"E12.bottom"),sQuery(id+"F0.wireOp",EDGE,"E12.top"),sQuery(id+"F0.wireOp",EDGE,"E12.left"),sQuery(id+"F0.wireOp",EDGE,"E12.right"),subQ17,sQuery(id+"F0.wireOp",EDGE,"E13.top"),subQ16,sQuery(id+"F0.wireOp",EDGE,"E13.right"),sQuery(id+"F0.wireOp",EDGE,"E14.bottom"),sQuery(id+"F0.wireOp",EDGE,"E14.top"),sQuery(id+"F0.wireOp",EDGE,"E14.left"),sQuery(id+"F0.wireOp",EDGE,"E14.right"),sQuery(id+"F0.wireOp",EDGE,"E15.bottom"),sQuery(id+"F0.wireOp",EDGE,"E15.top"),sQuery(id+"F0.wireOp",EDGE,"E15.left"),sQuery(id+"F0.wireOp",EDGE,"E15.right"),sQuery(id+"F0.wireOp",EDGE,"E16"),sQuery(id+"F0.wireOp",EDGE,"E17")])],"isStart":true}),makeQuery(id+"F2.opExtrude","CAP_FACE",FACE,{"disambiguationData":[OSD([sQuery(id+"F0.wireOp",EDGE,"E1"),subQ15,subQ14,subQ13,subQ12])],"isStart":true}),makeQuery(id+"F2.opExtrude","CAP_FACE",FACE,{"disambiguationData":[OSD([sQuery(id+"F0.wireOp",EDGE,"E2"),subQ11,subQ10,subQ9,subQ8])],"isStart":true}),makeQuery(id+"F2.opExtrude","CAP_FACE",FACE,{"disambiguationData":[OSD([sQuery(id+"F0.wireOp",EDGE,"E3"),subQ7,subQ6,subQ5,subQ4])],"isStart":true}),makeQuery(id+"F2.opExtrude","CAP_FACE",FACE,{"disambiguationData":[OSD([sQuery(id+"F0.wireOp",EDGE,"E4"),subQ3,subQ2,subQ1,subQ0])],"isStart":true})]})]});}
            var Q34;
            Q34=makeQuery(id+"F1.opExtrude","CAP_EDGE",EDGE,{"disambiguationData":[OSD([sQuery(id+"F0.wireOp",EDGE,"E13.top")])],"isStart":true});
            var Q35;
            {var subQ0=sQuery(id+"F0.wireOp",EDGE,"E7.right");var subQ1=sQuery(id+"F0.wireOp",EDGE,"E7.left");var subQ2=sQuery(id+"F0.wireOp",EDGE,"E7.top");var subQ3=sQuery(id+"F0.wireOp",EDGE,"E7.bottom");var subQ4=sQuery(id+"F0.wireOp",EDGE,"E6.right");var subQ5=sQuery(id+"F0.wireOp",EDGE,"E6.left");var subQ6=sQuery(id+"F0.wireOp",EDGE,"E6.top");var subQ7=sQuery(id+"F0.wireOp",EDGE,"E6.bottom");var subQ8=sQuery(id+"F0.wireOp",EDGE,"E9.right");var subQ9=sQuery(id+"F0.wireOp",EDGE,"E9.left");var subQ10=sQuery(id+"F0.wireOp",EDGE,"E9.top");var subQ11=sQuery(id+"F0.wireOp",EDGE,"E9.bottom");var subQ12=sQuery(id+"F0.wireOp",EDGE,"E8.right");var subQ13=sQuery(id+"F0.wireOp",EDGE,"E8.left");var subQ14=sQuery(id+"F0.wireOp",EDGE,"E8.top");var subQ15=sQuery(id+"F0.wireOp",EDGE,"E8.bottom");var subQ16=sQuery(id+"F0.wireOp",EDGE,"E13.right");var subQ17=sQuery(id+"F0.wireOp",EDGE,"E13.top");Q35=makeQuery(id+"F4.opFillet","BLEND_EDGE",EDGE,{"blendedFrom":[makeQuery(id+"F1.opExtrude","SWEPT_EDGE",EDGE,{"disambiguationData":[OSD([subQ17,subQ16])]}),makeQuery(id+"F2.boolean.opBoolean","MERGE",FACE,{"derivedFrom":[makeQuery(id+"F1.opExtrude","CAP_FACE",FACE,{"disambiguationData":[OSD([sQuery(id+"F0.wireOp",EDGE,"E0.bottom"),sQuery(id+"F0.wireOp",EDGE,"E5.bottom"),sQuery(id+"F0.wireOp",EDGE,"E5.top"),sQuery(id+"F0.wireOp",EDGE,"E5.left"),sQuery(id+"F0.wireOp",EDGE,"E5.right"),subQ7,subQ6,subQ5,subQ4,subQ3,subQ2,subQ1,subQ0,subQ15,subQ14,subQ13,subQ12,subQ11,subQ10,subQ9,subQ8,sQuery(id+"F0.wireOp",EDGE,"E10.bottom"),sQuery(id+"F0.wireOp",EDGE,"E10.top"),sQuery(id+"F0.wireOp",EDGE,"E10.left"),sQuery(id+"F0.wireOp",EDGE,"E10.right"),sQuery(id+"F0.wireOp",EDGE,"E11.bottom"),sQuery(id+"F0.wireOp",EDGE,"E11.top"),sQuery(id+"F0.wireOp",EDGE,"E11.left"),sQuery(id+"F0.wireOp",EDGE,"E11.right"),sQuery(id+"F0.wireOp",EDGE,"E12.bottom"),sQuery(id+"F0.wireOp",EDGE,"E12.top"),sQuery(id+"F0.wireOp",EDGE,"E12.left"),sQuery(id+"F0.wireOp",EDGE,"E12.right"),sQuery(id+"F0.wireOp",EDGE,"E13.bottom"),subQ17,sQuery(id+"F0.wireOp",EDGE,"E13.left"),subQ16,sQuery(id+"F0.wireOp",EDGE,"E14.bottom"),sQuery(id+"F0.wireOp",EDGE,"E14.top"),sQuery(id+"F0.wireOp",EDGE,"E14.left"),sQuery(id+"F0.wireOp",EDGE,"E14.right"),sQuery(id+"F0.wireOp",EDGE,"E15.bottom"),sQuery(id+"F0.wireOp",EDGE,"E15.top"),sQuery(id+"F0.wireOp",EDGE,"E15.left"),sQuery(id+"F0.wireOp",EDGE,"E15.right"),sQuery(id+"F0.wireOp",EDGE,"E16"),sQuery(id+"F0.wireOp",EDGE,"E17")])],"isStart":true}),makeQuery(id+"F2.opExtrude","CAP_FACE",FACE,{"disambiguationData":[OSD([sQuery(id+"F0.wireOp",EDGE,"E1"),subQ15,subQ14,subQ13,subQ12])],"isStart":true}),makeQuery(id+"F2.opExtrude","CAP_FACE",FACE,{"disambiguationData":[OSD([sQuery(id+"F0.wireOp",EDGE,"E2"),subQ11,subQ10,subQ9,subQ8])],"isStart":true}),makeQuery(id+"F2.opExtrude","CAP_FACE",FACE,{"disambiguationData":[OSD([sQuery(id+"F0.wireOp",EDGE,"E3"),subQ7,subQ6,subQ5,subQ4])],"isStart":true}),makeQuery(id+"F2.opExtrude","CAP_FACE",FACE,{"disambiguationData":[OSD([sQuery(id+"F0.wireOp",EDGE,"E4"),subQ3,subQ2,subQ1,subQ0])],"isStart":true})]})],"blendedInto":[makeQuery(id+"F2.boolean.opBoolean","MERGE",FACE,{"derivedFrom":[makeQuery(id+"F1.opExtrude","CAP_FACE",FACE,{"disambiguationData":[OSD([sQuery(id+"F0.wireOp",EDGE,"E0.bottom"),sQuery(id+"F0.wireOp",EDGE,"E5.bottom"),sQuery(id+"F0.wireOp",EDGE,"E5.top"),sQuery(id+"F0.wireOp",EDGE,"E5.left"),sQuery(id+"F0.wireOp",EDGE,"E5.right"),subQ7,subQ6,subQ5,subQ4,subQ3,subQ2,subQ1,subQ0,subQ15,subQ14,subQ13,subQ12,subQ11,subQ10,subQ9,subQ8,sQuery(id+"F0.wireOp",EDGE,"E10.bottom"),sQuery(id+"F0.wireOp",EDGE,"E10.top"),sQuery(id+"F0.wireOp",EDGE,"E10.left"),sQuery(id+"F0.wireOp",EDGE,"E10.right"),sQuery(id+"F0.wireOp",EDGE,"E11.bottom"),sQuery(id+"F0.wireOp",EDGE,"E11.top"),sQuery(id+"F0.wireOp",EDGE,"E11.left"),sQuery(id+"F0.wireOp",EDGE,"E11.right"),sQuery(id+"F0.wireOp",EDGE,"E12.bottom"),sQuery(id+"F0.wireOp",EDGE,"E12.top"),sQuery(id+"F0.wireOp",EDGE,"E12.left"),sQuery(id+"F0.wireOp",EDGE,"E12.right"),sQuery(id+"F0.wireOp",EDGE,"E13.bottom"),subQ17,sQuery(id+"F0.wireOp",EDGE,"E13.left"),subQ16,sQuery(id+"F0.wireOp",EDGE,"E14.bottom"),sQuery(id+"F0.wireOp",EDGE,"E14.top"),sQuery(id+"F0.wireOp",EDGE,"E14.left"),sQuery(id+"F0.wireOp",EDGE,"E14.right"),sQuery(id+"F0.wireOp",EDGE,"E15.bottom"),sQuery(id+"F0.wireOp",EDGE,"E15.top"),sQuery(id+"F0.wireOp",EDGE,"E15.left"),sQuery(id+"F0.wireOp",EDGE,"E15.right"),sQuery(id+"F0.wireOp",EDGE,"E16"),sQuery(id+"F0.wireOp",EDGE,"E17")])],"isStart":true}),makeQuery(id+"F2.opExtrude","CAP_FACE",FACE,{"disambiguationData":[OSD([sQuery(id+"F0.wireOp",EDGE,"E1"),subQ15,subQ14,subQ13,subQ12])],"isStart":true}),makeQuery(id+"F2.opExtrude","CAP_FACE",FACE,{"disambiguationData":[OSD([sQuery(id+"F0.wireOp",EDGE,"E2"),subQ11,subQ10,subQ9,subQ8])],"isStart":true}),makeQuery(id+"F2.opExtrude","CAP_FACE",FACE,{"disambiguationData":[OSD([sQuery(id+"F0.wireOp",EDGE,"E3"),subQ7,subQ6,subQ5,subQ4])],"isStart":true}),makeQuery(id+"F2.opExtrude","CAP_FACE",FACE,{"disambiguationData":[OSD([sQuery(id+"F0.wireOp",EDGE,"E4"),subQ3,subQ2,subQ1,subQ0])],"isStart":true})]})]});}
            var Q36;
            {var subQ0=sQuery(id+"F0.wireOp",EDGE,"E7.right");var subQ1=sQuery(id+"F0.wireOp",EDGE,"E7.left");var subQ2=sQuery(id+"F0.wireOp",EDGE,"E7.top");var subQ3=sQuery(id+"F0.wireOp",EDGE,"E7.bottom");var subQ4=sQuery(id+"F0.wireOp",EDGE,"E6.right");var subQ5=sQuery(id+"F0.wireOp",EDGE,"E6.left");var subQ6=sQuery(id+"F0.wireOp",EDGE,"E6.top");var subQ7=sQuery(id+"F0.wireOp",EDGE,"E6.bottom");var subQ8=sQuery(id+"F0.wireOp",EDGE,"E9.right");var subQ9=sQuery(id+"F0.wireOp",EDGE,"E9.left");var subQ10=sQuery(id+"F0.wireOp",EDGE,"E9.top");var subQ11=sQuery(id+"F0.wireOp",EDGE,"E9.bottom");var subQ12=sQuery(id+"F0.wireOp",EDGE,"E8.right");var subQ13=sQuery(id+"F0.wireOp",EDGE,"E8.left");var subQ14=sQuery(id+"F0.wireOp",EDGE,"E8.top");var subQ15=sQuery(id+"F0.wireOp",EDGE,"E8.bottom");var subQ16=sQuery(id+"F0.wireOp",EDGE,"E11.right");var subQ17=sQuery(id+"F0.wireOp",EDGE,"E11.top");Q36=makeQuery(id+"F4.opFillet","BLEND_EDGE",EDGE,{"blendedFrom":[makeQuery(id+"F1.opExtrude","SWEPT_EDGE",EDGE,{"disambiguationData":[OSD([subQ17,subQ16])]}),makeQuery(id+"F2.boolean.opBoolean","MERGE",FACE,{"derivedFrom":[makeQuery(id+"F1.opExtrude","CAP_FACE",FACE,{"disambiguationData":[OSD([sQuery(id+"F0.wireOp",EDGE,"E0.bottom"),sQuery(id+"F0.wireOp",EDGE,"E5.bottom"),sQuery(id+"F0.wireOp",EDGE,"E5.top"),sQuery(id+"F0.wireOp",EDGE,"E5.left"),sQuery(id+"F0.wireOp",EDGE,"E5.right"),subQ7,subQ6,subQ5,subQ4,subQ3,subQ2,subQ1,subQ0,subQ15,subQ14,subQ13,subQ12,subQ11,subQ10,subQ9,subQ8,sQuery(id+"F0.wireOp",EDGE,"E10.bottom"),sQuery(id+"F0.wireOp",EDGE,"E10.top"),sQuery(id+"F0.wireOp",EDGE,"E10.left"),sQuery(id+"F0.wireOp",EDGE,"E10.right"),sQuery(id+"F0.wireOp",EDGE,"E11.bottom"),subQ17,sQuery(id+"F0.wireOp",EDGE,"E11.left"),subQ16,sQuery(id+"F0.wireOp",EDGE,"E12.bottom"),sQuery(id+"F0.wireOp",EDGE,"E12.top"),sQuery(id+"F0.wireOp",EDGE,"E12.left"),sQuery(id+"F0.wireOp",EDGE,"E12.right"),sQuery(id+"F0.wireOp",EDGE,"E13.bottom"),sQuery(id+"F0.wireOp",EDGE,"E13.top"),sQuery(id+"F0.wireOp",EDGE,"E13.left"),sQuery(id+"F0.wireOp",EDGE,"E13.right"),sQuery(id+"F0.wireOp",EDGE,"E14.bottom"),sQuery(id+"F0.wireOp",EDGE,"E14.top"),sQuery(id+"F0.wireOp",EDGE,"E14.left"),sQuery(id+"F0.wireOp",EDGE,"E14.right"),sQuery(id+"F0.wireOp",EDGE,"E15.bottom"),sQuery(id+"F0.wireOp",EDGE,"E15.top"),sQuery(id+"F0.wireOp",EDGE,"E15.left"),sQuery(id+"F0.wireOp",EDGE,"E15.right"),sQuery(id+"F0.wireOp",EDGE,"E16"),sQuery(id+"F0.wireOp",EDGE,"E17")])],"isStart":true}),makeQuery(id+"F2.opExtrude","CAP_FACE",FACE,{"disambiguationData":[OSD([sQuery(id+"F0.wireOp",EDGE,"E1"),subQ15,subQ14,subQ13,subQ12])],"isStart":true}),makeQuery(id+"F2.opExtrude","CAP_FACE",FACE,{"disambiguationData":[OSD([sQuery(id+"F0.wireOp",EDGE,"E2"),subQ11,subQ10,subQ9,subQ8])],"isStart":true}),makeQuery(id+"F2.opExtrude","CAP_FACE",FACE,{"disambiguationData":[OSD([sQuery(id+"F0.wireOp",EDGE,"E3"),subQ7,subQ6,subQ5,subQ4])],"isStart":true}),makeQuery(id+"F2.opExtrude","CAP_FACE",FACE,{"disambiguationData":[OSD([sQuery(id+"F0.wireOp",EDGE,"E4"),subQ3,subQ2,subQ1,subQ0])],"isStart":true})]})],"blendedInto":[makeQuery(id+"F2.boolean.opBoolean","MERGE",FACE,{"derivedFrom":[makeQuery(id+"F1.opExtrude","CAP_FACE",FACE,{"disambiguationData":[OSD([sQuery(id+"F0.wireOp",EDGE,"E0.bottom"),sQuery(id+"F0.wireOp",EDGE,"E5.bottom"),sQuery(id+"F0.wireOp",EDGE,"E5.top"),sQuery(id+"F0.wireOp",EDGE,"E5.left"),sQuery(id+"F0.wireOp",EDGE,"E5.right"),subQ7,subQ6,subQ5,subQ4,subQ3,subQ2,subQ1,subQ0,subQ15,subQ14,subQ13,subQ12,subQ11,subQ10,subQ9,subQ8,sQuery(id+"F0.wireOp",EDGE,"E10.bottom"),sQuery(id+"F0.wireOp",EDGE,"E10.top"),sQuery(id+"F0.wireOp",EDGE,"E10.left"),sQuery(id+"F0.wireOp",EDGE,"E10.right"),sQuery(id+"F0.wireOp",EDGE,"E11.bottom"),subQ17,sQuery(id+"F0.wireOp",EDGE,"E11.left"),subQ16,sQuery(id+"F0.wireOp",EDGE,"E12.bottom"),sQuery(id+"F0.wireOp",EDGE,"E12.top"),sQuery(id+"F0.wireOp",EDGE,"E12.left"),sQuery(id+"F0.wireOp",EDGE,"E12.right"),sQuery(id+"F0.wireOp",EDGE,"E13.bottom"),sQuery(id+"F0.wireOp",EDGE,"E13.top"),sQuery(id+"F0.wireOp",EDGE,"E13.left"),sQuery(id+"F0.wireOp",EDGE,"E13.right"),sQuery(id+"F0.wireOp",EDGE,"E14.bottom"),sQuery(id+"F0.wireOp",EDGE,"E14.top"),sQuery(id+"F0.wireOp",EDGE,"E14.left"),sQuery(id+"F0.wireOp",EDGE,"E14.right"),sQuery(id+"F0.wireOp",EDGE,"E15.bottom"),sQuery(id+"F0.wireOp",EDGE,"E15.top"),sQuery(id+"F0.wireOp",EDGE,"E15.left"),sQuery(id+"F0.wireOp",EDGE,"E15.right"),sQuery(id+"F0.wireOp",EDGE,"E16"),sQuery(id+"F0.wireOp",EDGE,"E17")])],"isStart":true}),makeQuery(id+"F2.opExtrude","CAP_FACE",FACE,{"disambiguationData":[OSD([sQuery(id+"F0.wireOp",EDGE,"E1"),subQ15,subQ14,subQ13,subQ12])],"isStart":true}),makeQuery(id+"F2.opExtrude","CAP_FACE",FACE,{"disambiguationData":[OSD([sQuery(id+"F0.wireOp",EDGE,"E2"),subQ11,subQ10,subQ9,subQ8])],"isStart":true}),makeQuery(id+"F2.opExtrude","CAP_FACE",FACE,{"disambiguationData":[OSD([sQuery(id+"F0.wireOp",EDGE,"E3"),subQ7,subQ6,subQ5,subQ4])],"isStart":true}),makeQuery(id+"F2.opExtrude","CAP_FACE",FACE,{"disambiguationData":[OSD([sQuery(id+"F0.wireOp",EDGE,"E4"),subQ3,subQ2,subQ1,subQ0])],"isStart":true})]})]});}
            var Q37;
            Q37=makeQuery(id+"F1.opExtrude","CAP_EDGE",EDGE,{"disambiguationData":[OSD([sQuery(id+"F0.wireOp",EDGE,"E11.bottom")])],"isStart":true});
            var Q38;
            Q38=makeQuery(id+"F1.opExtrude","CAP_EDGE",EDGE,{"disambiguationData":[OSD([sQuery(id+"F0.wireOp",EDGE,"E11.top")])],"isStart":true});
            var Q39;
            {var subQ0=sQuery(id+"F0.wireOp",EDGE,"E7.right");var subQ1=sQuery(id+"F0.wireOp",EDGE,"E7.left");var subQ2=sQuery(id+"F0.wireOp",EDGE,"E7.top");var subQ3=sQuery(id+"F0.wireOp",EDGE,"E7.bottom");var subQ4=sQuery(id+"F0.wireOp",EDGE,"E6.right");var subQ5=sQuery(id+"F0.wireOp",EDGE,"E6.left");var subQ6=sQuery(id+"F0.wireOp",EDGE,"E6.top");var subQ7=sQuery(id+"F0.wireOp",EDGE,"E6.bottom");var subQ8=sQuery(id+"F0.wireOp",EDGE,"E9.right");var subQ9=sQuery(id+"F0.wireOp",EDGE,"E9.left");var subQ10=sQuery(id+"F0.wireOp",EDGE,"E9.top");var subQ11=sQuery(id+"F0.wireOp",EDGE,"E9.bottom");var subQ12=sQuery(id+"F0.wireOp",EDGE,"E8.right");var subQ13=sQuery(id+"F0.wireOp",EDGE,"E8.left");var subQ14=sQuery(id+"F0.wireOp",EDGE,"E8.top");var subQ15=sQuery(id+"F0.wireOp",EDGE,"E8.bottom");var subQ16=sQuery(id+"F0.wireOp",EDGE,"E11.left");var subQ17=sQuery(id+"F0.wireOp",EDGE,"E11.bottom");Q39=makeQuery(id+"F4.opFillet","BLEND_EDGE",EDGE,{"blendedFrom":[makeQuery(id+"F1.opExtrude","SWEPT_EDGE",EDGE,{"disambiguationData":[OSD([subQ17,subQ16])]}),makeQuery(id+"F2.boolean.opBoolean","MERGE",FACE,{"derivedFrom":[makeQuery(id+"F1.opExtrude","CAP_FACE",FACE,{"disambiguationData":[OSD([sQuery(id+"F0.wireOp",EDGE,"E0.bottom"),sQuery(id+"F0.wireOp",EDGE,"E5.bottom"),sQuery(id+"F0.wireOp",EDGE,"E5.top"),sQuery(id+"F0.wireOp",EDGE,"E5.left"),sQuery(id+"F0.wireOp",EDGE,"E5.right"),subQ7,subQ6,subQ5,subQ4,subQ3,subQ2,subQ1,subQ0,subQ15,subQ14,subQ13,subQ12,subQ11,subQ10,subQ9,subQ8,sQuery(id+"F0.wireOp",EDGE,"E10.bottom"),sQuery(id+"F0.wireOp",EDGE,"E10.top"),sQuery(id+"F0.wireOp",EDGE,"E10.left"),sQuery(id+"F0.wireOp",EDGE,"E10.right"),subQ17,sQuery(id+"F0.wireOp",EDGE,"E11.top"),subQ16,sQuery(id+"F0.wireOp",EDGE,"E11.right"),sQuery(id+"F0.wireOp",EDGE,"E12.bottom"),sQuery(id+"F0.wireOp",EDGE,"E12.top"),sQuery(id+"F0.wireOp",EDGE,"E12.left"),sQuery(id+"F0.wireOp",EDGE,"E12.right"),sQuery(id+"F0.wireOp",EDGE,"E13.bottom"),sQuery(id+"F0.wireOp",EDGE,"E13.top"),sQuery(id+"F0.wireOp",EDGE,"E13.left"),sQuery(id+"F0.wireOp",EDGE,"E13.right"),sQuery(id+"F0.wireOp",EDGE,"E14.bottom"),sQuery(id+"F0.wireOp",EDGE,"E14.top"),sQuery(id+"F0.wireOp",EDGE,"E14.left"),sQuery(id+"F0.wireOp",EDGE,"E14.right"),sQuery(id+"F0.wireOp",EDGE,"E15.bottom"),sQuery(id+"F0.wireOp",EDGE,"E15.top"),sQuery(id+"F0.wireOp",EDGE,"E15.left"),sQuery(id+"F0.wireOp",EDGE,"E15.right"),sQuery(id+"F0.wireOp",EDGE,"E16"),sQuery(id+"F0.wireOp",EDGE,"E17")])],"isStart":true}),makeQuery(id+"F2.opExtrude","CAP_FACE",FACE,{"disambiguationData":[OSD([sQuery(id+"F0.wireOp",EDGE,"E1"),subQ15,subQ14,subQ13,subQ12])],"isStart":true}),makeQuery(id+"F2.opExtrude","CAP_FACE",FACE,{"disambiguationData":[OSD([sQuery(id+"F0.wireOp",EDGE,"E2"),subQ11,subQ10,subQ9,subQ8])],"isStart":true}),makeQuery(id+"F2.opExtrude","CAP_FACE",FACE,{"disambiguationData":[OSD([sQuery(id+"F0.wireOp",EDGE,"E3"),subQ7,subQ6,subQ5,subQ4])],"isStart":true}),makeQuery(id+"F2.opExtrude","CAP_FACE",FACE,{"disambiguationData":[OSD([sQuery(id+"F0.wireOp",EDGE,"E4"),subQ3,subQ2,subQ1,subQ0])],"isStart":true})]})],"blendedInto":[makeQuery(id+"F2.boolean.opBoolean","MERGE",FACE,{"derivedFrom":[makeQuery(id+"F1.opExtrude","CAP_FACE",FACE,{"disambiguationData":[OSD([sQuery(id+"F0.wireOp",EDGE,"E0.bottom"),sQuery(id+"F0.wireOp",EDGE,"E5.bottom"),sQuery(id+"F0.wireOp",EDGE,"E5.top"),sQuery(id+"F0.wireOp",EDGE,"E5.left"),sQuery(id+"F0.wireOp",EDGE,"E5.right"),subQ7,subQ6,subQ5,subQ4,subQ3,subQ2,subQ1,subQ0,subQ15,subQ14,subQ13,subQ12,subQ11,subQ10,subQ9,subQ8,sQuery(id+"F0.wireOp",EDGE,"E10.bottom"),sQuery(id+"F0.wireOp",EDGE,"E10.top"),sQuery(id+"F0.wireOp",EDGE,"E10.left"),sQuery(id+"F0.wireOp",EDGE,"E10.right"),subQ17,sQuery(id+"F0.wireOp",EDGE,"E11.top"),subQ16,sQuery(id+"F0.wireOp",EDGE,"E11.right"),sQuery(id+"F0.wireOp",EDGE,"E12.bottom"),sQuery(id+"F0.wireOp",EDGE,"E12.top"),sQuery(id+"F0.wireOp",EDGE,"E12.left"),sQuery(id+"F0.wireOp",EDGE,"E12.right"),sQuery(id+"F0.wireOp",EDGE,"E13.bottom"),sQuery(id+"F0.wireOp",EDGE,"E13.top"),sQuery(id+"F0.wireOp",EDGE,"E13.left"),sQuery(id+"F0.wireOp",EDGE,"E13.right"),sQuery(id+"F0.wireOp",EDGE,"E14.bottom"),sQuery(id+"F0.wireOp",EDGE,"E14.top"),sQuery(id+"F0.wireOp",EDGE,"E14.left"),sQuery(id+"F0.wireOp",EDGE,"E14.right"),sQuery(id+"F0.wireOp",EDGE,"E15.bottom"),sQuery(id+"F0.wireOp",EDGE,"E15.top"),sQuery(id+"F0.wireOp",EDGE,"E15.left"),sQuery(id+"F0.wireOp",EDGE,"E15.right"),sQuery(id+"F0.wireOp",EDGE,"E16"),sQuery(id+"F0.wireOp",EDGE,"E17")])],"isStart":true}),makeQuery(id+"F2.opExtrude","CAP_FACE",FACE,{"disambiguationData":[OSD([sQuery(id+"F0.wireOp",EDGE,"E1"),subQ15,subQ14,subQ13,subQ12])],"isStart":true}),makeQuery(id+"F2.opExtrude","CAP_FACE",FACE,{"disambiguationData":[OSD([sQuery(id+"F0.wireOp",EDGE,"E2"),subQ11,subQ10,subQ9,subQ8])],"isStart":true}),makeQuery(id+"F2.opExtrude","CAP_FACE",FACE,{"disambiguationData":[OSD([sQuery(id+"F0.wireOp",EDGE,"E3"),subQ7,subQ6,subQ5,subQ4])],"isStart":true}),makeQuery(id+"F2.opExtrude","CAP_FACE",FACE,{"disambiguationData":[OSD([sQuery(id+"F0.wireOp",EDGE,"E4"),subQ3,subQ2,subQ1,subQ0])],"isStart":true})]})]});}
            var Q40;
            Q40=makeQuery(id+"F1.opExtrude","CAP_EDGE",EDGE,{"disambiguationData":[OSD([sQuery(id+"F0.wireOp",EDGE,"E10.bottom")])],"isStart":true});
            var Q41;
            {var subQ0=sQuery(id+"F0.wireOp",EDGE,"E7.right");var subQ1=sQuery(id+"F0.wireOp",EDGE,"E7.left");var subQ2=sQuery(id+"F0.wireOp",EDGE,"E7.top");var subQ3=sQuery(id+"F0.wireOp",EDGE,"E7.bottom");var subQ4=sQuery(id+"F0.wireOp",EDGE,"E6.right");var subQ5=sQuery(id+"F0.wireOp",EDGE,"E6.left");var subQ6=sQuery(id+"F0.wireOp",EDGE,"E6.top");var subQ7=sQuery(id+"F0.wireOp",EDGE,"E6.bottom");var subQ8=sQuery(id+"F0.wireOp",EDGE,"E9.right");var subQ9=sQuery(id+"F0.wireOp",EDGE,"E9.left");var subQ10=sQuery(id+"F0.wireOp",EDGE,"E9.top");var subQ11=sQuery(id+"F0.wireOp",EDGE,"E9.bottom");var subQ12=sQuery(id+"F0.wireOp",EDGE,"E8.right");var subQ13=sQuery(id+"F0.wireOp",EDGE,"E8.left");var subQ14=sQuery(id+"F0.wireOp",EDGE,"E8.top");var subQ15=sQuery(id+"F0.wireOp",EDGE,"E8.bottom");var subQ16=sQuery(id+"F0.wireOp",EDGE,"E10.left");var subQ17=sQuery(id+"F0.wireOp",EDGE,"E10.bottom");Q41=makeQuery(id+"F4.opFillet","BLEND_EDGE",EDGE,{"blendedFrom":[makeQuery(id+"F1.opExtrude","SWEPT_EDGE",EDGE,{"disambiguationData":[OSD([subQ17,subQ16])]}),makeQuery(id+"F2.boolean.opBoolean","MERGE",FACE,{"derivedFrom":[makeQuery(id+"F1.opExtrude","CAP_FACE",FACE,{"disambiguationData":[OSD([sQuery(id+"F0.wireOp",EDGE,"E0.bottom"),sQuery(id+"F0.wireOp",EDGE,"E5.bottom"),sQuery(id+"F0.wireOp",EDGE,"E5.top"),sQuery(id+"F0.wireOp",EDGE,"E5.left"),sQuery(id+"F0.wireOp",EDGE,"E5.right"),subQ7,subQ6,subQ5,subQ4,subQ3,subQ2,subQ1,subQ0,subQ15,subQ14,subQ13,subQ12,subQ11,subQ10,subQ9,subQ8,subQ17,sQuery(id+"F0.wireOp",EDGE,"E10.top"),subQ16,sQuery(id+"F0.wireOp",EDGE,"E10.right"),sQuery(id+"F0.wireOp",EDGE,"E11.bottom"),sQuery(id+"F0.wireOp",EDGE,"E11.top"),sQuery(id+"F0.wireOp",EDGE,"E11.left"),sQuery(id+"F0.wireOp",EDGE,"E11.right"),sQuery(id+"F0.wireOp",EDGE,"E12.bottom"),sQuery(id+"F0.wireOp",EDGE,"E12.top"),sQuery(id+"F0.wireOp",EDGE,"E12.left"),sQuery(id+"F0.wireOp",EDGE,"E12.right"),sQuery(id+"F0.wireOp",EDGE,"E13.bottom"),sQuery(id+"F0.wireOp",EDGE,"E13.top"),sQuery(id+"F0.wireOp",EDGE,"E13.left"),sQuery(id+"F0.wireOp",EDGE,"E13.right"),sQuery(id+"F0.wireOp",EDGE,"E14.bottom"),sQuery(id+"F0.wireOp",EDGE,"E14.top"),sQuery(id+"F0.wireOp",EDGE,"E14.left"),sQuery(id+"F0.wireOp",EDGE,"E14.right"),sQuery(id+"F0.wireOp",EDGE,"E15.bottom"),sQuery(id+"F0.wireOp",EDGE,"E15.top"),sQuery(id+"F0.wireOp",EDGE,"E15.left"),sQuery(id+"F0.wireOp",EDGE,"E15.right"),sQuery(id+"F0.wireOp",EDGE,"E16"),sQuery(id+"F0.wireOp",EDGE,"E17")])],"isStart":true}),makeQuery(id+"F2.opExtrude","CAP_FACE",FACE,{"disambiguationData":[OSD([sQuery(id+"F0.wireOp",EDGE,"E1"),subQ15,subQ14,subQ13,subQ12])],"isStart":true}),makeQuery(id+"F2.opExtrude","CAP_FACE",FACE,{"disambiguationData":[OSD([sQuery(id+"F0.wireOp",EDGE,"E2"),subQ11,subQ10,subQ9,subQ8])],"isStart":true}),makeQuery(id+"F2.opExtrude","CAP_FACE",FACE,{"disambiguationData":[OSD([sQuery(id+"F0.wireOp",EDGE,"E3"),subQ7,subQ6,subQ5,subQ4])],"isStart":true}),makeQuery(id+"F2.opExtrude","CAP_FACE",FACE,{"disambiguationData":[OSD([sQuery(id+"F0.wireOp",EDGE,"E4"),subQ3,subQ2,subQ1,subQ0])],"isStart":true})]})],"blendedInto":[makeQuery(id+"F2.boolean.opBoolean","MERGE",FACE,{"derivedFrom":[makeQuery(id+"F1.opExtrude","CAP_FACE",FACE,{"disambiguationData":[OSD([sQuery(id+"F0.wireOp",EDGE,"E0.bottom"),sQuery(id+"F0.wireOp",EDGE,"E5.bottom"),sQuery(id+"F0.wireOp",EDGE,"E5.top"),sQuery(id+"F0.wireOp",EDGE,"E5.left"),sQuery(id+"F0.wireOp",EDGE,"E5.right"),subQ7,subQ6,subQ5,subQ4,subQ3,subQ2,subQ1,subQ0,subQ15,subQ14,subQ13,subQ12,subQ11,subQ10,subQ9,subQ8,subQ17,sQuery(id+"F0.wireOp",EDGE,"E10.top"),subQ16,sQuery(id+"F0.wireOp",EDGE,"E10.right"),sQuery(id+"F0.wireOp",EDGE,"E11.bottom"),sQuery(id+"F0.wireOp",EDGE,"E11.top"),sQuery(id+"F0.wireOp",EDGE,"E11.left"),sQuery(id+"F0.wireOp",EDGE,"E11.right"),sQuery(id+"F0.wireOp",EDGE,"E12.bottom"),sQuery(id+"F0.wireOp",EDGE,"E12.top"),sQuery(id+"F0.wireOp",EDGE,"E12.left"),sQuery(id+"F0.wireOp",EDGE,"E12.right"),sQuery(id+"F0.wireOp",EDGE,"E13.bottom"),sQuery(id+"F0.wireOp",EDGE,"E13.top"),sQuery(id+"F0.wireOp",EDGE,"E13.left"),sQuery(id+"F0.wireOp",EDGE,"E13.right"),sQuery(id+"F0.wireOp",EDGE,"E14.bottom"),sQuery(id+"F0.wireOp",EDGE,"E14.top"),sQuery(id+"F0.wireOp",EDGE,"E14.left"),sQuery(id+"F0.wireOp",EDGE,"E14.right"),sQuery(id+"F0.wireOp",EDGE,"E15.bottom"),sQuery(id+"F0.wireOp",EDGE,"E15.top"),sQuery(id+"F0.wireOp",EDGE,"E15.left"),sQuery(id+"F0.wireOp",EDGE,"E15.right"),sQuery(id+"F0.wireOp",EDGE,"E16"),sQuery(id+"F0.wireOp",EDGE,"E17")])],"isStart":true}),makeQuery(id+"F2.opExtrude","CAP_FACE",FACE,{"disambiguationData":[OSD([sQuery(id+"F0.wireOp",EDGE,"E1"),subQ15,subQ14,subQ13,subQ12])],"isStart":true}),makeQuery(id+"F2.opExtrude","CAP_FACE",FACE,{"disambiguationData":[OSD([sQuery(id+"F0.wireOp",EDGE,"E2"),subQ11,subQ10,subQ9,subQ8])],"isStart":true}),makeQuery(id+"F2.opExtrude","CAP_FACE",FACE,{"disambiguationData":[OSD([sQuery(id+"F0.wireOp",EDGE,"E3"),subQ7,subQ6,subQ5,subQ4])],"isStart":true}),makeQuery(id+"F2.opExtrude","CAP_FACE",FACE,{"disambiguationData":[OSD([sQuery(id+"F0.wireOp",EDGE,"E4"),subQ3,subQ2,subQ1,subQ0])],"isStart":true})]})]});}
            var Q42;
            Q42=makeQuery(id+"F1.opExtrude","CAP_EDGE",EDGE,{"disambiguationData":[OSD([sQuery(id+"F0.wireOp",EDGE,"E10.top")])],"isStart":true});
            var Q43;
            {var subQ0=sQuery(id+"F0.wireOp",EDGE,"E7.right");var subQ1=sQuery(id+"F0.wireOp",EDGE,"E7.left");var subQ2=sQuery(id+"F0.wireOp",EDGE,"E7.top");var subQ3=sQuery(id+"F0.wireOp",EDGE,"E7.bottom");var subQ4=sQuery(id+"F0.wireOp",EDGE,"E6.right");var subQ5=sQuery(id+"F0.wireOp",EDGE,"E6.left");var subQ6=sQuery(id+"F0.wireOp",EDGE,"E6.top");var subQ7=sQuery(id+"F0.wireOp",EDGE,"E6.bottom");var subQ8=sQuery(id+"F0.wireOp",EDGE,"E9.right");var subQ9=sQuery(id+"F0.wireOp",EDGE,"E9.left");var subQ10=sQuery(id+"F0.wireOp",EDGE,"E9.top");var subQ11=sQuery(id+"F0.wireOp",EDGE,"E9.bottom");var subQ12=sQuery(id+"F0.wireOp",EDGE,"E8.right");var subQ13=sQuery(id+"F0.wireOp",EDGE,"E8.left");var subQ14=sQuery(id+"F0.wireOp",EDGE,"E8.top");var subQ15=sQuery(id+"F0.wireOp",EDGE,"E8.bottom");var subQ16=sQuery(id+"F0.wireOp",EDGE,"E10.right");var subQ17=sQuery(id+"F0.wireOp",EDGE,"E10.top");Q43=makeQuery(id+"F4.opFillet","BLEND_EDGE",EDGE,{"blendedFrom":[makeQuery(id+"F1.opExtrude","SWEPT_EDGE",EDGE,{"disambiguationData":[OSD([subQ17,subQ16])]}),makeQuery(id+"F2.boolean.opBoolean","MERGE",FACE,{"derivedFrom":[makeQuery(id+"F1.opExtrude","CAP_FACE",FACE,{"disambiguationData":[OSD([sQuery(id+"F0.wireOp",EDGE,"E0.bottom"),sQuery(id+"F0.wireOp",EDGE,"E5.bottom"),sQuery(id+"F0.wireOp",EDGE,"E5.top"),sQuery(id+"F0.wireOp",EDGE,"E5.left"),sQuery(id+"F0.wireOp",EDGE,"E5.right"),subQ7,subQ6,subQ5,subQ4,subQ3,subQ2,subQ1,subQ0,subQ15,subQ14,subQ13,subQ12,subQ11,subQ10,subQ9,subQ8,sQuery(id+"F0.wireOp",EDGE,"E10.bottom"),subQ17,sQuery(id+"F0.wireOp",EDGE,"E10.left"),subQ16,sQuery(id+"F0.wireOp",EDGE,"E11.bottom"),sQuery(id+"F0.wireOp",EDGE,"E11.top"),sQuery(id+"F0.wireOp",EDGE,"E11.left"),sQuery(id+"F0.wireOp",EDGE,"E11.right"),sQuery(id+"F0.wireOp",EDGE,"E12.bottom"),sQuery(id+"F0.wireOp",EDGE,"E12.top"),sQuery(id+"F0.wireOp",EDGE,"E12.left"),sQuery(id+"F0.wireOp",EDGE,"E12.right"),sQuery(id+"F0.wireOp",EDGE,"E13.bottom"),sQuery(id+"F0.wireOp",EDGE,"E13.top"),sQuery(id+"F0.wireOp",EDGE,"E13.left"),sQuery(id+"F0.wireOp",EDGE,"E13.right"),sQuery(id+"F0.wireOp",EDGE,"E14.bottom"),sQuery(id+"F0.wireOp",EDGE,"E14.top"),sQuery(id+"F0.wireOp",EDGE,"E14.left"),sQuery(id+"F0.wireOp",EDGE,"E14.right"),sQuery(id+"F0.wireOp",EDGE,"E15.bottom"),sQuery(id+"F0.wireOp",EDGE,"E15.top"),sQuery(id+"F0.wireOp",EDGE,"E15.left"),sQuery(id+"F0.wireOp",EDGE,"E15.right"),sQuery(id+"F0.wireOp",EDGE,"E16"),sQuery(id+"F0.wireOp",EDGE,"E17")])],"isStart":true}),makeQuery(id+"F2.opExtrude","CAP_FACE",FACE,{"disambiguationData":[OSD([sQuery(id+"F0.wireOp",EDGE,"E1"),subQ15,subQ14,subQ13,subQ12])],"isStart":true}),makeQuery(id+"F2.opExtrude","CAP_FACE",FACE,{"disambiguationData":[OSD([sQuery(id+"F0.wireOp",EDGE,"E2"),subQ11,subQ10,subQ9,subQ8])],"isStart":true}),makeQuery(id+"F2.opExtrude","CAP_FACE",FACE,{"disambiguationData":[OSD([sQuery(id+"F0.wireOp",EDGE,"E3"),subQ7,subQ6,subQ5,subQ4])],"isStart":true}),makeQuery(id+"F2.opExtrude","CAP_FACE",FACE,{"disambiguationData":[OSD([sQuery(id+"F0.wireOp",EDGE,"E4"),subQ3,subQ2,subQ1,subQ0])],"isStart":true})]})],"blendedInto":[makeQuery(id+"F2.boolean.opBoolean","MERGE",FACE,{"derivedFrom":[makeQuery(id+"F1.opExtrude","CAP_FACE",FACE,{"disambiguationData":[OSD([sQuery(id+"F0.wireOp",EDGE,"E0.bottom"),sQuery(id+"F0.wireOp",EDGE,"E5.bottom"),sQuery(id+"F0.wireOp",EDGE,"E5.top"),sQuery(id+"F0.wireOp",EDGE,"E5.left"),sQuery(id+"F0.wireOp",EDGE,"E5.right"),subQ7,subQ6,subQ5,subQ4,subQ3,subQ2,subQ1,subQ0,subQ15,subQ14,subQ13,subQ12,subQ11,subQ10,subQ9,subQ8,sQuery(id+"F0.wireOp",EDGE,"E10.bottom"),subQ17,sQuery(id+"F0.wireOp",EDGE,"E10.left"),subQ16,sQuery(id+"F0.wireOp",EDGE,"E11.bottom"),sQuery(id+"F0.wireOp",EDGE,"E11.top"),sQuery(id+"F0.wireOp",EDGE,"E11.left"),sQuery(id+"F0.wireOp",EDGE,"E11.right"),sQuery(id+"F0.wireOp",EDGE,"E12.bottom"),sQuery(id+"F0.wireOp",EDGE,"E12.top"),sQuery(id+"F0.wireOp",EDGE,"E12.left"),sQuery(id+"F0.wireOp",EDGE,"E12.right"),sQuery(id+"F0.wireOp",EDGE,"E13.bottom"),sQuery(id+"F0.wireOp",EDGE,"E13.top"),sQuery(id+"F0.wireOp",EDGE,"E13.left"),sQuery(id+"F0.wireOp",EDGE,"E13.right"),sQuery(id+"F0.wireOp",EDGE,"E14.bottom"),sQuery(id+"F0.wireOp",EDGE,"E14.top"),sQuery(id+"F0.wireOp",EDGE,"E14.left"),sQuery(id+"F0.wireOp",EDGE,"E14.right"),sQuery(id+"F0.wireOp",EDGE,"E15.bottom"),sQuery(id+"F0.wireOp",EDGE,"E15.top"),sQuery(id+"F0.wireOp",EDGE,"E15.left"),sQuery(id+"F0.wireOp",EDGE,"E15.right"),sQuery(id+"F0.wireOp",EDGE,"E16"),sQuery(id+"F0.wireOp",EDGE,"E17")])],"isStart":true}),makeQuery(id+"F2.opExtrude","CAP_FACE",FACE,{"disambiguationData":[OSD([sQuery(id+"F0.wireOp",EDGE,"E1"),subQ15,subQ14,subQ13,subQ12])],"isStart":true}),makeQuery(id+"F2.opExtrude","CAP_FACE",FACE,{"disambiguationData":[OSD([sQuery(id+"F0.wireOp",EDGE,"E2"),subQ11,subQ10,subQ9,subQ8])],"isStart":true}),makeQuery(id+"F2.opExtrude","CAP_FACE",FACE,{"disambiguationData":[OSD([sQuery(id+"F0.wireOp",EDGE,"E3"),subQ7,subQ6,subQ5,subQ4])],"isStart":true}),makeQuery(id+"F2.opExtrude","CAP_FACE",FACE,{"disambiguationData":[OSD([sQuery(id+"F0.wireOp",EDGE,"E4"),subQ3,subQ2,subQ1,subQ0])],"isStart":true})]})]});}
            var Q44;
            Q44=makeQuery(id+"F1.opExtrude","CAP_EDGE",EDGE,{"disambiguationData":[OSD([sQuery(id+"F0.wireOp",EDGE,"E12.bottom")])],"isStart":true});
            var Q45;
            {var subQ0=sQuery(id+"F0.wireOp",EDGE,"E7.right");var subQ1=sQuery(id+"F0.wireOp",EDGE,"E7.left");var subQ2=sQuery(id+"F0.wireOp",EDGE,"E7.top");var subQ3=sQuery(id+"F0.wireOp",EDGE,"E7.bottom");var subQ4=sQuery(id+"F0.wireOp",EDGE,"E6.right");var subQ5=sQuery(id+"F0.wireOp",EDGE,"E6.left");var subQ6=sQuery(id+"F0.wireOp",EDGE,"E6.top");var subQ7=sQuery(id+"F0.wireOp",EDGE,"E6.bottom");var subQ8=sQuery(id+"F0.wireOp",EDGE,"E9.right");var subQ9=sQuery(id+"F0.wireOp",EDGE,"E9.left");var subQ10=sQuery(id+"F0.wireOp",EDGE,"E9.top");var subQ11=sQuery(id+"F0.wireOp",EDGE,"E9.bottom");var subQ12=sQuery(id+"F0.wireOp",EDGE,"E8.right");var subQ13=sQuery(id+"F0.wireOp",EDGE,"E8.left");var subQ14=sQuery(id+"F0.wireOp",EDGE,"E8.top");var subQ15=sQuery(id+"F0.wireOp",EDGE,"E8.bottom");var subQ16=sQuery(id+"F0.wireOp",EDGE,"E12.right");var subQ17=sQuery(id+"F0.wireOp",EDGE,"E12.top");Q45=makeQuery(id+"F4.opFillet","BLEND_EDGE",EDGE,{"blendedFrom":[makeQuery(id+"F1.opExtrude","SWEPT_EDGE",EDGE,{"disambiguationData":[OSD([subQ17,subQ16])]}),makeQuery(id+"F2.boolean.opBoolean","MERGE",FACE,{"derivedFrom":[makeQuery(id+"F1.opExtrude","CAP_FACE",FACE,{"disambiguationData":[OSD([sQuery(id+"F0.wireOp",EDGE,"E0.bottom"),sQuery(id+"F0.wireOp",EDGE,"E5.bottom"),sQuery(id+"F0.wireOp",EDGE,"E5.top"),sQuery(id+"F0.wireOp",EDGE,"E5.left"),sQuery(id+"F0.wireOp",EDGE,"E5.right"),subQ7,subQ6,subQ5,subQ4,subQ3,subQ2,subQ1,subQ0,subQ15,subQ14,subQ13,subQ12,subQ11,subQ10,subQ9,subQ8,sQuery(id+"F0.wireOp",EDGE,"E10.bottom"),sQuery(id+"F0.wireOp",EDGE,"E10.top"),sQuery(id+"F0.wireOp",EDGE,"E10.left"),sQuery(id+"F0.wireOp",EDGE,"E10.right"),sQuery(id+"F0.wireOp",EDGE,"E11.bottom"),sQuery(id+"F0.wireOp",EDGE,"E11.top"),sQuery(id+"F0.wireOp",EDGE,"E11.left"),sQuery(id+"F0.wireOp",EDGE,"E11.right"),sQuery(id+"F0.wireOp",EDGE,"E12.bottom"),subQ17,sQuery(id+"F0.wireOp",EDGE,"E12.left"),subQ16,sQuery(id+"F0.wireOp",EDGE,"E13.bottom"),sQuery(id+"F0.wireOp",EDGE,"E13.top"),sQuery(id+"F0.wireOp",EDGE,"E13.left"),sQuery(id+"F0.wireOp",EDGE,"E13.right"),sQuery(id+"F0.wireOp",EDGE,"E14.bottom"),sQuery(id+"F0.wireOp",EDGE,"E14.top"),sQuery(id+"F0.wireOp",EDGE,"E14.left"),sQuery(id+"F0.wireOp",EDGE,"E14.right"),sQuery(id+"F0.wireOp",EDGE,"E15.bottom"),sQuery(id+"F0.wireOp",EDGE,"E15.top"),sQuery(id+"F0.wireOp",EDGE,"E15.left"),sQuery(id+"F0.wireOp",EDGE,"E15.right"),sQuery(id+"F0.wireOp",EDGE,"E16"),sQuery(id+"F0.wireOp",EDGE,"E17")])],"isStart":true}),makeQuery(id+"F2.opExtrude","CAP_FACE",FACE,{"disambiguationData":[OSD([sQuery(id+"F0.wireOp",EDGE,"E1"),subQ15,subQ14,subQ13,subQ12])],"isStart":true}),makeQuery(id+"F2.opExtrude","CAP_FACE",FACE,{"disambiguationData":[OSD([sQuery(id+"F0.wireOp",EDGE,"E2"),subQ11,subQ10,subQ9,subQ8])],"isStart":true}),makeQuery(id+"F2.opExtrude","CAP_FACE",FACE,{"disambiguationData":[OSD([sQuery(id+"F0.wireOp",EDGE,"E3"),subQ7,subQ6,subQ5,subQ4])],"isStart":true}),makeQuery(id+"F2.opExtrude","CAP_FACE",FACE,{"disambiguationData":[OSD([sQuery(id+"F0.wireOp",EDGE,"E4"),subQ3,subQ2,subQ1,subQ0])],"isStart":true})]})],"blendedInto":[makeQuery(id+"F2.boolean.opBoolean","MERGE",FACE,{"derivedFrom":[makeQuery(id+"F1.opExtrude","CAP_FACE",FACE,{"disambiguationData":[OSD([sQuery(id+"F0.wireOp",EDGE,"E0.bottom"),sQuery(id+"F0.wireOp",EDGE,"E5.bottom"),sQuery(id+"F0.wireOp",EDGE,"E5.top"),sQuery(id+"F0.wireOp",EDGE,"E5.left"),sQuery(id+"F0.wireOp",EDGE,"E5.right"),subQ7,subQ6,subQ5,subQ4,subQ3,subQ2,subQ1,subQ0,subQ15,subQ14,subQ13,subQ12,subQ11,subQ10,subQ9,subQ8,sQuery(id+"F0.wireOp",EDGE,"E10.bottom"),sQuery(id+"F0.wireOp",EDGE,"E10.top"),sQuery(id+"F0.wireOp",EDGE,"E10.left"),sQuery(id+"F0.wireOp",EDGE,"E10.right"),sQuery(id+"F0.wireOp",EDGE,"E11.bottom"),sQuery(id+"F0.wireOp",EDGE,"E11.top"),sQuery(id+"F0.wireOp",EDGE,"E11.left"),sQuery(id+"F0.wireOp",EDGE,"E11.right"),sQuery(id+"F0.wireOp",EDGE,"E12.bottom"),subQ17,sQuery(id+"F0.wireOp",EDGE,"E12.left"),subQ16,sQuery(id+"F0.wireOp",EDGE,"E13.bottom"),sQuery(id+"F0.wireOp",EDGE,"E13.top"),sQuery(id+"F0.wireOp",EDGE,"E13.left"),sQuery(id+"F0.wireOp",EDGE,"E13.right"),sQuery(id+"F0.wireOp",EDGE,"E14.bottom"),sQuery(id+"F0.wireOp",EDGE,"E14.top"),sQuery(id+"F0.wireOp",EDGE,"E14.left"),sQuery(id+"F0.wireOp",EDGE,"E14.right"),sQuery(id+"F0.wireOp",EDGE,"E15.bottom"),sQuery(id+"F0.wireOp",EDGE,"E15.top"),sQuery(id+"F0.wireOp",EDGE,"E15.left"),sQuery(id+"F0.wireOp",EDGE,"E15.right"),sQuery(id+"F0.wireOp",EDGE,"E16"),sQuery(id+"F0.wireOp",EDGE,"E17")])],"isStart":true}),makeQuery(id+"F2.opExtrude","CAP_FACE",FACE,{"disambiguationData":[OSD([sQuery(id+"F0.wireOp",EDGE,"E1"),subQ15,subQ14,subQ13,subQ12])],"isStart":true}),makeQuery(id+"F2.opExtrude","CAP_FACE",FACE,{"disambiguationData":[OSD([sQuery(id+"F0.wireOp",EDGE,"E2"),subQ11,subQ10,subQ9,subQ8])],"isStart":true}),makeQuery(id+"F2.opExtrude","CAP_FACE",FACE,{"disambiguationData":[OSD([sQuery(id+"F0.wireOp",EDGE,"E3"),subQ7,subQ6,subQ5,subQ4])],"isStart":true}),makeQuery(id+"F2.opExtrude","CAP_FACE",FACE,{"disambiguationData":[OSD([sQuery(id+"F0.wireOp",EDGE,"E4"),subQ3,subQ2,subQ1,subQ0])],"isStart":true})]})]});}
            var Q46;
            Q46=makeQuery(id+"F1.opExtrude","CAP_EDGE",EDGE,{"disambiguationData":[OSD([sQuery(id+"F0.wireOp",EDGE,"E12.top")])],"isStart":true});
            var Q47;
            {var subQ0=sQuery(id+"F0.wireOp",EDGE,"E7.right");var subQ1=sQuery(id+"F0.wireOp",EDGE,"E7.left");var subQ2=sQuery(id+"F0.wireOp",EDGE,"E7.top");var subQ3=sQuery(id+"F0.wireOp",EDGE,"E7.bottom");var subQ4=sQuery(id+"F0.wireOp",EDGE,"E6.right");var subQ5=sQuery(id+"F0.wireOp",EDGE,"E6.left");var subQ6=sQuery(id+"F0.wireOp",EDGE,"E6.top");var subQ7=sQuery(id+"F0.wireOp",EDGE,"E6.bottom");var subQ8=sQuery(id+"F0.wireOp",EDGE,"E9.right");var subQ9=sQuery(id+"F0.wireOp",EDGE,"E9.left");var subQ10=sQuery(id+"F0.wireOp",EDGE,"E9.top");var subQ11=sQuery(id+"F0.wireOp",EDGE,"E9.bottom");var subQ12=sQuery(id+"F0.wireOp",EDGE,"E8.right");var subQ13=sQuery(id+"F0.wireOp",EDGE,"E8.left");var subQ14=sQuery(id+"F0.wireOp",EDGE,"E8.top");var subQ15=sQuery(id+"F0.wireOp",EDGE,"E8.bottom");var subQ16=sQuery(id+"F0.wireOp",EDGE,"E12.left");var subQ17=sQuery(id+"F0.wireOp",EDGE,"E12.bottom");Q47=makeQuery(id+"F4.opFillet","BLEND_EDGE",EDGE,{"blendedFrom":[makeQuery(id+"F1.opExtrude","SWEPT_EDGE",EDGE,{"disambiguationData":[OSD([subQ17,subQ16])]}),makeQuery(id+"F2.boolean.opBoolean","MERGE",FACE,{"derivedFrom":[makeQuery(id+"F1.opExtrude","CAP_FACE",FACE,{"disambiguationData":[OSD([sQuery(id+"F0.wireOp",EDGE,"E0.bottom"),sQuery(id+"F0.wireOp",EDGE,"E5.bottom"),sQuery(id+"F0.wireOp",EDGE,"E5.top"),sQuery(id+"F0.wireOp",EDGE,"E5.left"),sQuery(id+"F0.wireOp",EDGE,"E5.right"),subQ7,subQ6,subQ5,subQ4,subQ3,subQ2,subQ1,subQ0,subQ15,subQ14,subQ13,subQ12,subQ11,subQ10,subQ9,subQ8,sQuery(id+"F0.wireOp",EDGE,"E10.bottom"),sQuery(id+"F0.wireOp",EDGE,"E10.top"),sQuery(id+"F0.wireOp",EDGE,"E10.left"),sQuery(id+"F0.wireOp",EDGE,"E10.right"),sQuery(id+"F0.wireOp",EDGE,"E11.bottom"),sQuery(id+"F0.wireOp",EDGE,"E11.top"),sQuery(id+"F0.wireOp",EDGE,"E11.left"),sQuery(id+"F0.wireOp",EDGE,"E11.right"),subQ17,sQuery(id+"F0.wireOp",EDGE,"E12.top"),subQ16,sQuery(id+"F0.wireOp",EDGE,"E12.right"),sQuery(id+"F0.wireOp",EDGE,"E13.bottom"),sQuery(id+"F0.wireOp",EDGE,"E13.top"),sQuery(id+"F0.wireOp",EDGE,"E13.left"),sQuery(id+"F0.wireOp",EDGE,"E13.right"),sQuery(id+"F0.wireOp",EDGE,"E14.bottom"),sQuery(id+"F0.wireOp",EDGE,"E14.top"),sQuery(id+"F0.wireOp",EDGE,"E14.left"),sQuery(id+"F0.wireOp",EDGE,"E14.right"),sQuery(id+"F0.wireOp",EDGE,"E15.bottom"),sQuery(id+"F0.wireOp",EDGE,"E15.top"),sQuery(id+"F0.wireOp",EDGE,"E15.left"),sQuery(id+"F0.wireOp",EDGE,"E15.right"),sQuery(id+"F0.wireOp",EDGE,"E16"),sQuery(id+"F0.wireOp",EDGE,"E17")])],"isStart":true}),makeQuery(id+"F2.opExtrude","CAP_FACE",FACE,{"disambiguationData":[OSD([sQuery(id+"F0.wireOp",EDGE,"E1"),subQ15,subQ14,subQ13,subQ12])],"isStart":true}),makeQuery(id+"F2.opExtrude","CAP_FACE",FACE,{"disambiguationData":[OSD([sQuery(id+"F0.wireOp",EDGE,"E2"),subQ11,subQ10,subQ9,subQ8])],"isStart":true}),makeQuery(id+"F2.opExtrude","CAP_FACE",FACE,{"disambiguationData":[OSD([sQuery(id+"F0.wireOp",EDGE,"E3"),subQ7,subQ6,subQ5,subQ4])],"isStart":true}),makeQuery(id+"F2.opExtrude","CAP_FACE",FACE,{"disambiguationData":[OSD([sQuery(id+"F0.wireOp",EDGE,"E4"),subQ3,subQ2,subQ1,subQ0])],"isStart":true})]})],"blendedInto":[makeQuery(id+"F2.boolean.opBoolean","MERGE",FACE,{"derivedFrom":[makeQuery(id+"F1.opExtrude","CAP_FACE",FACE,{"disambiguationData":[OSD([sQuery(id+"F0.wireOp",EDGE,"E0.bottom"),sQuery(id+"F0.wireOp",EDGE,"E5.bottom"),sQuery(id+"F0.wireOp",EDGE,"E5.top"),sQuery(id+"F0.wireOp",EDGE,"E5.left"),sQuery(id+"F0.wireOp",EDGE,"E5.right"),subQ7,subQ6,subQ5,subQ4,subQ3,subQ2,subQ1,subQ0,subQ15,subQ14,subQ13,subQ12,subQ11,subQ10,subQ9,subQ8,sQuery(id+"F0.wireOp",EDGE,"E10.bottom"),sQuery(id+"F0.wireOp",EDGE,"E10.top"),sQuery(id+"F0.wireOp",EDGE,"E10.left"),sQuery(id+"F0.wireOp",EDGE,"E10.right"),sQuery(id+"F0.wireOp",EDGE,"E11.bottom"),sQuery(id+"F0.wireOp",EDGE,"E11.top"),sQuery(id+"F0.wireOp",EDGE,"E11.left"),sQuery(id+"F0.wireOp",EDGE,"E11.right"),subQ17,sQuery(id+"F0.wireOp",EDGE,"E12.top"),subQ16,sQuery(id+"F0.wireOp",EDGE,"E12.right"),sQuery(id+"F0.wireOp",EDGE,"E13.bottom"),sQuery(id+"F0.wireOp",EDGE,"E13.top"),sQuery(id+"F0.wireOp",EDGE,"E13.left"),sQuery(id+"F0.wireOp",EDGE,"E13.right"),sQuery(id+"F0.wireOp",EDGE,"E14.bottom"),sQuery(id+"F0.wireOp",EDGE,"E14.top"),sQuery(id+"F0.wireOp",EDGE,"E14.left"),sQuery(id+"F0.wireOp",EDGE,"E14.right"),sQuery(id+"F0.wireOp",EDGE,"E15.bottom"),sQuery(id+"F0.wireOp",EDGE,"E15.top"),sQuery(id+"F0.wireOp",EDGE,"E15.left"),sQuery(id+"F0.wireOp",EDGE,"E15.right"),sQuery(id+"F0.wireOp",EDGE,"E16"),sQuery(id+"F0.wireOp",EDGE,"E17")])],"isStart":true}),makeQuery(id+"F2.opExtrude","CAP_FACE",FACE,{"disambiguationData":[OSD([sQuery(id+"F0.wireOp",EDGE,"E1"),subQ15,subQ14,subQ13,subQ12])],"isStart":true}),makeQuery(id+"F2.opExtrude","CAP_FACE",FACE,{"disambiguationData":[OSD([sQuery(id+"F0.wireOp",EDGE,"E2"),subQ11,subQ10,subQ9,subQ8])],"isStart":true}),makeQuery(id+"F2.opExtrude","CAP_FACE",FACE,{"disambiguationData":[OSD([sQuery(id+"F0.wireOp",EDGE,"E3"),subQ7,subQ6,subQ5,subQ4])],"isStart":true}),makeQuery(id+"F2.opExtrude","CAP_FACE",FACE,{"disambiguationData":[OSD([sQuery(id+"F0.wireOp",EDGE,"E4"),subQ3,subQ2,subQ1,subQ0])],"isStart":true})]})]});}
            chamfer(context, id + "F12", {"entities" : qUnion([Q0, Q1, Q2, Q3, Q4, Q5, Q6, Q7, Q8, Q9, Q10, Q11, Q12, Q13, Q14, Q15, Q16, Q17, Q18, Q19, Q20, Q21, Q22, Q23, Q24, Q25, Q26, Q27, Q28, Q29, Q30, Q31, Q32, Q33, Q34, Q35, Q36, Q37, Q38, Q39, Q40, Q41, Q42, Q43, Q44, Q45, Q46, Q47]), "width" : 1 * mm, "tangentPropagation" : true});
        }
        {
            var Q0;
            Q0=makeQuery(id+"F8.boolean.opBoolean","INTERSECT",EDGE,{"derivedFrom":[makeQuery(id+"F5.opExtrude","SWEPT_FACE",FACE,{"disambiguationData":[OSD([sQuery(id+"F0.wireOp",EDGE,"E0.left")])]}),makeQuery(id+"F8.opExtrude","SWEPT_FACE",FACE,{"disambiguationData":[OSD([sQuery(id+"F7.wireOp",EDGE,"E23")])]})]});
            var Q1;
            Q1=makeQuery(id+"F8.boolean.opBoolean","COPY",EDGE,{"derivedFrom":makeQuery(id+"F8.opExtrude","CAP_EDGE",EDGE,{"disambiguationData":[OSD([sQuery(id+"F7.wireOp",EDGE,"E23")])],"isStart":true})});
            var Q2;
            Q2=makeQuery(id+"F10.boolean.opBoolean","COPY",EDGE,{"derivedFrom":makeQuery(id+"F10.opExtrude","CAP_EDGE",EDGE,{"disambiguationData":[OSD([sQuery(id+"F9.wireOp",EDGE,"E26")])],"isStart":true})});
            var Q3;
            Q3=makeQuery(id+"F10.boolean.opBoolean","INTERSECT",EDGE,{"derivedFrom":[makeQuery(id+"F5.opExtrude","SWEPT_FACE",FACE,{"disambiguationData":[OSD([sQuery(id+"F0.wireOp",EDGE,"E5.top")])]}),makeQuery(id+"F10.opExtrude","SWEPT_FACE",FACE,{"disambiguationData":[OSD([sQuery(id+"F9.wireOp",EDGE,"E26")])]})]});
            fillet(context, id + "F13", {"entities" : qUnion([Q0, Q1, Q2, Q3]), "radius" : 1 * mm, "tangentPropagation" : true, "allowEdgeOverflow" : false});
        }
        {
            var Q0;
            Q0=makeQuery(id+"F5.opExtrude","SWEPT_FACE",FACE,{"disambiguationData":[OSD([sQuery(id+"F0.wireOp",EDGE,"E5.right")])]});
            var sketch = newSketch(context, id + "F14", { "sketchPlane" : qUnion([Q0])});
            skCircle(sketch, "E29", {"center": v(-21.75, -29.85) * mm, "radius": 1.75 * mm});
            skCircle(sketch, "E30", {"center": v(-21.75, -16.35) * mm, "radius": 1.75 * mm});
            skCircle(sketch, "E31", {"center": v(-21.75, -2.85) * mm, "radius": 1.75 * mm});
            skCircle(sketch, "E32", {"center": v(-21.75, -2.85) * mm, "radius": 3 * mm});
            skCircle(sketch, "E33", {"center": v(-21.75, -16.35) * mm, "radius": 3 * mm});
            skCircle(sketch, "E34", {"center": v(-21.75, -29.85) * mm, "radius": 3 * mm});
            skSolve(sketch);
        }
        {
            var Q0;
            Q0=makeQuery(id+"F14.imprint","IMPRINT",FACE,{"disambiguationData":[TD([[makeQuery(id+"F14.imprint","IMPRINT",EDGE,{"derivedFrom":sQuery(id+"F14.wireOp",EDGE,"E31")}),1.0]])]});
            var Q1;
            Q1=makeQuery(id+"F14.imprint","IMPRINT",FACE,{"disambiguationData":[TD([[makeQuery(id+"F14.imprint","IMPRINT",EDGE,{"derivedFrom":sQuery(id+"F14.wireOp",EDGE,"E30")}),1.0]])]});
            var Q2;
            Q2=makeQuery(id+"F14.imprint","IMPRINT",FACE,{"disambiguationData":[TD([[makeQuery(id+"F14.imprint","IMPRINT",EDGE,{"derivedFrom":sQuery(id+"F14.wireOp",EDGE,"E29")}),1.0]])]});
            extrude(context, id + "F15", {"entities" : qUnion([Q0, Q1, Q2]), "operationType" : NewBodyOperationType.REMOVE, "oppositeDirection" : true, "depth" : 5 * mm, "offsetDistance" : 25 * mm});
        }
        {
            var Q0;
            Q0=makeQuery(id+"F14.imprint","IMPRINT",FACE,{"disambiguationData":[TD([[makeQuery(id+"F14.imprint","IMPRINT",EDGE,{"derivedFrom":sQuery(id+"F14.wireOp",EDGE,"E29")}),-1.0]])]});
            var Q1;
            Q1=makeQuery(id+"F14.imprint","IMPRINT",FACE,{"disambiguationData":[TD([[makeQuery(id+"F14.imprint","IMPRINT",EDGE,{"derivedFrom":sQuery(id+"F14.wireOp",EDGE,"E30")}),-1.0]])]});
            var Q2;
            Q2=makeQuery(id+"F14.imprint","IMPRINT",FACE,{"disambiguationData":[TD([[makeQuery(id+"F14.imprint","IMPRINT",EDGE,{"derivedFrom":sQuery(id+"F14.wireOp",EDGE,"E31")}),-1.0]])]});
            extrude(context, id + "F16", {"entities" : qUnion([Q0, Q1, Q2]), "operationType" : NewBodyOperationType.REMOVE, "oppositeDirection" : true, "depth" : 2 * mm, "offsetDistance" : 25 * mm});
        }
    });
